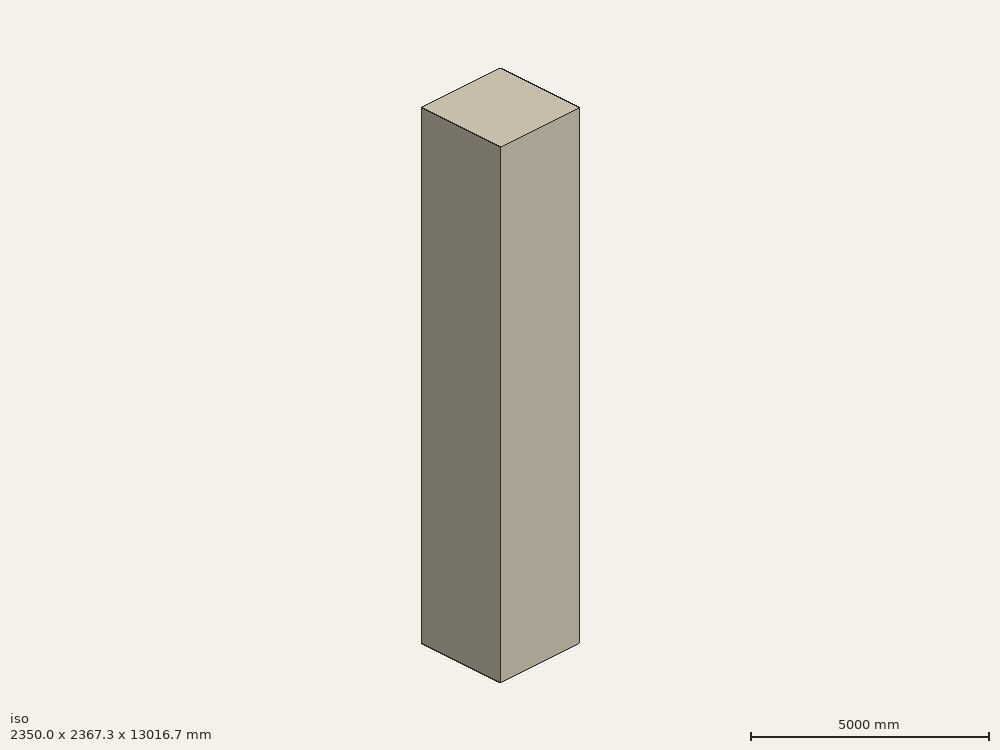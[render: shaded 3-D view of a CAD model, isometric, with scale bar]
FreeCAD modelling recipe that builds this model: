
FCSTD DOCUMENT  (FreeCAD 1.0R39109 (Git))
Label: revolveTester-7_scaled-a
License: All rights reserved
objects: App::DocumentObjectGroupPython×1252, Spreadsheet::Sheet×2, Part::FeaturePython×2, App::Part×2, Part::Cylinder×1, Sketcher::SketchObject×1, Part::Revolution×1, Part::Cut×1
note: 7 computed .brp shape members not serialized (recipe doc carries the construction recipe); baked Part::Feature solids carry a one-line shape summary decoded from their .brp

FEATURE [Spreadsheet::Sheet] defines
  cells = A1='constant; B1='HALFPI; C1(HALFPI)==pi / 2; A2='constant; B2='PI; C2(PI)==1 * pi; A3='constant; B3='TWOPI; C3(TWOPI)==2 * pi
FEATURE [Spreadsheet::Sheet] gdmlInfo
FEATURE [App::DocumentObjectGroupPython] Define  # scripted group (container) (typed FeaturePython)
  Group = -> [defines,gdmlInfo]
FEATURE [App::DocumentObjectGroupPython] HALFPI  # scripted group (container) (typed FeaturePython)
  name = HALFPI
  value = pi/2.
FEATURE [App::DocumentObjectGroupPython] PI  # scripted group (container) (typed FeaturePython)
  name = PI
  value = 1.*pi
FEATURE [App::DocumentObjectGroupPython] TWOPI  # scripted group (container) (typed FeaturePython)
  name = TWOPI
  value = 2.*pi
FEATURE [App::DocumentObjectGroupPython] Constants  # scripted group (container) (typed FeaturePython)
  Group = -> [HALFPI,PI,TWOPI]
FEATURE [App::DocumentObjectGroupPython] Quantities  # scripted group (container) (typed FeaturePython)
FEATURE [App::DocumentObjectGroupPython] Variables  # scripted group (container) (typed FeaturePython)
FEATURE [App::DocumentObjectGroupPython] Isotopes  # scripted group (container) (typed FeaturePython)
FEATURE [App::DocumentObjectGroupPython] Elements  # scripted group (container) (typed FeaturePython)
FEATURE [App::DocumentObjectGroupPython] Matrix  # scripted group (container) (typed FeaturePython)
FEATURE [App::DocumentObjectGroupPython] Surfaces  # scripted group (container) (typed FeaturePython)
FEATURE [App::DocumentObjectGroupPython] Opticals  # scripted group (container) (typed FeaturePython)
  Group = -> [Matrix,Surfaces]
FEATURE [App::DocumentObjectGroupPython] G4Isotopes  # scripted group (container) (typed FeaturePython)
FEATURE [App::DocumentObjectGroupPython] H_element  # scripted group (container) (typed FeaturePython)
  Z = 1
  atom_value = 1.008
  formula = H
  name = H_element
FEATURE [App::DocumentObjectGroupPython] He_element  # scripted group (container) (typed FeaturePython)
  Z = 2
  atom_value = 4.0026
  formula = He
  name = He_element
FEATURE [App::DocumentObjectGroupPython] Li_element  # scripted group (container) (typed FeaturePython)
  Z = 3
  atom_value = 6.94
  formula = Li
  name = Li_element
FEATURE [App::DocumentObjectGroupPython] Be_element  # scripted group (container) (typed FeaturePython)
  Z = 4
  atom_value = 9.01218
  formula = Be
  name = Be_element
FEATURE [App::DocumentObjectGroupPython] B_element  # scripted group (container) (typed FeaturePython)
  Z = 5
  atom_value = 10.81
  formula = B
  name = B_element
FEATURE [App::DocumentObjectGroupPython] C_element  # scripted group (container) (typed FeaturePython)
  Z = 6
  atom_value = 12.011
  formula = C
  name = C_element
FEATURE [App::DocumentObjectGroupPython] N_element  # scripted group (container) (typed FeaturePython)
  Z = 7
  atom_value = 14.007
  formula = N
  name = N_element
FEATURE [App::DocumentObjectGroupPython] O_element  # scripted group (container) (typed FeaturePython)
  Z = 8
  atom_value = 15.999
  formula = O
  name = O_element
FEATURE [App::DocumentObjectGroupPython] F_element  # scripted group (container) (typed FeaturePython)
  Z = 9
  atom_value = 18.9984
  formula = F
  name = F_element
FEATURE [App::DocumentObjectGroupPython] Ne_element  # scripted group (container) (typed FeaturePython)
  Z = 10
  atom_value = 20.1797
  formula = Ne
  name = Ne_element
FEATURE [App::DocumentObjectGroupPython] Na_element  # scripted group (container) (typed FeaturePython)
  Z = 11
  atom_value = 22.9898
  formula = Na
  name = Na_element
FEATURE [App::DocumentObjectGroupPython] Mg_element  # scripted group (container) (typed FeaturePython)
  Z = 12
  atom_value = 24.305
  formula = Mg
  name = Mg_element
FEATURE [App::DocumentObjectGroupPython] Al_element  # scripted group (container) (typed FeaturePython)
  Z = 13
  atom_value = 26.9815
  formula = Al
  name = Al_element
FEATURE [App::DocumentObjectGroupPython] Si_element  # scripted group (container) (typed FeaturePython)
  Z = 14
  atom_value = 28.085
  formula = Si
  name = Si_element
FEATURE [App::DocumentObjectGroupPython] P_element  # scripted group (container) (typed FeaturePython)
  Z = 15
  atom_value = 30.9738
  formula = P
  name = P_element
FEATURE [App::DocumentObjectGroupPython] S_element  # scripted group (container) (typed FeaturePython)
  Z = 16
  atom_value = 32.06
  formula = S
  name = S_element
FEATURE [App::DocumentObjectGroupPython] Cl_element  # scripted group (container) (typed FeaturePython)
  Z = 17
  atom_value = 35.45
  formula = Cl
  name = Cl_element
FEATURE [App::DocumentObjectGroupPython] Ar_element  # scripted group (container) (typed FeaturePython)
  Z = 18
  atom_value = 39.95
  formula = Ar
  name = Ar_element
FEATURE [App::DocumentObjectGroupPython] K_element  # scripted group (container) (typed FeaturePython)
  Z = 19
  atom_value = 39.0983
  formula = K
  name = K_element
FEATURE [App::DocumentObjectGroupPython] Ca_element  # scripted group (container) (typed FeaturePython)
  Z = 20
  atom_value = 40.078
  formula = Ca
  name = Ca_element
FEATURE [App::DocumentObjectGroupPython] Sc_element  # scripted group (container) (typed FeaturePython)
  Z = 21
  atom_value = 44.9559
  formula = Sc
  name = Sc_element
FEATURE [App::DocumentObjectGroupPython] Ti_element  # scripted group (container) (typed FeaturePython)
  Z = 22
  atom_value = 47.867
  formula = Ti
  name = Ti_element
FEATURE [App::DocumentObjectGroupPython] V_element  # scripted group (container) (typed FeaturePython)
  Z = 23
  atom_value = 50.9415
  formula = V
  name = V_element
FEATURE [App::DocumentObjectGroupPython] Cr_element  # scripted group (container) (typed FeaturePython)
  Z = 24
  atom_value = 51.9961
  formula = Cr
  name = Cr_element
FEATURE [App::DocumentObjectGroupPython] Mn_element  # scripted group (container) (typed FeaturePython)
  Z = 25
  atom_value = 54.938
  formula = Mn
  name = Mn_element
FEATURE [App::DocumentObjectGroupPython] Fe_element  # scripted group (container) (typed FeaturePython)
  Z = 26
  atom_value = 55.845
  formula = Fe
  name = Fe_element
FEATURE [App::DocumentObjectGroupPython] Co_element  # scripted group (container) (typed FeaturePython)
  Z = 27
  atom_value = 58.9332
  formula = Co
  name = Co_element
FEATURE [App::DocumentObjectGroupPython] Ni_element  # scripted group (container) (typed FeaturePython)
  Z = 28
  atom_value = 58.6934
  formula = Ni
  name = Ni_element
FEATURE [App::DocumentObjectGroupPython] Cu_element  # scripted group (container) (typed FeaturePython)
  Z = 29
  atom_value = 63.546
  formula = Cu
  name = Cu_element
FEATURE [App::DocumentObjectGroupPython] Zn_element  # scripted group (container) (typed FeaturePython)
  Z = 30
  atom_value = 65.38
  formula = Zn
  name = Zn_element
FEATURE [App::DocumentObjectGroupPython] Ga_element  # scripted group (container) (typed FeaturePython)
  Z = 31
  atom_value = 69.723
  formula = Ga
  name = Ga_element
FEATURE [App::DocumentObjectGroupPython] Ge_element  # scripted group (container) (typed FeaturePython)
  Z = 32
  atom_value = 72.63
  formula = Ge
  name = Ge_element
FEATURE [App::DocumentObjectGroupPython] As_element  # scripted group (container) (typed FeaturePython)
  Z = 33
  atom_value = 74.9216
  formula = As
  name = As_element
FEATURE [App::DocumentObjectGroupPython] Se_element  # scripted group (container) (typed FeaturePython)
  Z = 34
  atom_value = 78.971
  formula = Se
  name = Se_element
FEATURE [App::DocumentObjectGroupPython] Br_element  # scripted group (container) (typed FeaturePython)
  Z = 35
  atom_value = 79.904
  formula = Br
  name = Br_element
FEATURE [App::DocumentObjectGroupPython] Kr_element  # scripted group (container) (typed FeaturePython)
  Z = 36
  atom_value = 83.798
  formula = Kr
  name = Kr_element
FEATURE [App::DocumentObjectGroupPython] Rb_element  # scripted group (container) (typed FeaturePython)
  Z = 37
  atom_value = 85.4678
  formula = Rb
  name = Rb_element
FEATURE [App::DocumentObjectGroupPython] Sr_element  # scripted group (container) (typed FeaturePython)
  Z = 38
  atom_value = 87.62
  formula = Sr
  name = Sr_element
FEATURE [App::DocumentObjectGroupPython] Y_element  # scripted group (container) (typed FeaturePython)
  Z = 39
  atom_value = 88.9058
  formula = Y
  name = Y_element
FEATURE [App::DocumentObjectGroupPython] Zr_element  # scripted group (container) (typed FeaturePython)
  Z = 40
  atom_value = 91.224
  formula = Zr
  name = Zr_element
FEATURE [App::DocumentObjectGroupPython] Nb_element  # scripted group (container) (typed FeaturePython)
  Z = 41
  atom_value = 92.9064
  formula = Nb
  name = Nb_element
FEATURE [App::DocumentObjectGroupPython] Mo_element  # scripted group (container) (typed FeaturePython)
  Z = 42
  atom_value = 95.95
  formula = Mo
  name = Mo_element
FEATURE [App::DocumentObjectGroupPython] Tc_element  # scripted group (container) (typed FeaturePython)
  Z = 43
  atom_value = 97
  formula = Tc
  name = Tc_element
FEATURE [App::DocumentObjectGroupPython] Ru_element  # scripted group (container) (typed FeaturePython)
  Z = 44
  atom_value = 101.07
  formula = Ru
  name = Ru_element
FEATURE [App::DocumentObjectGroupPython] Rh_element  # scripted group (container) (typed FeaturePython)
  Z = 45
  atom_value = 102.905
  formula = Rh
  name = Rh_element
FEATURE [App::DocumentObjectGroupPython] Pd_element  # scripted group (container) (typed FeaturePython)
  Z = 46
  atom_value = 106.42
  formula = Pd
  name = Pd_element
FEATURE [App::DocumentObjectGroupPython] Ag_element  # scripted group (container) (typed FeaturePython)
  Z = 47
  atom_value = 107.868
  formula = Ag
  name = Ag_element
FEATURE [App::DocumentObjectGroupPython] Cd_element  # scripted group (container) (typed FeaturePython)
  Z = 48
  atom_value = 112.414
  formula = Cd
  name = Cd_element
FEATURE [App::DocumentObjectGroupPython] In_element  # scripted group (container) (typed FeaturePython)
  Z = 49
  atom_value = 114.818
  formula = In
  name = In_element
FEATURE [App::DocumentObjectGroupPython] Sn_element  # scripted group (container) (typed FeaturePython)
  Z = 50
  atom_value = 118.71
  formula = Sn
  name = Sn_element
FEATURE [App::DocumentObjectGroupPython] Sb_element  # scripted group (container) (typed FeaturePython)
  Z = 51
  atom_value = 121.76
  formula = Sb
  name = Sb_element
FEATURE [App::DocumentObjectGroupPython] Te_element  # scripted group (container) (typed FeaturePython)
  Z = 52
  atom_value = 127.6
  formula = Te
  name = Te_element
FEATURE [App::DocumentObjectGroupPython] I_element  # scripted group (container) (typed FeaturePython)
  Z = 53
  atom_value = 126.904
  formula = I
  name = I_element
FEATURE [App::DocumentObjectGroupPython] Xe_element  # scripted group (container) (typed FeaturePython)
  Z = 54
  atom_value = 131.293
  formula = Xe
  name = Xe_element
FEATURE [App::DocumentObjectGroupPython] Cs_element  # scripted group (container) (typed FeaturePython)
  Z = 55
  atom_value = 132.905
  formula = Cs
  name = Cs_element
FEATURE [App::DocumentObjectGroupPython] Ba_element  # scripted group (container) (typed FeaturePython)
  Z = 56
  atom_value = 137.327
  formula = Ba
  name = Ba_element
FEATURE [App::DocumentObjectGroupPython] La_element  # scripted group (container) (typed FeaturePython)
  Z = 57
  atom_value = 138.905
  formula = La
  name = La_element
FEATURE [App::DocumentObjectGroupPython] Ce_element  # scripted group (container) (typed FeaturePython)
  Z = 58
  atom_value = 140.116
  formula = Ce
  name = Ce_element
FEATURE [App::DocumentObjectGroupPython] Pr_element  # scripted group (container) (typed FeaturePython)
  Z = 59
  atom_value = 140.908
  formula = Pr
  name = Pr_element
FEATURE [App::DocumentObjectGroupPython] Nd_element  # scripted group (container) (typed FeaturePython)
  Z = 60
  atom_value = 144.242
  formula = Nd
  name = Nd_element
FEATURE [App::DocumentObjectGroupPython] Pm_element  # scripted group (container) (typed FeaturePython)
  Z = 61
  atom_value = 145
  formula = Pm
  name = Pm_element
FEATURE [App::DocumentObjectGroupPython] Sm_element  # scripted group (container) (typed FeaturePython)
  Z = 62
  atom_value = 150.36
  formula = Sm
  name = Sm_element
FEATURE [App::DocumentObjectGroupPython] Eu_element  # scripted group (container) (typed FeaturePython)
  Z = 63
  atom_value = 151.964
  formula = Eu
  name = Eu_element
FEATURE [App::DocumentObjectGroupPython] Gd_element  # scripted group (container) (typed FeaturePython)
  Z = 64
  atom_value = 157.25
  formula = Gd
  name = Gd_element
FEATURE [App::DocumentObjectGroupPython] Tb_element  # scripted group (container) (typed FeaturePython)
  Z = 65
  atom_value = 158.925
  formula = Tb
  name = Tb_element
FEATURE [App::DocumentObjectGroupPython] Dy_element  # scripted group (container) (typed FeaturePython)
  Z = 66
  atom_value = 162.5
  formula = Dy
  name = Dy_element
FEATURE [App::DocumentObjectGroupPython] Ho_element  # scripted group (container) (typed FeaturePython)
  Z = 67
  atom_value = 164.93
  formula = Ho
  name = Ho_element
FEATURE [App::DocumentObjectGroupPython] Er_element  # scripted group (container) (typed FeaturePython)
  Z = 68
  atom_value = 167.259
  formula = Er
  name = Er_element
FEATURE [App::DocumentObjectGroupPython] Tm_element  # scripted group (container) (typed FeaturePython)
  Z = 69
  atom_value = 168.934
  formula = Tm
  name = Tm_element
FEATURE [App::DocumentObjectGroupPython] Yb_element  # scripted group (container) (typed FeaturePython)
  Z = 70
  atom_value = 173.045
  formula = Yb
  name = Yb_element
FEATURE [App::DocumentObjectGroupPython] Lu_element  # scripted group (container) (typed FeaturePython)
  Z = 71
  atom_value = 174.967
  formula = Lu
  name = Lu_element
FEATURE [App::DocumentObjectGroupPython] Hf_element  # scripted group (container) (typed FeaturePython)
  Z = 72
  atom_value = 178.49
  formula = Hf
  name = Hf_element
FEATURE [App::DocumentObjectGroupPython] Ta_element  # scripted group (container) (typed FeaturePython)
  Z = 73
  atom_value = 180.948
  formula = Ta
  name = Ta_element
FEATURE [App::DocumentObjectGroupPython] W_element  # scripted group (container) (typed FeaturePython)
  Z = 74
  atom_value = 183.84
  formula = W
  name = W_element
FEATURE [App::DocumentObjectGroupPython] Re_element  # scripted group (container) (typed FeaturePython)
  Z = 75
  atom_value = 186.207
  formula = Re
  name = Re_element
FEATURE [App::DocumentObjectGroupPython] Os_element  # scripted group (container) (typed FeaturePython)
  Z = 76
  atom_value = 190.23
  formula = Os
  name = Os_element
FEATURE [App::DocumentObjectGroupPython] Ir_element  # scripted group (container) (typed FeaturePython)
  Z = 77
  atom_value = 192.217
  formula = Ir
  name = Ir_element
FEATURE [App::DocumentObjectGroupPython] Pt_element  # scripted group (container) (typed FeaturePython)
  Z = 78
  atom_value = 195.084
  formula = Pt
  name = Pt_element
FEATURE [App::DocumentObjectGroupPython] Au_element  # scripted group (container) (typed FeaturePython)
  Z = 79
  atom_value = 196.967
  formula = Au
  name = Au_element
FEATURE [App::DocumentObjectGroupPython] Hg_element  # scripted group (container) (typed FeaturePython)
  Z = 80
  atom_value = 200.592
  formula = Hg
  name = Hg_element
FEATURE [App::DocumentObjectGroupPython] Tl_element  # scripted group (container) (typed FeaturePython)
  Z = 81
  atom_value = 204.38
  formula = Tl
  name = Tl_element
FEATURE [App::DocumentObjectGroupPython] Pb_element  # scripted group (container) (typed FeaturePython)
  Z = 82
  atom_value = 207.2
  formula = Pb
  name = Pb_element
FEATURE [App::DocumentObjectGroupPython] Bi_element  # scripted group (container) (typed FeaturePython)
  Z = 83
  atom_value = 208.98
  formula = Bi
  name = Bi_element
FEATURE [App::DocumentObjectGroupPython] Po_element  # scripted group (container) (typed FeaturePython)
  Z = 84
  atom_value = 209
  formula = Po
  name = Po_element
FEATURE [App::DocumentObjectGroupPython] At_element  # scripted group (container) (typed FeaturePython)
  Z = 85
  atom_value = 210
  formula = At
  name = At_element
FEATURE [App::DocumentObjectGroupPython] Rn_element  # scripted group (container) (typed FeaturePython)
  Z = 86
  atom_value = 222
  formula = Rn
  name = Rn_element
FEATURE [App::DocumentObjectGroupPython] Fr_element  # scripted group (container) (typed FeaturePython)
  Z = 87
  atom_value = 223
  formula = Fr
  name = Fr_element
FEATURE [App::DocumentObjectGroupPython] Ra_element  # scripted group (container) (typed FeaturePython)
  Z = 88
  atom_value = 226
  formula = Ra
  name = Ra_element
FEATURE [App::DocumentObjectGroupPython] Ac_element  # scripted group (container) (typed FeaturePython)
  Z = 89
  atom_value = 227
  formula = Ac
  name = Ac_element
FEATURE [App::DocumentObjectGroupPython] Th_element  # scripted group (container) (typed FeaturePython)
  Z = 90
  atom_value = 232.038
  formula = Th
  name = Th_element
FEATURE [App::DocumentObjectGroupPython] Pa_element  # scripted group (container) (typed FeaturePython)
  Z = 91
  atom_value = 231.036
  formula = Pa
  name = Pa_element
FEATURE [App::DocumentObjectGroupPython] U_element  # scripted group (container) (typed FeaturePython)
  Z = 92
  atom_value = 238.029
  formula = U
  name = U_element
FEATURE [App::DocumentObjectGroupPython] Np_element  # scripted group (container) (typed FeaturePython)
  Z = 93
  atom_value = 237
  formula = Np
  name = Np_element
FEATURE [App::DocumentObjectGroupPython] Pu_element  # scripted group (container) (typed FeaturePython)
  Z = 94
  atom_value = 244
  formula = Pu
  name = Pu_element
FEATURE [App::DocumentObjectGroupPython] Am_element  # scripted group (container) (typed FeaturePython)
  Z = 95
  atom_value = 243
  formula = Am
  name = Am_element
FEATURE [App::DocumentObjectGroupPython] Cm_element  # scripted group (container) (typed FeaturePython)
  Z = 96
  atom_value = 247
  formula = Cm
  name = Cm_element
FEATURE [App::DocumentObjectGroupPython] Bk_element  # scripted group (container) (typed FeaturePython)
  Z = 97
  atom_value = 247
  formula = Bk
  name = Bk_element
FEATURE [App::DocumentObjectGroupPython] Cf_element  # scripted group (container) (typed FeaturePython)
  Z = 98
  atom_value = 251
  formula = Cf
  name = Cf_element
FEATURE [App::DocumentObjectGroupPython] G4Elements  # scripted group (container) (typed FeaturePython)
  Group = -> [H_element,He_element,Li_element,Be_element,B_element,C_element,N_element,O_element,F_element,Ne_element,Na_element,Mg_element,Al_element,Si_element,P_element,S_element,Cl_element,Ar_element,K_element,Ca_element,Sc_element,Ti_element,V_element,Cr_element,Mn_element,Fe_element,Co_element,Ni_element,Cu_element,Zn_element,Ga_element,Ge_element,As_element,Se_element,Br_element,Kr_element,Rb_element,+61 more]
FEATURE [App::DocumentObjectGroupPython] H_element001  label="H_element : 0.101"  # scripted group (container) (typed FeaturePython)
  n = 0.101327
FEATURE [App::DocumentObjectGroupPython] C_element001  label="C_element : 0.775"  # scripted group (container) (typed FeaturePython)
  n = 0.7755
FEATURE [App::DocumentObjectGroupPython] N_element001  label="N_element : 0.035"  # scripted group (container) (typed FeaturePython)
  n = 0.035057
FEATURE [App::DocumentObjectGroupPython] O_element001  label="O_element : 0.052"  # scripted group (container) (typed FeaturePython)
  n = 0.0523159
FEATURE [App::DocumentObjectGroupPython] F_element001  label="F_element : 0.017"  # scripted group (container) (typed FeaturePython)
  n = 0.017422
FEATURE [App::DocumentObjectGroupPython] Ca_element001  label="Ca_element : 0.018"  # scripted group (container) (typed FeaturePython)
  n = 0.018378
FEATURE [App::DocumentObjectGroupPython] G4_A_150_TISSUE  label="G4_A-150_TISSUE"  # scripted group (container) (typed FeaturePython)
  Dunit = g/cm3
  Dvalue = 1.127
  Group = -> [H_element001,C_element001,N_element001,O_element001,F_element001,Ca_element001]
  conduct = 2
  density = 1
  expand = 3
  formula = G4_A-150_TISSUE
  name = G4_A-150_TISSUE
  specific = 4
FEATURE [App::DocumentObjectGroupPython] C_element002  label="C_element : 3"  # scripted group (container) (typed FeaturePython)
  n = 3
  ref = C_element
FEATURE [App::DocumentObjectGroupPython] H_element002  label="H_element : 6"  # scripted group (container) (typed FeaturePython)
  n = 6
  ref = H_element
FEATURE [App::DocumentObjectGroupPython] O_element002  label="O_element : 1"  # scripted group (container) (typed FeaturePython)
  n = 1
  ref = O_element
FEATURE [App::DocumentObjectGroupPython] G4_ACETONE  # scripted group (container) (typed FeaturePython)
  Dunit = g/cm3
  Dvalue = 0.7899
  Group = -> [C_element002,H_element002,O_element002]
  conduct = 2
  density = 1
  expand = 3
  formula = G4_ACETONE
  name = G4_ACETONE
  specific = 4
FEATURE [App::DocumentObjectGroupPython] C_element003  label="C_element : 2"  # scripted group (container) (typed FeaturePython)
  n = 2
  ref = C_element
FEATURE [App::DocumentObjectGroupPython] H_element003  label="H_element : 2"  # scripted group (container) (typed FeaturePython)
  n = 2
  ref = H_element
FEATURE [App::DocumentObjectGroupPython] G4_ACETYLENE  # scripted group (container) (typed FeaturePython)
  Dunit = g/cm3
  Dvalue = 0.0010967
  Group = -> [C_element003,H_element003]
  conduct = 2
  density = 1
  expand = 3
  formula = G4_ACETYLENE
  name = G4_ACETYLENE
  specific = 4
FEATURE [App::DocumentObjectGroupPython] C_element004  label="C_element : 5"  # scripted group (container) (typed FeaturePython)
  n = 5
  ref = C_element
FEATURE [App::DocumentObjectGroupPython] H_element004  label="H_element : 5"  # scripted group (container) (typed FeaturePython)
  n = 5
  ref = H_element
FEATURE [App::DocumentObjectGroupPython] N_element002  label="N_element : 5"  # scripted group (container) (typed FeaturePython)
  n = 5
  ref = N_element
FEATURE [App::DocumentObjectGroupPython] G4_ADENINE  # scripted group (container) (typed FeaturePython)
  Dunit = g/cm3
  Dvalue = 1.6
  Group = -> [C_element004,H_element004,N_element002]
  conduct = 2
  density = 1
  expand = 3
  formula = G4_ADENINE
  name = G4_ADENINE
  specific = 4
FEATURE [App::DocumentObjectGroupPython] H_element005  label="H_element : 0.114"  # scripted group (container) (typed FeaturePython)
  n = 0.114
FEATURE [App::DocumentObjectGroupPython] C_element005  label="C_element : 0.598"  # scripted group (container) (typed FeaturePython)
  n = 0.598
FEATURE [App::DocumentObjectGroupPython] N_element003  label="N_element : 0.007"  # scripted group (container) (typed FeaturePython)
  n = 0.007
FEATURE [App::DocumentObjectGroupPython] O_element003  label="O_element : 0.278"  # scripted group (container) (typed FeaturePython)
  n = 0.278
FEATURE [App::DocumentObjectGroupPython] Na_element001  label="Na_element : 0.001"  # scripted group (container) (typed FeaturePython)
  n = 0.001
FEATURE [App::DocumentObjectGroupPython] S_element001  label="S_element : 0.001"  # scripted group (container) (typed FeaturePython)
  n = 0.001
FEATURE [App::DocumentObjectGroupPython] Cl_element001  label="Cl_element : 0.001"  # scripted group (container) (typed FeaturePython)
  n = 0.001
FEATURE [App::DocumentObjectGroupPython] G4_ADIPOSE_TISSUE_ICRP  # scripted group (container) (typed FeaturePython)
  Dunit = g/cm3
  Dvalue = 0.95
  Group = -> [H_element005,C_element005,N_element003,O_element003,Na_element001,S_element001,Cl_element001]
  conduct = 2
  density = 1
  expand = 3
  formula = G4_ADIPOSE_TISSUE_ICRP
  name = G4_ADIPOSE_TISSUE_ICRP
  specific = 4
FEATURE [App::DocumentObjectGroupPython] C_element006  label="C_element : 0.000"  # scripted group (container) (typed FeaturePython)
  n = 0.000124
FEATURE [App::DocumentObjectGroupPython] N_element004  label="N_element : 0.755"  # scripted group (container) (typed FeaturePython)
  n = 0.755268
FEATURE [App::DocumentObjectGroupPython] O_element004  label="O_element : 0.232"  # scripted group (container) (typed FeaturePython)
  n = 0.231781
FEATURE [App::DocumentObjectGroupPython] Ar_element001  label="Ar_element : 0.013"  # scripted group (container) (typed FeaturePython)
  n = 0.012827
FEATURE [App::DocumentObjectGroupPython] G4_AIR  # scripted group (container) (typed FeaturePython)
  Dunit = g/cm3
  Dvalue = 0.00120479
  Group = -> [C_element006,N_element004,O_element004,Ar_element001]
  conduct = 2
  density = 1
  expand = 3
  formula = G4_AIR
  name = G4_AIR
  specific = 4
FEATURE [App::DocumentObjectGroupPython] C_element007  label="C_element : 006"  # scripted group (container) (typed FeaturePython)
  n = 3
  ref = C_element
FEATURE [App::DocumentObjectGroupPython] H_element006  label="H_element : 7"  # scripted group (container) (typed FeaturePython)
  n = 7
  ref = H_element
FEATURE [App::DocumentObjectGroupPython] N_element005  label="N_element : 1"  # scripted group (container) (typed FeaturePython)
  n = 1
  ref = N_element
FEATURE [App::DocumentObjectGroupPython] O_element005  label="O_element : 2"  # scripted group (container) (typed FeaturePython)
  n = 2
  ref = O_element
FEATURE [App::DocumentObjectGroupPython] G4_ALANINE  # scripted group (container) (typed FeaturePython)
  Dunit = g/cm3
  Dvalue = 1.42
  Group = -> [C_element007,H_element006,N_element005,O_element005]
  conduct = 2
  density = 1
  expand = 3
  formula = G4_ALANINE
  name = G4_ALANINE
  specific = 4
FEATURE [App::DocumentObjectGroupPython] Al_element001  label="Al_element : 2"  # scripted group (container) (typed FeaturePython)
  n = 2
  ref = Al_element
FEATURE [App::DocumentObjectGroupPython] O_element006  label="O_element : 3"  # scripted group (container) (typed FeaturePython)
  n = 3
  ref = O_element
FEATURE [App::DocumentObjectGroupPython] G4_ALUMINUM_OXIDE  # scripted group (container) (typed FeaturePython)
  Dunit = g/cm3
  Dvalue = 3.97
  Group = -> [Al_element001,O_element006]
  conduct = 2
  density = 1
  expand = 3
  formula = G4_ALUMINUM_OXIDE
  name = G4_ALUMINUM_OXIDE
  specific = 4
FEATURE [App::DocumentObjectGroupPython] H_element007  label="H_element : 0.106"  # scripted group (container) (typed FeaturePython)
  n = 0.10593
FEATURE [App::DocumentObjectGroupPython] C_element008  label="C_element : 0.789"  # scripted group (container) (typed FeaturePython)
  n = 0.788974
FEATURE [App::DocumentObjectGroupPython] O_element007  label="O_element : 0.105"  # scripted group (container) (typed FeaturePython)
  n = 0.105096
FEATURE [App::DocumentObjectGroupPython] G4_AMBER  # scripted group (container) (typed FeaturePython)
  Dunit = g/cm3
  Dvalue = 1.1
  Group = -> [H_element007,C_element008,O_element007]
  conduct = 2
  density = 1
  expand = 3
  formula = G4_AMBER
  name = G4_AMBER
  specific = 4
FEATURE [App::DocumentObjectGroupPython] N_element006  label="N_element : 006"  # scripted group (container) (typed FeaturePython)
  n = 1
  ref = N_element
FEATURE [App::DocumentObjectGroupPython] H_element008  label="H_element : 3"  # scripted group (container) (typed FeaturePython)
  n = 3
  ref = H_element
FEATURE [App::DocumentObjectGroupPython] G4_AMMONIA  # scripted group (container) (typed FeaturePython)
  Dunit = g/cm3
  Dvalue = 0.000826019
  Group = -> [N_element006,H_element008]
  conduct = 2
  density = 1
  expand = 3
  formula = G4_AMMONIA
  name = G4_AMMONIA
  specific = 4
FEATURE [App::DocumentObjectGroupPython] C_element009  label="C_element : 6"  # scripted group (container) (typed FeaturePython)
  n = 6
  ref = C_element
FEATURE [App::DocumentObjectGroupPython] H_element009  label="H_element : 008"  # scripted group (container) (typed FeaturePython)
  n = 7
  ref = H_element
FEATURE [App::DocumentObjectGroupPython] N_element007  label="N_element : 007"  # scripted group (container) (typed FeaturePython)
  n = 1
  ref = N_element
FEATURE [App::DocumentObjectGroupPython] G4_ANILINE  # scripted group (container) (typed FeaturePython)
  Dunit = g/cm3
  Dvalue = 1.0235
  Group = -> [C_element009,H_element009,N_element007]
  conduct = 2
  density = 1
  expand = 3
  formula = G4_ANILINE
  name = G4_ANILINE
  specific = 4
FEATURE [App::DocumentObjectGroupPython] C_element010  label="C_element : 14"  # scripted group (container) (typed FeaturePython)
  n = 14
  ref = C_element
FEATURE [App::DocumentObjectGroupPython] H_element010  label="H_element : 10"  # scripted group (container) (typed FeaturePython)
  n = 10
  ref = H_element
FEATURE [App::DocumentObjectGroupPython] G4_ANTHRACENE  # scripted group (container) (typed FeaturePython)
  Dunit = g/cm3
  Dvalue = 1.283
  Group = -> [C_element010,H_element010]
  conduct = 2
  density = 1
  expand = 3
  formula = G4_ANTHRACENE
  name = G4_ANTHRACENE
  specific = 4
FEATURE [App::DocumentObjectGroupPython] H_element011  label="H_element : 0.065"  # scripted group (container) (typed FeaturePython)
  n = 0.0654709
FEATURE [App::DocumentObjectGroupPython] C_element011  label="C_element : 0.537"  # scripted group (container) (typed FeaturePython)
  n = 0.536944
FEATURE [App::DocumentObjectGroupPython] N_element008  label="N_element : 0.021"  # scripted group (container) (typed FeaturePython)
  n = 0.0215
FEATURE [App::DocumentObjectGroupPython] O_element008  label="O_element : 0.032"  # scripted group (container) (typed FeaturePython)
  n = 0.032085
FEATURE [App::DocumentObjectGroupPython] F_element002  label="F_element : 0.167"  # scripted group (container) (typed FeaturePython)
  n = 0.167411
FEATURE [App::DocumentObjectGroupPython] Ca_element002  label="Ca_element : 0.177"  # scripted group (container) (typed FeaturePython)
  n = 0.176589
FEATURE [App::DocumentObjectGroupPython] G4_B_100_BONE  label="G4_B-100_BONE"  # scripted group (container) (typed FeaturePython)
  Dunit = g/cm3
  Dvalue = 1.45
  Group = -> [H_element011,C_element011,N_element008,O_element008,F_element002,Ca_element002]
  conduct = 2
  density = 1
  expand = 3
  formula = G4_B-100_BONE
  name = G4_B-100_BONE
  specific = 4
FEATURE [App::DocumentObjectGroupPython] H_element012  label="H_element : 0.057"  # scripted group (container) (typed FeaturePython)
  n = 0.057441
FEATURE [App::DocumentObjectGroupPython] C_element012  label="C_element : 0.790"  # scripted group (container) (typed FeaturePython)
  n = 0.774591
FEATURE [App::DocumentObjectGroupPython] O_element009  label="O_element : 0.168"  # scripted group (container) (typed FeaturePython)
  n = 0.167968
FEATURE [App::DocumentObjectGroupPython] G4_BAKELITE  # scripted group (container) (typed FeaturePython)
  Dunit = g/cm3
  Dvalue = 1.25
  Group = -> [H_element012,C_element012,O_element009]
  conduct = 2
  density = 1
  expand = 3
  formula = G4_BAKELITE
  name = G4_BAKELITE
  specific = 4
FEATURE [App::DocumentObjectGroupPython] Ba_element001  label="Ba_element : 1"  # scripted group (container) (typed FeaturePython)
  n = 1
  ref = Ba_element
FEATURE [App::DocumentObjectGroupPython] F_element003  label="F_element : 2"  # scripted group (container) (typed FeaturePython)
  n = 2
  ref = F_element
FEATURE [App::DocumentObjectGroupPython] G4_BARIUM_FLUORIDE  # scripted group (container) (typed FeaturePython)
  Dunit = g/cm3
  Dvalue = 4.89
  Group = -> [Ba_element001,F_element003]
  conduct = 2
  density = 1
  expand = 3
  formula = G4_BARIUM_FLUORIDE
  name = G4_BARIUM_FLUORIDE
  specific = 4
FEATURE [App::DocumentObjectGroupPython] Ba_element002  label="Ba_element : 002"  # scripted group (container) (typed FeaturePython)
  n = 1
  ref = Ba_element
FEATURE [App::DocumentObjectGroupPython] S_element002  label="S_element : 1"  # scripted group (container) (typed FeaturePython)
  n = 1
  ref = S_element
FEATURE [App::DocumentObjectGroupPython] O_element010  label="O_element : 4"  # scripted group (container) (typed FeaturePython)
  n = 4
  ref = O_element
FEATURE [App::DocumentObjectGroupPython] G4_BARIUM_SULFATE  # scripted group (container) (typed FeaturePython)
  Dunit = g/cm3
  Dvalue = 4.5
  Group = -> [Ba_element002,S_element002,O_element010]
  conduct = 2
  density = 1
  expand = 3
  formula = G4_BARIUM_SULFATE
  name = G4_BARIUM_SULFATE
  specific = 4
FEATURE [App::DocumentObjectGroupPython] C_element013  label="C_element : 007"  # scripted group (container) (typed FeaturePython)
  n = 6
  ref = C_element
FEATURE [App::DocumentObjectGroupPython] H_element013  label="H_element : 009"  # scripted group (container) (typed FeaturePython)
  n = 6
  ref = H_element
FEATURE [App::DocumentObjectGroupPython] G4_BENZENE  # scripted group (container) (typed FeaturePython)
  Dunit = g/cm3
  Dvalue = 0.87865
  Group = -> [C_element013,H_element013]
  conduct = 2
  density = 1
  expand = 3
  formula = G4_BENZENE
  name = G4_BENZENE
  specific = 4
FEATURE [App::DocumentObjectGroupPython] Be_element001  label="Be_element : 1"  # scripted group (container) (typed FeaturePython)
  n = 1
  ref = Be_element
FEATURE [App::DocumentObjectGroupPython] O_element011  label="O_element : 005"  # scripted group (container) (typed FeaturePython)
  n = 1
  ref = O_element
FEATURE [App::DocumentObjectGroupPython] G4_BERYLLIUM_OXIDE  # scripted group (container) (typed FeaturePython)
  Dunit = g/cm3
  Dvalue = 3.01
  Group = -> [Be_element001,O_element011]
  conduct = 2
  density = 1
  expand = 3
  formula = G4_BERYLLIUM_OXIDE
  name = G4_BERYLLIUM_OXIDE
  specific = 4
FEATURE [App::DocumentObjectGroupPython] Bi_element001  label="Bi_element : 4"  # scripted group (container) (typed FeaturePython)
  n = 4
  ref = Bi_element
FEATURE [App::DocumentObjectGroupPython] Ge_element001  label="Ge_element : 3"  # scripted group (container) (typed FeaturePython)
  n = 3
  ref = Ge_element
FEATURE [App::DocumentObjectGroupPython] O_element012  label="O_element : 12"  # scripted group (container) (typed FeaturePython)
  n = 12
  ref = O_element
FEATURE [App::DocumentObjectGroupPython] G4_BGO  # scripted group (container) (typed FeaturePython)
  Dunit = g/cm3
  Dvalue = 7.13
  Group = -> [Bi_element001,Ge_element001,O_element012]
  conduct = 2
  density = 1
  expand = 3
  formula = G4_BGO
  name = G4_BGO
  specific = 4
FEATURE [App::DocumentObjectGroupPython] H_element014  label="H_element : 0.102"  # scripted group (container) (typed FeaturePython)
  n = 0.102
FEATURE [App::DocumentObjectGroupPython] C_element014  label="C_element : 0.110"  # scripted group (container) (typed FeaturePython)
  n = 0.11
FEATURE [App::DocumentObjectGroupPython] N_element009  label="N_element : 0.033"  # scripted group (container) (typed FeaturePython)
  n = 0.033
FEATURE [App::DocumentObjectGroupPython] O_element013  label="O_element : 0.745"  # scripted group (container) (typed FeaturePython)
  n = 0.745
FEATURE [App::DocumentObjectGroupPython] Na_element002  label="Na_element : 0.002"  # scripted group (container) (typed FeaturePython)
  n = 0.001
FEATURE [App::DocumentObjectGroupPython] P_element001  label="P_element : 0.001"  # scripted group (container) (typed FeaturePython)
  n = 0.001
FEATURE [App::DocumentObjectGroupPython] S_element003  label="S_element : 0.002"  # scripted group (container) (typed FeaturePython)
  n = 0.002
FEATURE [App::DocumentObjectGroupPython] Cl_element002  label="Cl_element : 0.003"  # scripted group (container) (typed FeaturePython)
  n = 0.003
FEATURE [App::DocumentObjectGroupPython] K_element001  label="K_element : 0.002"  # scripted group (container) (typed FeaturePython)
  n = 0.002
FEATURE [App::DocumentObjectGroupPython] Fe_element001  label="Fe_element : 0.001"  # scripted group (container) (typed FeaturePython)
  n = 0.001
FEATURE [App::DocumentObjectGroupPython] G4_BLOOD_ICRP  # scripted group (container) (typed FeaturePython)
  Dunit = g/cm3
  Dvalue = 1.06
  Group = -> [H_element014,C_element014,N_element009,O_element013,Na_element002,P_element001,S_element003,Cl_element002,K_element001,Fe_element001]
  conduct = 2
  density = 1
  expand = 3
  formula = G4_BLOOD_ICRP
  name = G4_BLOOD_ICRP
  specific = 4
FEATURE [App::DocumentObjectGroupPython] H_element015  label="H_element : 0.064"  # scripted group (container) (typed FeaturePython)
  n = 0.064
FEATURE [App::DocumentObjectGroupPython] C_element015  label="C_element : 0.278"  # scripted group (container) (typed FeaturePython)
  n = 0.278
FEATURE [App::DocumentObjectGroupPython] N_element010  label="N_element : 0.027"  # scripted group (container) (typed FeaturePython)
  n = 0.027
FEATURE [App::DocumentObjectGroupPython] O_element014  label="O_element : 0.410"  # scripted group (container) (typed FeaturePython)
  n = 0.41
FEATURE [App::DocumentObjectGroupPython] Mg_element001  label="Mg_element : 0.002"  # scripted group (container) (typed FeaturePython)
  n = 0.002
FEATURE [App::DocumentObjectGroupPython] P_element002  label="P_element : 0.070"  # scripted group (container) (typed FeaturePython)
  n = 0.07
FEATURE [App::DocumentObjectGroupPython] S_element004  label="S_element : 0.003"  # scripted group (container) (typed FeaturePython)
  n = 0.002
FEATURE [App::DocumentObjectGroupPython] Ca_element003  label="Ca_element : 0.147"  # scripted group (container) (typed FeaturePython)
  n = 0.147
FEATURE [App::DocumentObjectGroupPython] G4_BONE_COMPACT_ICRU  # scripted group (container) (typed FeaturePython)
  Dunit = g/cm3
  Dvalue = 1.85
  Group = -> [H_element015,C_element015,N_element010,O_element014,Mg_element001,P_element002,S_element004,Ca_element003]
  conduct = 2
  density = 1
  expand = 3
  formula = G4_BONE_COMPACT_ICRU
  name = G4_BONE_COMPACT_ICRU
  specific = 4
FEATURE [App::DocumentObjectGroupPython] H_element016  label="H_element : 0.034"  # scripted group (container) (typed FeaturePython)
  n = 0.034
FEATURE [App::DocumentObjectGroupPython] C_element016  label="C_element : 0.155"  # scripted group (container) (typed FeaturePython)
  n = 0.155
FEATURE [App::DocumentObjectGroupPython] N_element011  label="N_element : 0.042"  # scripted group (container) (typed FeaturePython)
  n = 0.042
FEATURE [App::DocumentObjectGroupPython] O_element015  label="O_element : 0.435"  # scripted group (container) (typed FeaturePython)
  n = 0.435
FEATURE [App::DocumentObjectGroupPython] Na_element003  label="Na_element : 0.003"  # scripted group (container) (typed FeaturePython)
  n = 0.001
FEATURE [App::DocumentObjectGroupPython] Mg_element002  label="Mg_element : 0.003"  # scripted group (container) (typed FeaturePython)
  n = 0.002
FEATURE [App::DocumentObjectGroupPython] P_element003  label="P_element : 0.103"  # scripted group (container) (typed FeaturePython)
  n = 0.103
FEATURE [App::DocumentObjectGroupPython] S_element005  label="S_element : 0.004"  # scripted group (container) (typed FeaturePython)
  n = 0.003
FEATURE [App::DocumentObjectGroupPython] Ca_element004  label="Ca_element : 0.225"  # scripted group (container) (typed FeaturePython)
  n = 0.225
FEATURE [App::DocumentObjectGroupPython] G4_BONE_CORTICAL_ICRP  # scripted group (container) (typed FeaturePython)
  Dunit = g/cm3
  Dvalue = 1.92
  Group = -> [H_element016,C_element016,N_element011,O_element015,Na_element003,Mg_element002,P_element003,S_element005,Ca_element004]
  conduct = 2
  density = 1
  expand = 3
  formula = G4_BONE_CORTICAL_ICRP
  name = G4_BONE_CORTICAL_ICRP
  specific = 4
FEATURE [App::DocumentObjectGroupPython] B_element001  label="B_element : 4"  # scripted group (container) (typed FeaturePython)
  n = 4
  ref = B_element
FEATURE [App::DocumentObjectGroupPython] C_element017  label="C_element : 1"  # scripted group (container) (typed FeaturePython)
  n = 1
  ref = C_element
FEATURE [App::DocumentObjectGroupPython] G4_BORON_CARBIDE  # scripted group (container) (typed FeaturePython)
  Dunit = g/cm3
  Dvalue = 2.52
  Group = -> [B_element001,C_element017]
  conduct = 2
  density = 1
  expand = 3
  formula = G4_BORON_CARBIDE
  name = G4_BORON_CARBIDE
  specific = 4
FEATURE [App::DocumentObjectGroupPython] B_element002  label="B_element : 2"  # scripted group (container) (typed FeaturePython)
  n = 2
  ref = B_element
FEATURE [App::DocumentObjectGroupPython] O_element016  label="O_element : 006"  # scripted group (container) (typed FeaturePython)
  n = 3
  ref = O_element
FEATURE [App::DocumentObjectGroupPython] G4_BORON_OXIDE  # scripted group (container) (typed FeaturePython)
  Dunit = g/cm3
  Dvalue = 1.812
  Group = -> [B_element002,O_element016]
  conduct = 2
  density = 1
  expand = 3
  formula = G4_BORON_OXIDE
  name = G4_BORON_OXIDE
  specific = 4
FEATURE [App::DocumentObjectGroupPython] H_element017  label="H_element : 0.107"  # scripted group (container) (typed FeaturePython)
  n = 0.107
FEATURE [App::DocumentObjectGroupPython] C_element018  label="C_element : 0.145"  # scripted group (container) (typed FeaturePython)
  n = 0.145
FEATURE [App::DocumentObjectGroupPython] N_element012  label="N_element : 0.022"  # scripted group (container) (typed FeaturePython)
  n = 0.022
FEATURE [App::DocumentObjectGroupPython] O_element017  label="O_element : 0.712"  # scripted group (container) (typed FeaturePython)
  n = 0.712
FEATURE [App::DocumentObjectGroupPython] Na_element004  label="Na_element : 0.004"  # scripted group (container) (typed FeaturePython)
  n = 0.002
FEATURE [App::DocumentObjectGroupPython] P_element004  label="P_element : 0.004"  # scripted group (container) (typed FeaturePython)
  n = 0.004
FEATURE [App::DocumentObjectGroupPython] S_element006  label="S_element : 0.005"  # scripted group (container) (typed FeaturePython)
  n = 0.002
FEATURE [App::DocumentObjectGroupPython] Cl_element003  label="Cl_element : 0.004"  # scripted group (container) (typed FeaturePython)
  n = 0.003
FEATURE [App::DocumentObjectGroupPython] K_element002  label="K_element : 0.003"  # scripted group (container) (typed FeaturePython)
  n = 0.003
FEATURE [App::DocumentObjectGroupPython] G4_BRAIN_ICRP  # scripted group (container) (typed FeaturePython)
  Dunit = g/cm3
  Dvalue = 1.04
  Group = -> [H_element017,C_element018,N_element012,O_element017,Na_element004,P_element004,S_element006,Cl_element003,K_element002]
  conduct = 2
  density = 1
  expand = 3
  formula = G4_BRAIN_ICRP
  name = G4_BRAIN_ICRP
  specific = 4
FEATURE [App::DocumentObjectGroupPython] C_element019  label="C_element : 4"  # scripted group (container) (typed FeaturePython)
  n = 4
  ref = C_element
FEATURE [App::DocumentObjectGroupPython] H_element018  label="H_element : 010"  # scripted group (container) (typed FeaturePython)
  n = 10
  ref = H_element
FEATURE [App::DocumentObjectGroupPython] G4_BUTANE  # scripted group (container) (typed FeaturePython)
  Dunit = g/cm3
  Dvalue = 0.00249343
  Group = -> [C_element019,H_element018]
  conduct = 2
  density = 1
  expand = 3
  formula = G4_BUTANE
  name = G4_BUTANE
  specific = 4
FEATURE [App::DocumentObjectGroupPython] C_element020  label="C_element : 008"  # scripted group (container) (typed FeaturePython)
  n = 4
  ref = C_element
FEATURE [App::DocumentObjectGroupPython] H_element019  label="H_element : 011"  # scripted group (container) (typed FeaturePython)
  n = 10
  ref = H_element
FEATURE [App::DocumentObjectGroupPython] O_element018  label="O_element : 007"  # scripted group (container) (typed FeaturePython)
  n = 1
  ref = O_element
FEATURE [App::DocumentObjectGroupPython] G4_N_BUTYL_ALCOHOL  label="G4_N-BUTYL_ALCOHOL"  # scripted group (container) (typed FeaturePython)
  Dunit = g/cm3
  Dvalue = 0.8098
  Group = -> [C_element020,H_element019,O_element018]
  conduct = 2
  density = 1
  expand = 3
  formula = G4_N-BUTYL_ALCOHOL
  name = G4_N-BUTYL_ALCOHOL
  specific = 4
FEATURE [App::DocumentObjectGroupPython] H_element020  label="H_element : 0.025"  # scripted group (container) (typed FeaturePython)
  n = 0.02468
FEATURE [App::DocumentObjectGroupPython] C_element021  label="C_element : 0.502"  # scripted group (container) (typed FeaturePython)
  n = 0.501611
FEATURE [App::DocumentObjectGroupPython] O_element019  label="O_element : 0.005"  # scripted group (container) (typed FeaturePython)
  n = 0.004527
FEATURE [App::DocumentObjectGroupPython] F_element004  label="F_element : 0.465"  # scripted group (container) (typed FeaturePython)
  n = 0.465209
FEATURE [App::DocumentObjectGroupPython] Si_element001  label="Si_element : 0.004"  # scripted group (container) (typed FeaturePython)
  n = 0.003973
FEATURE [App::DocumentObjectGroupPython] G4_C_552  label="G4_C-552"  # scripted group (container) (typed FeaturePython)
  Dunit = g/cm3
  Dvalue = 1.76
  Group = -> [H_element020,C_element021,O_element019,F_element004,Si_element001]
  conduct = 2
  density = 1
  expand = 3
  formula = G4_C-552
  name = G4_C-552
  specific = 4
FEATURE [App::DocumentObjectGroupPython] Cd_element001  label="Cd_element : 1"  # scripted group (container) (typed FeaturePython)
  n = 1
  ref = Cd_element
FEATURE [App::DocumentObjectGroupPython] Te_element001  label="Te_element : 1"  # scripted group (container) (typed FeaturePython)
  n = 1
  ref = Te_element
FEATURE [App::DocumentObjectGroupPython] G4_CADMIUM_TELLURIDE  # scripted group (container) (typed FeaturePython)
  Dunit = g/cm3
  Dvalue = 6.2
  Group = -> [Cd_element001,Te_element001]
  conduct = 2
  density = 1
  expand = 3
  formula = G4_CADMIUM_TELLURIDE
  name = G4_CADMIUM_TELLURIDE
  specific = 4
FEATURE [App::DocumentObjectGroupPython] Cd_element002  label="Cd_element : 002"  # scripted group (container) (typed FeaturePython)
  n = 1
  ref = Cd_element
FEATURE [App::DocumentObjectGroupPython] W_element001  label="W_element : 1"  # scripted group (container) (typed FeaturePython)
  n = 1
  ref = W_element
FEATURE [App::DocumentObjectGroupPython] O_element020  label="O_element : 008"  # scripted group (container) (typed FeaturePython)
  n = 4
  ref = O_element
FEATURE [App::DocumentObjectGroupPython] G4_CADMIUM_TUNGSTATE  # scripted group (container) (typed FeaturePython)
  Dunit = g/cm3
  Dvalue = 7.9
  Group = -> [Cd_element002,W_element001,O_element020]
  conduct = 2
  density = 1
  expand = 3
  formula = G4_CADMIUM_TUNGSTATE
  name = G4_CADMIUM_TUNGSTATE
  specific = 4
FEATURE [App::DocumentObjectGroupPython] Ca_element005  label="Ca_element : 1"  # scripted group (container) (typed FeaturePython)
  n = 1
  ref = Ca_element
FEATURE [App::DocumentObjectGroupPython] C_element022  label="C_element : 009"  # scripted group (container) (typed FeaturePython)
  n = 1
  ref = C_element
FEATURE [App::DocumentObjectGroupPython] O_element021  label="O_element : 009"  # scripted group (container) (typed FeaturePython)
  n = 3
  ref = O_element
FEATURE [App::DocumentObjectGroupPython] G4_CALCIUM_CARBONATE  # scripted group (container) (typed FeaturePython)
  Dunit = g/cm3
  Dvalue = 2.8
  Group = -> [Ca_element005,C_element022,O_element021]
  conduct = 2
  density = 1
  expand = 3
  formula = G4_CALCIUM_CARBONATE
  name = G4_CALCIUM_CARBONATE
  specific = 4
FEATURE [App::DocumentObjectGroupPython] Ca_element006  label="Ca_element : 002"  # scripted group (container) (typed FeaturePython)
  n = 1
  ref = Ca_element
FEATURE [App::DocumentObjectGroupPython] F_element005  label="F_element : 003"  # scripted group (container) (typed FeaturePython)
  n = 2
  ref = F_element
FEATURE [App::DocumentObjectGroupPython] G4_CALCIUM_FLUORIDE  # scripted group (container) (typed FeaturePython)
  Dunit = g/cm3
  Dvalue = 3.18
  Group = -> [Ca_element006,F_element005]
  conduct = 2
  density = 1
  expand = 3
  formula = G4_CALCIUM_FLUORIDE
  name = G4_CALCIUM_FLUORIDE
  specific = 4
FEATURE [App::DocumentObjectGroupPython] Ca_element007  label="Ca_element : 003"  # scripted group (container) (typed FeaturePython)
  n = 1
  ref = Ca_element
FEATURE [App::DocumentObjectGroupPython] O_element022  label="O_element : 010"  # scripted group (container) (typed FeaturePython)
  n = 1
  ref = O_element
FEATURE [App::DocumentObjectGroupPython] G4_CALCIUM_OXIDE  # scripted group (container) (typed FeaturePython)
  Dunit = g/cm3
  Dvalue = 3.3
  Group = -> [Ca_element007,O_element022]
  conduct = 2
  density = 1
  expand = 3
  formula = G4_CALCIUM_OXIDE
  name = G4_CALCIUM_OXIDE
  specific = 4
FEATURE [App::DocumentObjectGroupPython] Ca_element008  label="Ca_element : 004"  # scripted group (container) (typed FeaturePython)
  n = 1
  ref = Ca_element
FEATURE [App::DocumentObjectGroupPython] S_element007  label="S_element : 002"  # scripted group (container) (typed FeaturePython)
  n = 1
  ref = S_element
FEATURE [App::DocumentObjectGroupPython] O_element023  label="O_element : 011"  # scripted group (container) (typed FeaturePython)
  n = 4
  ref = O_element
FEATURE [App::DocumentObjectGroupPython] G4_CALCIUM_SULFATE  # scripted group (container) (typed FeaturePython)
  Dunit = g/cm3
  Dvalue = 2.96
  Group = -> [Ca_element008,S_element007,O_element023]
  conduct = 2
  density = 1
  expand = 3
  formula = G4_CALCIUM_SULFATE
  name = G4_CALCIUM_SULFATE
  specific = 4
FEATURE [App::DocumentObjectGroupPython] Ca_element009  label="Ca_element : 005"  # scripted group (container) (typed FeaturePython)
  n = 1
  ref = Ca_element
FEATURE [App::DocumentObjectGroupPython] W_element002  label="W_element : 002"  # scripted group (container) (typed FeaturePython)
  n = 1
  ref = W_element
FEATURE [App::DocumentObjectGroupPython] O_element024  label="O_element : 012"  # scripted group (container) (typed FeaturePython)
  n = 4
  ref = O_element
FEATURE [App::DocumentObjectGroupPython] G4_CALCIUM_TUNGSTATE  # scripted group (container) (typed FeaturePython)
  Dunit = g/cm3
  Dvalue = 6.062
  Group = -> [Ca_element009,W_element002,O_element024]
  conduct = 2
  density = 1
  expand = 3
  formula = G4_CALCIUM_TUNGSTATE
  name = G4_CALCIUM_TUNGSTATE
  specific = 4
FEATURE [App::DocumentObjectGroupPython] C_element023  label="C_element : 010"  # scripted group (container) (typed FeaturePython)
  n = 1
  ref = C_element
FEATURE [App::DocumentObjectGroupPython] O_element025  label="O_element : 013"  # scripted group (container) (typed FeaturePython)
  n = 2
  ref = O_element
FEATURE [App::DocumentObjectGroupPython] G4_CARBON_DIOXIDE  # scripted group (container) (typed FeaturePython)
  Dunit = g/cm3
  Dvalue = 0.00184212
  Group = -> [C_element023,O_element025]
  conduct = 2
  density = 1
  expand = 3
  formula = G4_CARBON_DIOXIDE
  name = G4_CARBON_DIOXIDE
  specific = 4
FEATURE [App::DocumentObjectGroupPython] C_element024  label="C_element : 011"  # scripted group (container) (typed FeaturePython)
  n = 1
  ref = C_element
FEATURE [App::DocumentObjectGroupPython] Cl_element004  label="Cl_element : 4"  # scripted group (container) (typed FeaturePython)
  n = 4
  ref = Cl_element
FEATURE [App::DocumentObjectGroupPython] G4_CARBON_TETRACHLORIDE  # scripted group (container) (typed FeaturePython)
  Dunit = g/cm3
  Dvalue = 1.594
  Group = -> [C_element024,Cl_element004]
  conduct = 2
  density = 1
  expand = 3
  formula = G4_CARBON_TETRACHLORIDE
  name = G4_CARBON_TETRACHLORIDE
  specific = 4
FEATURE [App::DocumentObjectGroupPython] C_element025  label="C_element : 012"  # scripted group (container) (typed FeaturePython)
  n = 6
  ref = C_element
FEATURE [App::DocumentObjectGroupPython] H_element021  label="H_element : 012"  # scripted group (container) (typed FeaturePython)
  n = 10
  ref = H_element
FEATURE [App::DocumentObjectGroupPython] O_element026  label="O_element : 5"  # scripted group (container) (typed FeaturePython)
  n = 5
  ref = O_element
FEATURE [App::DocumentObjectGroupPython] G4_CELLULOSE_CELLOPHANE  # scripted group (container) (typed FeaturePython)
  Dunit = g/cm3
  Dvalue = 1.42
  Group = -> [C_element025,H_element021,O_element026]
  conduct = 2
  density = 1
  expand = 3
  formula = G4_CELLULOSE_CELLOPHANE
  name = G4_CELLULOSE_CELLOPHANE
  specific = 4
FEATURE [App::DocumentObjectGroupPython] H_element022  label="H_element : 0.067"  # scripted group (container) (typed FeaturePython)
  n = 0.067125
FEATURE [App::DocumentObjectGroupPython] C_element026  label="C_element : 0.545"  # scripted group (container) (typed FeaturePython)
  n = 0.545403
FEATURE [App::DocumentObjectGroupPython] O_element027  label="O_element : 0.387"  # scripted group (container) (typed FeaturePython)
  n = 0.387472
FEATURE [App::DocumentObjectGroupPython] G4_CELLULOSE_BUTYRATE  # scripted group (container) (typed FeaturePython)
  Dunit = g/cm3
  Dvalue = 1.2
  Group = -> [H_element022,C_element026,O_element027]
  conduct = 2
  density = 1
  expand = 3
  formula = G4_CELLULOSE_BUTYRATE
  name = G4_CELLULOSE_BUTYRATE
  specific = 4
FEATURE [App::DocumentObjectGroupPython] H_element023  label="H_element : 0.029"  # scripted group (container) (typed FeaturePython)
  n = 0.029216
FEATURE [App::DocumentObjectGroupPython] C_element027  label="C_element : 0.271"  # scripted group (container) (typed FeaturePython)
  n = 0.271296
FEATURE [App::DocumentObjectGroupPython] N_element013  label="N_element : 0.121"  # scripted group (container) (typed FeaturePython)
  n = 0.121276
FEATURE [App::DocumentObjectGroupPython] O_element028  label="O_element : 0.578"  # scripted group (container) (typed FeaturePython)
  n = 0.578212
FEATURE [App::DocumentObjectGroupPython] G4_CELLULOSE_NITRATE  # scripted group (container) (typed FeaturePython)
  Dunit = g/cm3
  Dvalue = 1.49
  Group = -> [H_element023,C_element027,N_element013,O_element028]
  conduct = 2
  density = 1
  expand = 3
  formula = G4_CELLULOSE_NITRATE
  name = G4_CELLULOSE_NITRATE
  specific = 4
FEATURE [App::DocumentObjectGroupPython] H_element024  label="H_element : 0.108"  # scripted group (container) (typed FeaturePython)
  n = 0.107596
FEATURE [App::DocumentObjectGroupPython] N_element014  label="N_element : 0.001"  # scripted group (container) (typed FeaturePython)
  n = 0.0008
FEATURE [App::DocumentObjectGroupPython] O_element029  label="O_element : 0.875"  # scripted group (container) (typed FeaturePython)
  n = 0.874976
FEATURE [App::DocumentObjectGroupPython] S_element008  label="S_element : 0.015"  # scripted group (container) (typed FeaturePython)
  n = 0.014627
FEATURE [App::DocumentObjectGroupPython] Ce_element001  label="Ce_element : 0.002"  # scripted group (container) (typed FeaturePython)
  n = 0.002001
FEATURE [App::DocumentObjectGroupPython] G4_CERIC_SULFATE  # scripted group (container) (typed FeaturePython)
  Dunit = g/cm3
  Dvalue = 1.03
  Group = -> [H_element024,N_element014,O_element029,S_element008,Ce_element001]
  conduct = 2
  density = 1
  expand = 3
  formula = G4_CERIC_SULFATE
  name = G4_CERIC_SULFATE
  specific = 4
FEATURE [App::DocumentObjectGroupPython] Cs_element001  label="Cs_element : 1"  # scripted group (container) (typed FeaturePython)
  n = 1
  ref = Cs_element
FEATURE [App::DocumentObjectGroupPython] F_element006  label="F_element : 1"  # scripted group (container) (typed FeaturePython)
  n = 1
  ref = F_element
FEATURE [App::DocumentObjectGroupPython] G4_CESIUM_FLUORIDE  # scripted group (container) (typed FeaturePython)
  Dunit = g/cm3
  Dvalue = 4.115
  Group = -> [Cs_element001,F_element006]
  conduct = 2
  density = 1
  expand = 3
  formula = G4_CESIUM_FLUORIDE
  name = G4_CESIUM_FLUORIDE
  specific = 4
FEATURE [App::DocumentObjectGroupPython] Cs_element002  label="Cs_element : 002"  # scripted group (container) (typed FeaturePython)
  n = 1
  ref = Cs_element
FEATURE [App::DocumentObjectGroupPython] I_element001  label="I_element : 1"  # scripted group (container) (typed FeaturePython)
  n = 1
  ref = I_element
FEATURE [App::DocumentObjectGroupPython] G4_CESIUM_IODIDE  # scripted group (container) (typed FeaturePython)
  Dunit = g/cm3
  Dvalue = 4.51
  Group = -> [Cs_element002,I_element001]
  conduct = 2
  density = 1
  expand = 3
  formula = G4_CESIUM_IODIDE
  name = G4_CESIUM_IODIDE
  specific = 4
FEATURE [App::DocumentObjectGroupPython] C_element028  label="C_element : 013"  # scripted group (container) (typed FeaturePython)
  n = 6
  ref = C_element
FEATURE [App::DocumentObjectGroupPython] H_element025  label="H_element : 013"  # scripted group (container) (typed FeaturePython)
  n = 5
  ref = H_element
FEATURE [App::DocumentObjectGroupPython] Cl_element005  label="Cl_element : 1"  # scripted group (container) (typed FeaturePython)
  n = 1
  ref = Cl_element
FEATURE [App::DocumentObjectGroupPython] G4_CHLOROBENZENE  # scripted group (container) (typed FeaturePython)
  Dunit = g/cm3
  Dvalue = 1.1058
  Group = -> [C_element028,H_element025,Cl_element005]
  conduct = 2
  density = 1
  expand = 3
  formula = G4_CHLOROBENZENE
  name = G4_CHLOROBENZENE
  specific = 4
FEATURE [App::DocumentObjectGroupPython] C_element029  label="C_element : 014"  # scripted group (container) (typed FeaturePython)
  n = 1
  ref = C_element
FEATURE [App::DocumentObjectGroupPython] H_element026  label="H_element : 1"  # scripted group (container) (typed FeaturePython)
  n = 1
  ref = H_element
FEATURE [App::DocumentObjectGroupPython] Cl_element006  label="Cl_element : 3"  # scripted group (container) (typed FeaturePython)
  n = 3
  ref = Cl_element
FEATURE [App::DocumentObjectGroupPython] G4_CHLOROFORM  # scripted group (container) (typed FeaturePython)
  Dunit = g/cm3
  Dvalue = 1.4832
  Group = -> [C_element029,H_element026,Cl_element006]
  conduct = 2
  density = 1
  expand = 3
  formula = G4_CHLOROFORM
  name = G4_CHLOROFORM
  specific = 4
FEATURE [App::DocumentObjectGroupPython] H_element027  label="H_element : 0.010"  # scripted group (container) (typed FeaturePython)
  n = 0.01
FEATURE [App::DocumentObjectGroupPython] C_element030  label="C_element : 0.001"  # scripted group (container) (typed FeaturePython)
  n = 0.001
FEATURE [App::DocumentObjectGroupPython] O_element030  label="O_element : 0.529"  # scripted group (container) (typed FeaturePython)
  n = 0.529107
FEATURE [App::DocumentObjectGroupPython] Na_element005  label="Na_element : 0.016"  # scripted group (container) (typed FeaturePython)
  n = 0.016
FEATURE [App::DocumentObjectGroupPython] Mg_element003  label="Mg_element : 0.004"  # scripted group (container) (typed FeaturePython)
  n = 0.002
FEATURE [App::DocumentObjectGroupPython] Al_element002  label="Al_element : 0.034"  # scripted group (container) (typed FeaturePython)
  n = 0.033872
FEATURE [App::DocumentObjectGroupPython] Si_element002  label="Si_element : 0.337"  # scripted group (container) (typed FeaturePython)
  n = 0.337021
FEATURE [App::DocumentObjectGroupPython] K_element003  label="K_element : 0.013"  # scripted group (container) (typed FeaturePython)
  n = 0.013
FEATURE [App::DocumentObjectGroupPython] Ca_element010  label="Ca_element : 0.044"  # scripted group (container) (typed FeaturePython)
  n = 0.044
FEATURE [App::DocumentObjectGroupPython] Fe_element002  label="Fe_element : 0.014"  # scripted group (container) (typed FeaturePython)
  n = 0.014
FEATURE [App::DocumentObjectGroupPython] G4_CONCRETE  # scripted group (container) (typed FeaturePython)
  Dunit = g/cm3
  Dvalue = 2.3
  Group = -> [H_element027,C_element030,O_element030,Na_element005,Mg_element003,Al_element002,Si_element002,K_element003,Ca_element010,Fe_element002]
  conduct = 2
  density = 1
  expand = 3
  formula = G4_CONCRETE
  name = G4_CONCRETE
  specific = 4
FEATURE [App::DocumentObjectGroupPython] C_element031  label="C_element : 015"  # scripted group (container) (typed FeaturePython)
  n = 6
  ref = C_element
FEATURE [App::DocumentObjectGroupPython] H_element028  label="H_element : 12"  # scripted group (container) (typed FeaturePython)
  n = 12
  ref = H_element
FEATURE [App::DocumentObjectGroupPython] G4_CYCLOHEXANE  # scripted group (container) (typed FeaturePython)
  Dunit = g/cm3
  Dvalue = 0.779
  Group = -> [C_element031,H_element028]
  conduct = 2
  density = 1
  expand = 3
  formula = G4_CYCLOHEXANE
  name = G4_CYCLOHEXANE
  specific = 4
FEATURE [App::DocumentObjectGroupPython] C_element032  label="C_element : 016"  # scripted group (container) (typed FeaturePython)
  n = 6
  ref = C_element
FEATURE [App::DocumentObjectGroupPython] H_element029  label="H_element : 4"  # scripted group (container) (typed FeaturePython)
  n = 4
  ref = H_element
FEATURE [App::DocumentObjectGroupPython] Cl_element007  label="Cl_element : 2"  # scripted group (container) (typed FeaturePython)
  n = 2
  ref = Cl_element
FEATURE [App::DocumentObjectGroupPython] G4_1_2_DICHLOROBENZENE  label="G4_1.2-DICHLOROBENZENE"  # scripted group (container) (typed FeaturePython)
  Dunit = g/cm3
  Dvalue = 1.3048
  Group = -> [C_element032,H_element029,Cl_element007]
  conduct = 2
  density = 1
  expand = 3
  formula = G4_1.2-DICHLOROBENZENE
  name = G4_1.2-DICHLOROBENZENE
  specific = 4
FEATURE [App::DocumentObjectGroupPython] C_element033  label="C_element : 017"  # scripted group (container) (typed FeaturePython)
  n = 4
  ref = C_element
FEATURE [App::DocumentObjectGroupPython] H_element030  label="H_element : 8"  # scripted group (container) (typed FeaturePython)
  n = 8
  ref = H_element
FEATURE [App::DocumentObjectGroupPython] O_element031  label="O_element : 014"  # scripted group (container) (typed FeaturePython)
  n = 1
  ref = O_element
FEATURE [App::DocumentObjectGroupPython] Cl_element008  label="Cl_element : 005"  # scripted group (container) (typed FeaturePython)
  n = 2
  ref = Cl_element
FEATURE [App::DocumentObjectGroupPython] G4_DICHLORODIETHYL_ETHER  # scripted group (container) (typed FeaturePython)
  Dunit = g/cm3
  Dvalue = 1.2199
  Group = -> [C_element033,H_element030,O_element031,Cl_element008]
  conduct = 2
  density = 1
  expand = 3
  formula = G4_DICHLORODIETHYL_ETHER
  name = G4_DICHLORODIETHYL_ETHER
  specific = 4
FEATURE [App::DocumentObjectGroupPython] C_element034  label="C_element : 018"  # scripted group (container) (typed FeaturePython)
  n = 2
  ref = C_element
FEATURE [App::DocumentObjectGroupPython] H_element031  label="H_element : 014"  # scripted group (container) (typed FeaturePython)
  n = 4
  ref = H_element
FEATURE [App::DocumentObjectGroupPython] Cl_element009  label="Cl_element : 006"  # scripted group (container) (typed FeaturePython)
  n = 2
  ref = Cl_element
FEATURE [App::DocumentObjectGroupPython] G4_1_2_DICHLOROETHANE  label="G4_1.2-DICHLOROETHANE"  # scripted group (container) (typed FeaturePython)
  Dunit = g/cm3
  Dvalue = 1.2351
  Group = -> [C_element034,H_element031,Cl_element009]
  conduct = 2
  density = 1
  expand = 3
  formula = G4_1.2-DICHLOROETHANE
  name = G4_1.2-DICHLOROETHANE
  specific = 4
FEATURE [App::DocumentObjectGroupPython] C_element035  label="C_element : 019"  # scripted group (container) (typed FeaturePython)
  n = 4
  ref = C_element
FEATURE [App::DocumentObjectGroupPython] H_element032  label="H_element : 015"  # scripted group (container) (typed FeaturePython)
  n = 10
  ref = H_element
FEATURE [App::DocumentObjectGroupPython] O_element032  label="O_element : 015"  # scripted group (container) (typed FeaturePython)
  n = 1
  ref = O_element
FEATURE [App::DocumentObjectGroupPython] G4_DIETHYL_ETHER  # scripted group (container) (typed FeaturePython)
  Dunit = g/cm3
  Dvalue = 0.71378
  Group = -> [C_element035,H_element032,O_element032]
  conduct = 2
  density = 1
  expand = 3
  formula = G4_DIETHYL_ETHER
  name = G4_DIETHYL_ETHER
  specific = 4
FEATURE [App::DocumentObjectGroupPython] C_element036  label="C_element : 020"  # scripted group (container) (typed FeaturePython)
  n = 3
  ref = C_element
FEATURE [App::DocumentObjectGroupPython] H_element033  label="H_element : 016"  # scripted group (container) (typed FeaturePython)
  n = 7
  ref = H_element
FEATURE [App::DocumentObjectGroupPython] N_element015  label="N_element : 008"  # scripted group (container) (typed FeaturePython)
  n = 1
  ref = N_element
FEATURE [App::DocumentObjectGroupPython] O_element033  label="O_element : 016"  # scripted group (container) (typed FeaturePython)
  n = 1
  ref = O_element
FEATURE [App::DocumentObjectGroupPython] G4_N_N_DIMETHYL_FORMAMIDE  label="G4_N.N-DIMETHYL_FORMAMIDE"  # scripted group (container) (typed FeaturePython)
  Dunit = g/cm3
  Dvalue = 0.9487
  Group = -> [C_element036,H_element033,N_element015,O_element033]
  conduct = 2
  density = 1
  expand = 3
  formula = G4_N.N-DIMETHYL_FORMAMIDE
  name = G4_N.N-DIMETHYL_FORMAMIDE
  specific = 4
FEATURE [App::DocumentObjectGroupPython] C_element037  label="C_element : 021"  # scripted group (container) (typed FeaturePython)
  n = 2
  ref = C_element
FEATURE [App::DocumentObjectGroupPython] H_element034  label="H_element : 017"  # scripted group (container) (typed FeaturePython)
  n = 6
  ref = H_element
FEATURE [App::DocumentObjectGroupPython] O_element034  label="O_element : 017"  # scripted group (container) (typed FeaturePython)
  n = 1
  ref = O_element
FEATURE [App::DocumentObjectGroupPython] S_element009  label="S_element : 003"  # scripted group (container) (typed FeaturePython)
  n = 1
  ref = S_element
FEATURE [App::DocumentObjectGroupPython] G4_DIMETHYL_SULFOXIDE  # scripted group (container) (typed FeaturePython)
  Dunit = g/cm3
  Dvalue = 1.1014
  Group = -> [C_element037,H_element034,O_element034,S_element009]
  conduct = 2
  density = 1
  expand = 3
  formula = G4_DIMETHYL_SULFOXIDE
  name = G4_DIMETHYL_SULFOXIDE
  specific = 4
FEATURE [App::DocumentObjectGroupPython] C_element038  label="C_element : 022"  # scripted group (container) (typed FeaturePython)
  n = 2
  ref = C_element
FEATURE [App::DocumentObjectGroupPython] H_element035  label="H_element : 018"  # scripted group (container) (typed FeaturePython)
  n = 6
  ref = H_element
FEATURE [App::DocumentObjectGroupPython] G4_ETHANE  # scripted group (container) (typed FeaturePython)
  Dunit = g/cm3
  Dvalue = 0.00125324
  Group = -> [C_element038,H_element035]
  conduct = 2
  density = 1
  expand = 3
  formula = G4_ETHANE
  name = G4_ETHANE
  specific = 4
FEATURE [App::DocumentObjectGroupPython] C_element039  label="C_element : 023"  # scripted group (container) (typed FeaturePython)
  n = 2
  ref = C_element
FEATURE [App::DocumentObjectGroupPython] H_element036  label="H_element : 019"  # scripted group (container) (typed FeaturePython)
  n = 6
  ref = H_element
FEATURE [App::DocumentObjectGroupPython] O_element035  label="O_element : 018"  # scripted group (container) (typed FeaturePython)
  n = 1
  ref = O_element
FEATURE [App::DocumentObjectGroupPython] G4_ETHYL_ALCOHOL  # scripted group (container) (typed FeaturePython)
  Dunit = g/cm3
  Dvalue = 0.7893
  Group = -> [C_element039,H_element036,O_element035]
  conduct = 2
  density = 1
  expand = 3
  formula = G4_ETHYL_ALCOHOL
  name = G4_ETHYL_ALCOHOL
  specific = 4
FEATURE [App::DocumentObjectGroupPython] H_element037  label="H_element : 0.090"  # scripted group (container) (typed FeaturePython)
  n = 0.090027
FEATURE [App::DocumentObjectGroupPython] C_element040  label="C_element : 0.585"  # scripted group (container) (typed FeaturePython)
  n = 0.585182
FEATURE [App::DocumentObjectGroupPython] O_element036  label="O_element : 0.325"  # scripted group (container) (typed FeaturePython)
  n = 0.324791
FEATURE [App::DocumentObjectGroupPython] G4_ETHYL_CELLULOSE  # scripted group (container) (typed FeaturePython)
  Dunit = g/cm3
  Dvalue = 1.13
  Group = -> [H_element037,C_element040,O_element036]
  conduct = 2
  density = 1
  expand = 3
  formula = G4_ETHYL_CELLULOSE
  name = G4_ETHYL_CELLULOSE
  specific = 4
FEATURE [App::DocumentObjectGroupPython] C_element041  label="C_element : 024"  # scripted group (container) (typed FeaturePython)
  n = 2
  ref = C_element
FEATURE [App::DocumentObjectGroupPython] H_element038  label="H_element : 020"  # scripted group (container) (typed FeaturePython)
  n = 4
  ref = H_element
FEATURE [App::DocumentObjectGroupPython] G4_ETHYLENE  # scripted group (container) (typed FeaturePython)
  Dunit = g/cm3
  Dvalue = 0.00117497
  Group = -> [C_element041,H_element038]
  conduct = 2
  density = 1
  expand = 3
  formula = G4_ETHYLENE
  name = G4_ETHYLENE
  specific = 4
FEATURE [App::DocumentObjectGroupPython] H_element039  label="H_element : 0.096"  # scripted group (container) (typed FeaturePython)
  n = 0.096
FEATURE [App::DocumentObjectGroupPython] C_element042  label="C_element : 0.195"  # scripted group (container) (typed FeaturePython)
  n = 0.195
FEATURE [App::DocumentObjectGroupPython] N_element016  label="N_element : 0.057"  # scripted group (container) (typed FeaturePython)
  n = 0.057
FEATURE [App::DocumentObjectGroupPython] O_element037  label="O_element : 0.646"  # scripted group (container) (typed FeaturePython)
  n = 0.646
FEATURE [App::DocumentObjectGroupPython] Na_element006  label="Na_element : 0.017"  # scripted group (container) (typed FeaturePython)
  n = 0.001
FEATURE [App::DocumentObjectGroupPython] P_element005  label="P_element : 0.104"  # scripted group (container) (typed FeaturePython)
  n = 0.001
FEATURE [App::DocumentObjectGroupPython] S_element010  label="S_element : 0.016"  # scripted group (container) (typed FeaturePython)
  n = 0.003
FEATURE [App::DocumentObjectGroupPython] Cl_element010  label="Cl_element : 0.005"  # scripted group (container) (typed FeaturePython)
  n = 0.001
FEATURE [App::DocumentObjectGroupPython] G4_EYE_LENS_ICRP  # scripted group (container) (typed FeaturePython)
  Dunit = g/cm3
  Dvalue = 1.07
  Group = -> [H_element039,C_element042,N_element016,O_element037,Na_element006,P_element005,S_element010,Cl_element010]
  conduct = 2
  density = 1
  expand = 3
  formula = G4_EYE_LENS_ICRP
  name = G4_EYE_LENS_ICRP
  specific = 4
FEATURE [App::DocumentObjectGroupPython] Fe_element003  label="Fe_element : 2"  # scripted group (container) (typed FeaturePython)
  n = 2
  ref = Fe_element
FEATURE [App::DocumentObjectGroupPython] O_element038  label="O_element : 019"  # scripted group (container) (typed FeaturePython)
  n = 3
  ref = O_element
FEATURE [App::DocumentObjectGroupPython] G4_FERRIC_OXIDE  # scripted group (container) (typed FeaturePython)
  Dunit = g/cm3
  Dvalue = 5.2
  Group = -> [Fe_element003,O_element038]
  conduct = 2
  density = 1
  expand = 3
  formula = G4_FERRIC_OXIDE
  name = G4_FERRIC_OXIDE
  specific = 4
FEATURE [App::DocumentObjectGroupPython] Fe_element004  label="Fe_element : 1"  # scripted group (container) (typed FeaturePython)
  n = 1
  ref = Fe_element
FEATURE [App::DocumentObjectGroupPython] B_element003  label="B_element : 1"  # scripted group (container) (typed FeaturePython)
  n = 1
  ref = B_element
FEATURE [App::DocumentObjectGroupPython] G4_FERROBORIDE  # scripted group (container) (typed FeaturePython)
  Dunit = g/cm3
  Dvalue = 7.15
  Group = -> [Fe_element004,B_element003]
  conduct = 2
  density = 1
  expand = 3
  formula = G4_FERROBORIDE
  name = G4_FERROBORIDE
  specific = 4
FEATURE [App::DocumentObjectGroupPython] Fe_element005  label="Fe_element : 003"  # scripted group (container) (typed FeaturePython)
  n = 1
  ref = Fe_element
FEATURE [App::DocumentObjectGroupPython] O_element039  label="O_element : 020"  # scripted group (container) (typed FeaturePython)
  n = 1
  ref = O_element
FEATURE [App::DocumentObjectGroupPython] G4_FERROUS_OXIDE  # scripted group (container) (typed FeaturePython)
  Dunit = g/cm3
  Dvalue = 5.7
  Group = -> [Fe_element005,O_element039]
  conduct = 2
  density = 1
  expand = 3
  formula = G4_FERROUS_OXIDE
  name = G4_FERROUS_OXIDE
  specific = 4
FEATURE [App::DocumentObjectGroupPython] H_element040  label="H_element : 0.115"  # scripted group (container) (typed FeaturePython)
  n = 0.108259
FEATURE [App::DocumentObjectGroupPython] N_element017  label="N_element : 0.000"  # scripted group (container) (typed FeaturePython)
  n = 2.7e-05
FEATURE [App::DocumentObjectGroupPython] O_element040  label="O_element : 0.879"  # scripted group (container) (typed FeaturePython)
  n = 0.878636
FEATURE [App::DocumentObjectGroupPython] Na_element007  label="Na_element : 0.000"  # scripted group (container) (typed FeaturePython)
  n = 2.2e-05
FEATURE [App::DocumentObjectGroupPython] S_element011  label="S_element : 0.013"  # scripted group (container) (typed FeaturePython)
  n = 0.012968
FEATURE [App::DocumentObjectGroupPython] Cl_element011  label="Cl_element : 0.000"  # scripted group (container) (typed FeaturePython)
  n = 3.4e-05
FEATURE [App::DocumentObjectGroupPython] Fe_element006  label="Fe_element : 0.000"  # scripted group (container) (typed FeaturePython)
  n = 5.4e-05
FEATURE [App::DocumentObjectGroupPython] G4_FERROUS_SULFATE  # scripted group (container) (typed FeaturePython)
  Dunit = g/cm3
  Dvalue = 1.024
  Group = -> [H_element040,N_element017,O_element040,Na_element007,S_element011,Cl_element011,Fe_element006]
  conduct = 2
  density = 1
  expand = 3
  formula = G4_FERROUS_SULFATE
  name = G4_FERROUS_SULFATE
  specific = 4
FEATURE [App::DocumentObjectGroupPython] C_element043  label="C_element : 0.099"  # scripted group (container) (typed FeaturePython)
  n = 0.099335
FEATURE [App::DocumentObjectGroupPython] F_element007  label="F_element : 0.314"  # scripted group (container) (typed FeaturePython)
  n = 0.314247
FEATURE [App::DocumentObjectGroupPython] Cl_element012  label="Cl_element : 0.586"  # scripted group (container) (typed FeaturePython)
  n = 0.586418
FEATURE [App::DocumentObjectGroupPython] G4_FREON_12  label="G4_FREON-12"  # scripted group (container) (typed FeaturePython)
  Dunit = g/cm3
  Dvalue = 1.12
  Group = -> [C_element043,F_element007,Cl_element012]
  conduct = 2
  density = 1
  expand = 3
  formula = G4_FREON-12
  name = G4_FREON-12
  specific = 4
FEATURE [App::DocumentObjectGroupPython] C_element044  label="C_element : 0.057"  # scripted group (container) (typed FeaturePython)
  n = 0.057245
FEATURE [App::DocumentObjectGroupPython] F_element008  label="F_element : 0.181"  # scripted group (container) (typed FeaturePython)
  n = 0.181096
FEATURE [App::DocumentObjectGroupPython] Br_element001  label="Br_element : 0.762"  # scripted group (container) (typed FeaturePython)
  n = 0.761659
FEATURE [App::DocumentObjectGroupPython] G4_FREON_12B2  label="G4_FREON-12B2"  # scripted group (container) (typed FeaturePython)
  Dunit = g/cm3
  Dvalue = 1.8
  Group = -> [C_element044,F_element008,Br_element001]
  conduct = 2
  density = 1
  expand = 3
  formula = G4_FREON-12B2
  name = G4_FREON-12B2
  specific = 4
FEATURE [App::DocumentObjectGroupPython] C_element045  label="C_element : 0.115"  # scripted group (container) (typed FeaturePython)
  n = 0.114983
FEATURE [App::DocumentObjectGroupPython] F_element009  label="F_element : 0.546"  # scripted group (container) (typed FeaturePython)
  n = 0.545621
FEATURE [App::DocumentObjectGroupPython] Cl_element013  label="Cl_element : 0.339"  # scripted group (container) (typed FeaturePython)
  n = 0.339396
FEATURE [App::DocumentObjectGroupPython] G4_FREON_13  label="G4_FREON-13"  # scripted group (container) (typed FeaturePython)
  Dunit = g/cm3
  Dvalue = 0.95
  Group = -> [C_element045,F_element009,Cl_element013]
  conduct = 2
  density = 1
  expand = 3
  formula = G4_FREON-13
  name = G4_FREON-13
  specific = 4
FEATURE [App::DocumentObjectGroupPython] C_element046  label="C_element : 025"  # scripted group (container) (typed FeaturePython)
  n = 1
  ref = C_element
FEATURE [App::DocumentObjectGroupPython] F_element010  label="F_element : 3"  # scripted group (container) (typed FeaturePython)
  n = 3
  ref = F_element
FEATURE [App::DocumentObjectGroupPython] Br_element002  label="Br_element : 1"  # scripted group (container) (typed FeaturePython)
  n = 1
  ref = Br_element
FEATURE [App::DocumentObjectGroupPython] G4_FREON_13B1  label="G4_FREON-13B1"  # scripted group (container) (typed FeaturePython)
  Dunit = g/cm3
  Dvalue = 1.5
  Group = -> [C_element046,F_element010,Br_element002]
  conduct = 2
  density = 1
  expand = 3
  formula = G4_FREON-13B1
  name = G4_FREON-13B1
  specific = 4
FEATURE [App::DocumentObjectGroupPython] C_element047  label="C_element : 0.061"  # scripted group (container) (typed FeaturePython)
  n = 0.061309
FEATURE [App::DocumentObjectGroupPython] F_element011  label="F_element : 0.291"  # scripted group (container) (typed FeaturePython)
  n = 0.290924
FEATURE [App::DocumentObjectGroupPython] I_element002  label="I_element : 0.648"  # scripted group (container) (typed FeaturePython)
  n = 0.647767
FEATURE [App::DocumentObjectGroupPython] G4_FREON_13I1  label="G4_FREON-13I1"  # scripted group (container) (typed FeaturePython)
  Dunit = g/cm3
  Dvalue = 1.8
  Group = -> [C_element047,F_element011,I_element002]
  conduct = 2
  density = 1
  expand = 3
  formula = G4_FREON-13I1
  name = G4_FREON-13I1
  specific = 4
FEATURE [App::DocumentObjectGroupPython] Gd_element001  label="Gd_element : 2"  # scripted group (container) (typed FeaturePython)
  n = 2
  ref = Gd_element
FEATURE [App::DocumentObjectGroupPython] O_element041  label="O_element : 021"  # scripted group (container) (typed FeaturePython)
  n = 2
  ref = O_element
FEATURE [App::DocumentObjectGroupPython] S_element012  label="S_element : 004"  # scripted group (container) (typed FeaturePython)
  n = 1
  ref = S_element
FEATURE [App::DocumentObjectGroupPython] G4_GADOLINIUM_OXYSULFIDE  # scripted group (container) (typed FeaturePython)
  Dunit = g/cm3
  Dvalue = 7.44
  Group = -> [Gd_element001,O_element041,S_element012]
  conduct = 2
  density = 1
  expand = 3
  formula = G4_GADOLINIUM_OXYSULFIDE
  name = G4_GADOLINIUM_OXYSULFIDE
  specific = 4
FEATURE [App::DocumentObjectGroupPython] Ga_element001  label="Ga_element : 1"  # scripted group (container) (typed FeaturePython)
  n = 1
  ref = Ga_element
FEATURE [App::DocumentObjectGroupPython] As_element001  label="As_element : 1"  # scripted group (container) (typed FeaturePython)
  n = 1
  ref = As_element
FEATURE [App::DocumentObjectGroupPython] G4_GALLIUM_ARSENIDE  # scripted group (container) (typed FeaturePython)
  Dunit = g/cm3
  Dvalue = 5.31
  Group = -> [Ga_element001,As_element001]
  conduct = 2
  density = 1
  expand = 3
  formula = G4_GALLIUM_ARSENIDE
  name = G4_GALLIUM_ARSENIDE
  specific = 4
FEATURE [App::DocumentObjectGroupPython] H_element041  label="H_element : 0.081"  # scripted group (container) (typed FeaturePython)
  n = 0.08118
FEATURE [App::DocumentObjectGroupPython] C_element048  label="C_element : 0.416"  # scripted group (container) (typed FeaturePython)
  n = 0.41606
FEATURE [App::DocumentObjectGroupPython] N_element018  label="N_element : 0.111"  # scripted group (container) (typed FeaturePython)
  n = 0.11124
FEATURE [App::DocumentObjectGroupPython] O_element042  label="O_element : 0.381"  # scripted group (container) (typed FeaturePython)
  n = 0.38064
FEATURE [App::DocumentObjectGroupPython] S_element013  label="S_element : 0.011"  # scripted group (container) (typed FeaturePython)
  n = 0.01088
FEATURE [App::DocumentObjectGroupPython] G4_GEL_PHOTO_EMULSION  # scripted group (container) (typed FeaturePython)
  Dunit = g/cm3
  Dvalue = 1.2914
  Group = -> [H_element041,C_element048,N_element018,O_element042,S_element013]
  conduct = 2
  density = 1
  expand = 3
  formula = G4_GEL_PHOTO_EMULSION
  name = G4_GEL_PHOTO_EMULSION
  specific = 4
FEATURE [App::DocumentObjectGroupPython] B_element004  label="B_element : 0.040"  # scripted group (container) (typed FeaturePython)
  n = 0.0400639
FEATURE [App::DocumentObjectGroupPython] O_element043  label="O_element : 0.540"  # scripted group (container) (typed FeaturePython)
  n = 0.539561
FEATURE [App::DocumentObjectGroupPython] Na_element008  label="Na_element : 0.028"  # scripted group (container) (typed FeaturePython)
  n = 0.0281909
FEATURE [App::DocumentObjectGroupPython] Al_element003  label="Al_element : 0.012"  # scripted group (container) (typed FeaturePython)
  n = 0.011644
FEATURE [App::DocumentObjectGroupPython] Si_element003  label="Si_element : 0.377"  # scripted group (container) (typed FeaturePython)
  n = 0.377219
FEATURE [App::DocumentObjectGroupPython] K_element004  label="K_element : 0.014"  # scripted group (container) (typed FeaturePython)
  n = 0.00332099
FEATURE [App::DocumentObjectGroupPython] G4_Pyrex_Glass  # scripted group (container) (typed FeaturePython)
  Dunit = g/cm3
  Dvalue = 2.23
  Group = -> [B_element004,O_element043,Na_element008,Al_element003,Si_element003,K_element004]
  conduct = 2
  density = 1
  expand = 3
  formula = G4_Pyrex_Glass
  name = G4_Pyrex_Glass
  specific = 4
FEATURE [App::DocumentObjectGroupPython] O_element044  label="O_element : 0.156"  # scripted group (container) (typed FeaturePython)
  n = 0.156453
FEATURE [App::DocumentObjectGroupPython] Si_element004  label="Si_element : 0.081"  # scripted group (container) (typed FeaturePython)
  n = 0.080866
FEATURE [App::DocumentObjectGroupPython] Ti_element001  label="Ti_element : 0.008"  # scripted group (container) (typed FeaturePython)
  n = 0.008092
FEATURE [App::DocumentObjectGroupPython] As_element002  label="As_element : 0.003"  # scripted group (container) (typed FeaturePython)
  n = 0.002651
FEATURE [App::DocumentObjectGroupPython] Pb_element001  label="Pb_element : 0.752"  # scripted group (container) (typed FeaturePython)
  n = 0.751938
FEATURE [App::DocumentObjectGroupPython] G4_GLASS_LEAD  # scripted group (container) (typed FeaturePython)
  Dunit = g/cm3
  Dvalue = 6.22
  Group = -> [O_element044,Si_element004,Ti_element001,As_element002,Pb_element001]
  conduct = 2
  density = 1
  expand = 3
  formula = G4_GLASS_LEAD
  name = G4_GLASS_LEAD
  specific = 4
FEATURE [App::DocumentObjectGroupPython] O_element045  label="O_element : 0.460"  # scripted group (container) (typed FeaturePython)
  n = 0.4598
FEATURE [App::DocumentObjectGroupPython] Na_element009  label="Na_element : 0.096"  # scripted group (container) (typed FeaturePython)
  n = 0.0964411
FEATURE [App::DocumentObjectGroupPython] Si_element005  label="Si_element : 0.378"  # scripted group (container) (typed FeaturePython)
  n = 0.336553
FEATURE [App::DocumentObjectGroupPython] Ca_element011  label="Ca_element : 0.107"  # scripted group (container) (typed FeaturePython)
  n = 0.107205
FEATURE [App::DocumentObjectGroupPython] G4_GLASS_PLATE  # scripted group (container) (typed FeaturePython)
  Dunit = g/cm3
  Dvalue = 2.4
  Group = -> [O_element045,Na_element009,Si_element005,Ca_element011]
  conduct = 2
  density = 1
  expand = 3
  formula = G4_GLASS_PLATE
  name = G4_GLASS_PLATE
  specific = 4
FEATURE [App::DocumentObjectGroupPython] C_element049  label="C_element : 026"  # scripted group (container) (typed FeaturePython)
  n = 5
  ref = C_element
FEATURE [App::DocumentObjectGroupPython] H_element042  label="H_element : 021"  # scripted group (container) (typed FeaturePython)
  n = 10
  ref = H_element
FEATURE [App::DocumentObjectGroupPython] N_element019  label="N_element : 2"  # scripted group (container) (typed FeaturePython)
  n = 2
  ref = N_element
FEATURE [App::DocumentObjectGroupPython] O_element046  label="O_element : 022"  # scripted group (container) (typed FeaturePython)
  n = 3
  ref = O_element
FEATURE [App::DocumentObjectGroupPython] G4_GLUTAMINE  # scripted group (container) (typed FeaturePython)
  Dunit = g/cm3
  Dvalue = 1.46
  Group = -> [C_element049,H_element042,N_element019,O_element046]
  conduct = 2
  density = 1
  expand = 3
  formula = G4_GLUTAMINE
  name = G4_GLUTAMINE
  specific = 4
FEATURE [App::DocumentObjectGroupPython] C_element050  label="C_element : 027"  # scripted group (container) (typed FeaturePython)
  n = 3
  ref = C_element
FEATURE [App::DocumentObjectGroupPython] H_element043  label="H_element : 022"  # scripted group (container) (typed FeaturePython)
  n = 8
  ref = H_element
FEATURE [App::DocumentObjectGroupPython] O_element047  label="O_element : 023"  # scripted group (container) (typed FeaturePython)
  n = 3
  ref = O_element
FEATURE [App::DocumentObjectGroupPython] G4_GLYCEROL  # scripted group (container) (typed FeaturePython)
  Dunit = g/cm3
  Dvalue = 1.2613
  Group = -> [C_element050,H_element043,O_element047]
  conduct = 2
  density = 1
  expand = 3
  formula = G4_GLYCEROL
  name = G4_GLYCEROL
  specific = 4
FEATURE [App::DocumentObjectGroupPython] C_element051  label="C_element : 028"  # scripted group (container) (typed FeaturePython)
  n = 5
  ref = C_element
FEATURE [App::DocumentObjectGroupPython] H_element044  label="H_element : 023"  # scripted group (container) (typed FeaturePython)
  n = 5
  ref = H_element
FEATURE [App::DocumentObjectGroupPython] N_element020  label="N_element : 009"  # scripted group (container) (typed FeaturePython)
  n = 5
  ref = N_element
FEATURE [App::DocumentObjectGroupPython] O_element048  label="O_element : 024"  # scripted group (container) (typed FeaturePython)
  n = 1
  ref = O_element
FEATURE [App::DocumentObjectGroupPython] G4_GUANINE  # scripted group (container) (typed FeaturePython)
  Dunit = g/cm3
  Dvalue = 2.2
  Group = -> [C_element051,H_element044,N_element020,O_element048]
  conduct = 2
  density = 1
  expand = 3
  formula = G4_GUANINE
  name = G4_GUANINE
  specific = 4
FEATURE [App::DocumentObjectGroupPython] Ca_element012  label="Ca_element : 006"  # scripted group (container) (typed FeaturePython)
  n = 1
  ref = Ca_element
FEATURE [App::DocumentObjectGroupPython] S_element014  label="S_element : 005"  # scripted group (container) (typed FeaturePython)
  n = 1
  ref = S_element
FEATURE [App::DocumentObjectGroupPython] O_element049  label="O_element : 6"  # scripted group (container) (typed FeaturePython)
  n = 6
  ref = O_element
FEATURE [App::DocumentObjectGroupPython] H_element045  label="H_element : 024"  # scripted group (container) (typed FeaturePython)
  n = 4
  ref = H_element
FEATURE [App::DocumentObjectGroupPython] G4_GYPSUM  # scripted group (container) (typed FeaturePython)
  Dunit = g/cm3
  Dvalue = 2.32
  Group = -> [Ca_element012,S_element014,O_element049,H_element045]
  conduct = 2
  density = 1
  expand = 3
  formula = G4_GYPSUM
  name = G4_GYPSUM
  specific = 4
FEATURE [App::DocumentObjectGroupPython] C_element052  label="C_element : 7"  # scripted group (container) (typed FeaturePython)
  n = 7
  ref = C_element
FEATURE [App::DocumentObjectGroupPython] H_element046  label="H_element : 16"  # scripted group (container) (typed FeaturePython)
  n = 16
  ref = H_element
FEATURE [App::DocumentObjectGroupPython] G4_N_HEPTANE  label="G4_N-HEPTANE"  # scripted group (container) (typed FeaturePython)
  Dunit = g/cm3
  Dvalue = 0.68376
  Group = -> [C_element052,H_element046]
  conduct = 2
  density = 1
  expand = 3
  formula = G4_N-HEPTANE
  name = G4_N-HEPTANE
  specific = 4
FEATURE [App::DocumentObjectGroupPython] C_element053  label="C_element : 029"  # scripted group (container) (typed FeaturePython)
  n = 6
  ref = C_element
FEATURE [App::DocumentObjectGroupPython] H_element047  label="H_element : 14"  # scripted group (container) (typed FeaturePython)
  n = 14
  ref = H_element
FEATURE [App::DocumentObjectGroupPython] G4_N_HEXANE  label="G4_N-HEXANE"  # scripted group (container) (typed FeaturePython)
  Dunit = g/cm3
  Dvalue = 0.6603
  Group = -> [C_element053,H_element047]
  conduct = 2
  density = 1
  expand = 3
  formula = G4_N-HEXANE
  name = G4_N-HEXANE
  specific = 4
FEATURE [App::DocumentObjectGroupPython] C_element054  label="C_element : 22"  # scripted group (container) (typed FeaturePython)
  n = 22
  ref = C_element
FEATURE [App::DocumentObjectGroupPython] H_element048  label="H_element : 025"  # scripted group (container) (typed FeaturePython)
  n = 10
  ref = H_element
FEATURE [App::DocumentObjectGroupPython] N_element021  label="N_element : 010"  # scripted group (container) (typed FeaturePython)
  n = 2
  ref = N_element
FEATURE [App::DocumentObjectGroupPython] O_element050  label="O_element : 025"  # scripted group (container) (typed FeaturePython)
  n = 5
  ref = O_element
FEATURE [App::DocumentObjectGroupPython] G4_KAPTON  # scripted group (container) (typed FeaturePython)
  Dunit = g/cm3
  Dvalue = 1.42
  Group = -> [C_element054,H_element048,N_element021,O_element050]
  conduct = 2
  density = 1
  expand = 3
  formula = G4_KAPTON
  name = G4_KAPTON
  specific = 4
FEATURE [App::DocumentObjectGroupPython] La_element001  label="La_element : 1"  # scripted group (container) (typed FeaturePython)
  n = 1
  ref = La_element
FEATURE [App::DocumentObjectGroupPython] Br_element003  label="Br_element : 002"  # scripted group (container) (typed FeaturePython)
  n = 1
  ref = Br_element
FEATURE [App::DocumentObjectGroupPython] O_element051  label="O_element : 026"  # scripted group (container) (typed FeaturePython)
  n = 1
  ref = O_element
FEATURE [App::DocumentObjectGroupPython] G4_LANTHANUM_OXYBROMIDE  # scripted group (container) (typed FeaturePython)
  Dunit = g/cm3
  Dvalue = 6.28
  Group = -> [La_element001,Br_element003,O_element051]
  conduct = 2
  density = 1
  expand = 3
  formula = G4_LANTHANUM_OXYBROMIDE
  name = G4_LANTHANUM_OXYBROMIDE
  specific = 4
FEATURE [App::DocumentObjectGroupPython] La_element002  label="La_element : 2"  # scripted group (container) (typed FeaturePython)
  n = 2
  ref = La_element
FEATURE [App::DocumentObjectGroupPython] O_element052  label="O_element : 027"  # scripted group (container) (typed FeaturePython)
  n = 2
  ref = O_element
FEATURE [App::DocumentObjectGroupPython] S_element015  label="S_element : 006"  # scripted group (container) (typed FeaturePython)
  n = 1
  ref = S_element
FEATURE [App::DocumentObjectGroupPython] G4_LANTHANUM_OXYSULFIDE  # scripted group (container) (typed FeaturePython)
  Dunit = g/cm3
  Dvalue = 5.86
  Group = -> [La_element002,O_element052,S_element015]
  conduct = 2
  density = 1
  expand = 3
  formula = G4_LANTHANUM_OXYSULFIDE
  name = G4_LANTHANUM_OXYSULFIDE
  specific = 4
FEATURE [App::DocumentObjectGroupPython] O_element053  label="O_element : 0.072"  # scripted group (container) (typed FeaturePython)
  n = 0.071682
FEATURE [App::DocumentObjectGroupPython] Pb_element002  label="Pb_element : 0.928"  # scripted group (container) (typed FeaturePython)
  n = 0.928318
FEATURE [App::DocumentObjectGroupPython] G4_LEAD_OXIDE  # scripted group (container) (typed FeaturePython)
  Dunit = g/cm3
  Dvalue = 9.53
  Group = -> [O_element053,Pb_element002]
  conduct = 2
  density = 1
  expand = 3
  formula = G4_LEAD_OXIDE
  name = G4_LEAD_OXIDE
  specific = 4
FEATURE [App::DocumentObjectGroupPython] Li_element001  label="Li_element : 1"  # scripted group (container) (typed FeaturePython)
  n = 1
  ref = Li_element
FEATURE [App::DocumentObjectGroupPython] N_element022  label="N_element : 011"  # scripted group (container) (typed FeaturePython)
  n = 1
  ref = N_element
FEATURE [App::DocumentObjectGroupPython] H_element049  label="H_element : 026"  # scripted group (container) (typed FeaturePython)
  n = 2
  ref = H_element
FEATURE [App::DocumentObjectGroupPython] G4_LITHIUM_AMIDE  # scripted group (container) (typed FeaturePython)
  Dunit = g/cm3
  Dvalue = 1.178
  Group = -> [Li_element001,N_element022,H_element049]
  conduct = 2
  density = 1
  expand = 3
  formula = G4_LITHIUM_AMIDE
  name = G4_LITHIUM_AMIDE
  specific = 4
FEATURE [App::DocumentObjectGroupPython] Li_element002  label="Li_element : 2"  # scripted group (container) (typed FeaturePython)
  n = 2
  ref = Li_element
FEATURE [App::DocumentObjectGroupPython] C_element055  label="C_element : 030"  # scripted group (container) (typed FeaturePython)
  n = 1
  ref = C_element
FEATURE [App::DocumentObjectGroupPython] O_element054  label="O_element : 028"  # scripted group (container) (typed FeaturePython)
  n = 3
  ref = O_element
FEATURE [App::DocumentObjectGroupPython] G4_LITHIUM_CARBONATE  # scripted group (container) (typed FeaturePython)
  Dunit = g/cm3
  Dvalue = 2.11
  Group = -> [Li_element002,C_element055,O_element054]
  conduct = 2
  density = 1
  expand = 3
  formula = G4_LITHIUM_CARBONATE
  name = G4_LITHIUM_CARBONATE
  specific = 4
FEATURE [App::DocumentObjectGroupPython] Li_element003  label="Li_element : 003"  # scripted group (container) (typed FeaturePython)
  n = 1
  ref = Li_element
FEATURE [App::DocumentObjectGroupPython] F_element012  label="F_element : 004"  # scripted group (container) (typed FeaturePython)
  n = 1
  ref = F_element
FEATURE [App::DocumentObjectGroupPython] G4_LITHIUM_FLUORIDE  # scripted group (container) (typed FeaturePython)
  Dunit = g/cm3
  Dvalue = 2.635
  Group = -> [Li_element003,F_element012]
  conduct = 2
  density = 1
  expand = 3
  formula = G4_LITHIUM_FLUORIDE
  name = G4_LITHIUM_FLUORIDE
  specific = 4
FEATURE [App::DocumentObjectGroupPython] Li_element004  label="Li_element : 004"  # scripted group (container) (typed FeaturePython)
  n = 1
  ref = Li_element
FEATURE [App::DocumentObjectGroupPython] H_element050  label="H_element : 027"  # scripted group (container) (typed FeaturePython)
  n = 1
  ref = H_element
FEATURE [App::DocumentObjectGroupPython] G4_LITHIUM_HYDRIDE  # scripted group (container) (typed FeaturePython)
  Dunit = g/cm3
  Dvalue = 0.82
  Group = -> [Li_element004,H_element050]
  conduct = 2
  density = 1
  expand = 3
  formula = G4_LITHIUM_HYDRIDE
  name = G4_LITHIUM_HYDRIDE
  specific = 4
FEATURE [App::DocumentObjectGroupPython] Li_element005  label="Li_element : 005"  # scripted group (container) (typed FeaturePython)
  n = 1
  ref = Li_element
FEATURE [App::DocumentObjectGroupPython] I_element003  label="I_element : 002"  # scripted group (container) (typed FeaturePython)
  n = 1
  ref = I_element
FEATURE [App::DocumentObjectGroupPython] G4_LITHIUM_IODIDE  # scripted group (container) (typed FeaturePython)
  Dunit = g/cm3
  Dvalue = 3.494
  Group = -> [Li_element005,I_element003]
  conduct = 2
  density = 1
  expand = 3
  formula = G4_LITHIUM_IODIDE
  name = G4_LITHIUM_IODIDE
  specific = 4
FEATURE [App::DocumentObjectGroupPython] Li_element006  label="Li_element : 006"  # scripted group (container) (typed FeaturePython)
  n = 2
  ref = Li_element
FEATURE [App::DocumentObjectGroupPython] O_element055  label="O_element : 029"  # scripted group (container) (typed FeaturePython)
  n = 1
  ref = O_element
FEATURE [App::DocumentObjectGroupPython] G4_LITHIUM_OXIDE  # scripted group (container) (typed FeaturePython)
  Dunit = g/cm3
  Dvalue = 2.013
  Group = -> [Li_element006,O_element055]
  conduct = 2
  density = 1
  expand = 3
  formula = G4_LITHIUM_OXIDE
  name = G4_LITHIUM_OXIDE
  specific = 4
FEATURE [App::DocumentObjectGroupPython] Li_element007  label="Li_element : 007"  # scripted group (container) (typed FeaturePython)
  n = 2
  ref = Li_element
FEATURE [App::DocumentObjectGroupPython] B_element005  label="B_element : 005"  # scripted group (container) (typed FeaturePython)
  n = 4
  ref = B_element
FEATURE [App::DocumentObjectGroupPython] O_element056  label="O_element : 7"  # scripted group (container) (typed FeaturePython)
  n = 7
  ref = O_element
FEATURE [App::DocumentObjectGroupPython] G4_LITHIUM_TETRABORATE  # scripted group (container) (typed FeaturePython)
  Dunit = g/cm3
  Dvalue = 2.44
  Group = -> [Li_element007,B_element005,O_element056]
  conduct = 2
  density = 1
  expand = 3
  formula = G4_LITHIUM_TETRABORATE
  name = G4_LITHIUM_TETRABORATE
  specific = 4
FEATURE [App::DocumentObjectGroupPython] H_element051  label="H_element : 0.105"  # scripted group (container) (typed FeaturePython)
  n = 0.105
FEATURE [App::DocumentObjectGroupPython] C_element056  label="C_element : 0.083"  # scripted group (container) (typed FeaturePython)
  n = 0.083
FEATURE [App::DocumentObjectGroupPython] N_element023  label="N_element : 0.023"  # scripted group (container) (typed FeaturePython)
  n = 0.023
FEATURE [App::DocumentObjectGroupPython] O_element057  label="O_element : 0.779"  # scripted group (container) (typed FeaturePython)
  n = 0.779
FEATURE [App::DocumentObjectGroupPython] Na_element010  label="Na_element : 0.097"  # scripted group (container) (typed FeaturePython)
  n = 0.002
FEATURE [App::DocumentObjectGroupPython] P_element006  label="P_element : 0.105"  # scripted group (container) (typed FeaturePython)
  n = 0.001
FEATURE [App::DocumentObjectGroupPython] S_element016  label="S_element : 0.017"  # scripted group (container) (typed FeaturePython)
  n = 0.002
FEATURE [App::DocumentObjectGroupPython] Cl_element014  label="Cl_element : 0.587"  # scripted group (container) (typed FeaturePython)
  n = 0.003
FEATURE [App::DocumentObjectGroupPython] K_element005  label="K_element : 0.015"  # scripted group (container) (typed FeaturePython)
  n = 0.002
FEATURE [App::DocumentObjectGroupPython] G4_LUNG_ICRP  # scripted group (container) (typed FeaturePython)
  Dunit = g/cm3
  Dvalue = 1.04
  Group = -> [H_element051,C_element056,N_element023,O_element057,Na_element010,P_element006,S_element016,Cl_element014,K_element005]
  conduct = 2
  density = 1
  expand = 3
  formula = G4_LUNG_ICRP
  name = G4_LUNG_ICRP
  specific = 4
FEATURE [App::DocumentObjectGroupPython] H_element052  label="H_element : 0.116"  # scripted group (container) (typed FeaturePython)
  n = 0.114318
FEATURE [App::DocumentObjectGroupPython] C_element057  label="C_element : 0.656"  # scripted group (container) (typed FeaturePython)
  n = 0.655824
FEATURE [App::DocumentObjectGroupPython] O_element058  label="O_element : 0.092"  # scripted group (container) (typed FeaturePython)
  n = 0.0921831
FEATURE [App::DocumentObjectGroupPython] Mg_element004  label="Mg_element : 0.135"  # scripted group (container) (typed FeaturePython)
  n = 0.134792
FEATURE [App::DocumentObjectGroupPython] Ca_element013  label="Ca_element : 0.003"  # scripted group (container) (typed FeaturePython)
  n = 0.002883
FEATURE [App::DocumentObjectGroupPython] G4_M3_WAX  # scripted group (container) (typed FeaturePython)
  Dunit = g/cm3
  Dvalue = 1.05
  Group = -> [H_element052,C_element057,O_element058,Mg_element004,Ca_element013]
  conduct = 2
  density = 1
  expand = 3
  formula = G4_M3_WAX
  name = G4_M3_WAX
  specific = 4
FEATURE [App::DocumentObjectGroupPython] Mg_element005  label="Mg_element : 1"  # scripted group (container) (typed FeaturePython)
  n = 1
  ref = Mg_element
FEATURE [App::DocumentObjectGroupPython] C_element058  label="C_element : 031"  # scripted group (container) (typed FeaturePython)
  n = 1
  ref = C_element
FEATURE [App::DocumentObjectGroupPython] O_element059  label="O_element : 030"  # scripted group (container) (typed FeaturePython)
  n = 3
  ref = O_element
FEATURE [App::DocumentObjectGroupPython] G4_MAGNESIUM_CARBONATE  # scripted group (container) (typed FeaturePython)
  Dunit = g/cm3
  Dvalue = 2.958
  Group = -> [Mg_element005,C_element058,O_element059]
  conduct = 2
  density = 1
  expand = 3
  formula = G4_MAGNESIUM_CARBONATE
  name = G4_MAGNESIUM_CARBONATE
  specific = 4
FEATURE [App::DocumentObjectGroupPython] Mg_element006  label="Mg_element : 002"  # scripted group (container) (typed FeaturePython)
  n = 1
  ref = Mg_element
FEATURE [App::DocumentObjectGroupPython] F_element013  label="F_element : 005"  # scripted group (container) (typed FeaturePython)
  n = 2
  ref = F_element
FEATURE [App::DocumentObjectGroupPython] G4_MAGNESIUM_FLUORIDE  # scripted group (container) (typed FeaturePython)
  Dunit = g/cm3
  Dvalue = 3
  Group = -> [Mg_element006,F_element013]
  conduct = 2
  density = 1
  expand = 3
  formula = G4_MAGNESIUM_FLUORIDE
  name = G4_MAGNESIUM_FLUORIDE
  specific = 4
FEATURE [App::DocumentObjectGroupPython] Mg_element007  label="Mg_element : 003"  # scripted group (container) (typed FeaturePython)
  n = 1
  ref = Mg_element
FEATURE [App::DocumentObjectGroupPython] O_element060  label="O_element : 031"  # scripted group (container) (typed FeaturePython)
  n = 1
  ref = O_element
FEATURE [App::DocumentObjectGroupPython] G4_MAGNESIUM_OXIDE  # scripted group (container) (typed FeaturePython)
  Dunit = g/cm3
  Dvalue = 3.58
  Group = -> [Mg_element007,O_element060]
  conduct = 2
  density = 1
  expand = 3
  formula = G4_MAGNESIUM_OXIDE
  name = G4_MAGNESIUM_OXIDE
  specific = 4
FEATURE [App::DocumentObjectGroupPython] Mg_element008  label="Mg_element : 004"  # scripted group (container) (typed FeaturePython)
  n = 1
  ref = Mg_element
FEATURE [App::DocumentObjectGroupPython] B_element006  label="B_element : 006"  # scripted group (container) (typed FeaturePython)
  n = 4
  ref = B_element
FEATURE [App::DocumentObjectGroupPython] O_element061  label="O_element : 032"  # scripted group (container) (typed FeaturePython)
  n = 7
  ref = O_element
FEATURE [App::DocumentObjectGroupPython] G4_MAGNESIUM_TETRABORATE  # scripted group (container) (typed FeaturePython)
  Dunit = g/cm3
  Dvalue = 2.53
  Group = -> [Mg_element008,B_element006,O_element061]
  conduct = 2
  density = 1
  expand = 3
  formula = G4_MAGNESIUM_TETRABORATE
  name = G4_MAGNESIUM_TETRABORATE
  specific = 4
FEATURE [App::DocumentObjectGroupPython] Hg_element001  label="Hg_element : 1"  # scripted group (container) (typed FeaturePython)
  n = 1
  ref = Hg_element
FEATURE [App::DocumentObjectGroupPython] I_element004  label="I_element : 2"  # scripted group (container) (typed FeaturePython)
  n = 2
  ref = I_element
FEATURE [App::DocumentObjectGroupPython] G4_MERCURIC_IODIDE  # scripted group (container) (typed FeaturePython)
  Dunit = g/cm3
  Dvalue = 6.36
  Group = -> [Hg_element001,I_element004]
  conduct = 2
  density = 1
  expand = 3
  formula = G4_MERCURIC_IODIDE
  name = G4_MERCURIC_IODIDE
  specific = 4
FEATURE [App::DocumentObjectGroupPython] C_element059  label="C_element : 032"  # scripted group (container) (typed FeaturePython)
  n = 1
  ref = C_element
FEATURE [App::DocumentObjectGroupPython] H_element053  label="H_element : 028"  # scripted group (container) (typed FeaturePython)
  n = 4
  ref = H_element
FEATURE [App::DocumentObjectGroupPython] G4_METHANE  # scripted group (container) (typed FeaturePython)
  Dunit = g/cm3
  Dvalue = 0.000667151
  Group = -> [C_element059,H_element053]
  conduct = 2
  density = 1
  expand = 3
  formula = G4_METHANE
  name = G4_METHANE
  specific = 4
FEATURE [App::DocumentObjectGroupPython] C_element060  label="C_element : 033"  # scripted group (container) (typed FeaturePython)
  n = 1
  ref = C_element
FEATURE [App::DocumentObjectGroupPython] H_element054  label="H_element : 029"  # scripted group (container) (typed FeaturePython)
  n = 4
  ref = H_element
FEATURE [App::DocumentObjectGroupPython] O_element062  label="O_element : 033"  # scripted group (container) (typed FeaturePython)
  n = 1
  ref = O_element
FEATURE [App::DocumentObjectGroupPython] G4_METHANOL  # scripted group (container) (typed FeaturePython)
  Dunit = g/cm3
  Dvalue = 0.7914
  Group = -> [C_element060,H_element054,O_element062]
  conduct = 2
  density = 1
  expand = 3
  formula = G4_METHANOL
  name = G4_METHANOL
  specific = 4
FEATURE [App::DocumentObjectGroupPython] H_element055  label="H_element : 0.134"  # scripted group (container) (typed FeaturePython)
  n = 0.13404
FEATURE [App::DocumentObjectGroupPython] C_element061  label="C_element : 0.778"  # scripted group (container) (typed FeaturePython)
  n = 0.77796
FEATURE [App::DocumentObjectGroupPython] O_element063  label="O_element : 0.035"  # scripted group (container) (typed FeaturePython)
  n = 0.03502
FEATURE [App::DocumentObjectGroupPython] Mg_element009  label="Mg_element : 0.039"  # scripted group (container) (typed FeaturePython)
  n = 0.038594
FEATURE [App::DocumentObjectGroupPython] Ti_element002  label="Ti_element : 0.014"  # scripted group (container) (typed FeaturePython)
  n = 0.014386
FEATURE [App::DocumentObjectGroupPython] G4_MIX_D_WAX  # scripted group (container) (typed FeaturePython)
  Dunit = g/cm3
  Dvalue = 0.99
  Group = -> [H_element055,C_element061,O_element063,Mg_element009,Ti_element002]
  conduct = 2
  density = 1
  expand = 3
  formula = G4_MIX_D_WAX
  name = G4_MIX_D_WAX
  specific = 4
FEATURE [App::DocumentObjectGroupPython] H_element056  label="H_element : 0.135"  # scripted group (container) (typed FeaturePython)
  n = 0.081192
FEATURE [App::DocumentObjectGroupPython] C_element062  label="C_element : 0.583"  # scripted group (container) (typed FeaturePython)
  n = 0.583442
FEATURE [App::DocumentObjectGroupPython] N_element024  label="N_element : 0.018"  # scripted group (container) (typed FeaturePython)
  n = 0.017798
FEATURE [App::DocumentObjectGroupPython] O_element064  label="O_element : 0.186"  # scripted group (container) (typed FeaturePython)
  n = 0.186381
FEATURE [App::DocumentObjectGroupPython] Mg_element010  label="Mg_element : 0.130"  # scripted group (container) (typed FeaturePython)
  n = 0.130287
FEATURE [App::DocumentObjectGroupPython] Cl_element015  label="Cl_element : 0.588"  # scripted group (container) (typed FeaturePython)
  n = 0.0009
FEATURE [App::DocumentObjectGroupPython] G4_MS20_TISSUE  # scripted group (container) (typed FeaturePython)
  Dunit = g/cm3
  Dvalue = 1
  Group = -> [H_element056,C_element062,N_element024,O_element064,Mg_element010,Cl_element015]
  conduct = 2
  density = 1
  expand = 3
  formula = G4_MS20_TISSUE
  name = G4_MS20_TISSUE
  specific = 4
FEATURE [App::DocumentObjectGroupPython] H_element057  label="H_element : 0.136"  # scripted group (container) (typed FeaturePython)
  n = 0.102
FEATURE [App::DocumentObjectGroupPython] C_element063  label="C_element : 0.143"  # scripted group (container) (typed FeaturePython)
  n = 0.143
FEATURE [App::DocumentObjectGroupPython] N_element025  label="N_element : 0.034"  # scripted group (container) (typed FeaturePython)
  n = 0.034
FEATURE [App::DocumentObjectGroupPython] O_element065  label="O_element : 0.710"  # scripted group (container) (typed FeaturePython)
  n = 0.71
FEATURE [App::DocumentObjectGroupPython] Na_element011  label="Na_element : 0.098"  # scripted group (container) (typed FeaturePython)
  n = 0.001
FEATURE [App::DocumentObjectGroupPython] P_element007  label="P_element : 0.002"  # scripted group (container) (typed FeaturePython)
  n = 0.002
FEATURE [App::DocumentObjectGroupPython] S_element017  label="S_element : 0.018"  # scripted group (container) (typed FeaturePython)
  n = 0.003
FEATURE [App::DocumentObjectGroupPython] Cl_element016  label="Cl_element : 0.589"  # scripted group (container) (typed FeaturePython)
  n = 0.001
FEATURE [App::DocumentObjectGroupPython] K_element006  label="K_element : 0.004"  # scripted group (container) (typed FeaturePython)
  n = 0.004
FEATURE [App::DocumentObjectGroupPython] G4_MUSCLE_SKELETAL_ICRP  # scripted group (container) (typed FeaturePython)
  Dunit = g/cm3
  Dvalue = 1.05
  Group = -> [H_element057,C_element063,N_element025,O_element065,Na_element011,P_element007,S_element017,Cl_element016,K_element006]
  conduct = 2
  density = 1
  expand = 3
  formula = G4_MUSCLE_SKELETAL_ICRP
  name = G4_MUSCLE_SKELETAL_ICRP
  specific = 4
FEATURE [App::DocumentObjectGroupPython] H_element058  label="H_element : 0.137"  # scripted group (container) (typed FeaturePython)
  n = 0.102102
FEATURE [App::DocumentObjectGroupPython] C_element064  label="C_element : 0.123"  # scripted group (container) (typed FeaturePython)
  n = 0.123123
FEATURE [App::DocumentObjectGroupPython] N_element026  label="N_element : 0.756"  # scripted group (container) (typed FeaturePython)
  n = 0.035035
FEATURE [App::DocumentObjectGroupPython] O_element066  label="O_element : 0.730"  # scripted group (container) (typed FeaturePython)
  n = 0.72973
FEATURE [App::DocumentObjectGroupPython] Na_element012  label="Na_element : 0.099"  # scripted group (container) (typed FeaturePython)
  n = 0.001001
FEATURE [App::DocumentObjectGroupPython] P_element008  label="P_element : 0.106"  # scripted group (container) (typed FeaturePython)
  n = 0.002002
FEATURE [App::DocumentObjectGroupPython] S_element018  label="S_element : 0.019"  # scripted group (container) (typed FeaturePython)
  n = 0.004004
FEATURE [App::DocumentObjectGroupPython] K_element007  label="K_element : 0.016"  # scripted group (container) (typed FeaturePython)
  n = 0.003003
FEATURE [App::DocumentObjectGroupPython] G4_MUSCLE_STRIATED_ICRU  # scripted group (container) (typed FeaturePython)
  Dunit = g/cm3
  Dvalue = 1.04
  Group = -> [H_element058,C_element064,N_element026,O_element066,Na_element012,P_element008,S_element018,K_element007]
  conduct = 2
  density = 1
  expand = 3
  formula = G4_MUSCLE_STRIATED_ICRU
  name = G4_MUSCLE_STRIATED_ICRU
  specific = 4
FEATURE [App::DocumentObjectGroupPython] H_element059  label="H_element : 0.098"  # scripted group (container) (typed FeaturePython)
  n = 0.0982341
FEATURE [App::DocumentObjectGroupPython] C_element065  label="C_element : 0.156"  # scripted group (container) (typed FeaturePython)
  n = 0.156214
FEATURE [App::DocumentObjectGroupPython] N_element027  label="N_element : 0.757"  # scripted group (container) (typed FeaturePython)
  n = 0.035451
FEATURE [App::DocumentObjectGroupPython] O_element067  label="O_element : 0.880"  # scripted group (container) (typed FeaturePython)
  n = 0.710101
FEATURE [App::DocumentObjectGroupPython] G4_MUSCLE_WITH_SUCROSE  # scripted group (container) (typed FeaturePython)
  Dunit = g/cm3
  Dvalue = 1.11
  Group = -> [H_element059,C_element065,N_element027,O_element067]
  conduct = 2
  density = 1
  expand = 3
  formula = G4_MUSCLE_WITH_SUCROSE
  name = G4_MUSCLE_WITH_SUCROSE
  specific = 4
FEATURE [App::DocumentObjectGroupPython] H_element060  label="H_element : 0.138"  # scripted group (container) (typed FeaturePython)
  n = 0.101969
FEATURE [App::DocumentObjectGroupPython] C_element066  label="C_element : 0.120"  # scripted group (container) (typed FeaturePython)
  n = 0.120058
FEATURE [App::DocumentObjectGroupPython] N_element028  label="N_element : 0.758"  # scripted group (container) (typed FeaturePython)
  n = 0.035451
FEATURE [App::DocumentObjectGroupPython] O_element068  label="O_element : 0.743"  # scripted group (container) (typed FeaturePython)
  n = 0.742522
FEATURE [App::DocumentObjectGroupPython] G4_MUSCLE_WITHOUT_SUCROSE  # scripted group (container) (typed FeaturePython)
  Dunit = g/cm3
  Dvalue = 1.07
  Group = -> [H_element060,C_element066,N_element028,O_element068]
  conduct = 2
  density = 1
  expand = 3
  formula = G4_MUSCLE_WITHOUT_SUCROSE
  name = G4_MUSCLE_WITHOUT_SUCROSE
  specific = 4
FEATURE [App::DocumentObjectGroupPython] C_element067  label="C_element : 10"  # scripted group (container) (typed FeaturePython)
  n = 10
  ref = C_element
FEATURE [App::DocumentObjectGroupPython] H_element061  label="H_element : 030"  # scripted group (container) (typed FeaturePython)
  n = 8
  ref = H_element
FEATURE [App::DocumentObjectGroupPython] G4_NAPHTHALENE  # scripted group (container) (typed FeaturePython)
  Dunit = g/cm3
  Dvalue = 1.145
  Group = -> [C_element067,H_element061]
  conduct = 2
  density = 1
  expand = 3
  formula = G4_NAPHTHALENE
  name = G4_NAPHTHALENE
  specific = 4
FEATURE [App::DocumentObjectGroupPython] C_element068  label="C_element : 034"  # scripted group (container) (typed FeaturePython)
  n = 6
  ref = C_element
FEATURE [App::DocumentObjectGroupPython] H_element062  label="H_element : 031"  # scripted group (container) (typed FeaturePython)
  n = 5
  ref = H_element
FEATURE [App::DocumentObjectGroupPython] N_element029  label="N_element : 012"  # scripted group (container) (typed FeaturePython)
  n = 1
  ref = N_element
FEATURE [App::DocumentObjectGroupPython] O_element069  label="O_element : 034"  # scripted group (container) (typed FeaturePython)
  n = 2
  ref = O_element
FEATURE [App::DocumentObjectGroupPython] G4_NITROBENZENE  # scripted group (container) (typed FeaturePython)
  Dunit = g/cm3
  Dvalue = 1.19867
  Group = -> [C_element068,H_element062,N_element029,O_element069]
  conduct = 2
  density = 1
  expand = 3
  formula = G4_NITROBENZENE
  name = G4_NITROBENZENE
  specific = 4
FEATURE [App::DocumentObjectGroupPython] N_element030  label="N_element : 013"  # scripted group (container) (typed FeaturePython)
  n = 2
  ref = N_element
FEATURE [App::DocumentObjectGroupPython] O_element070  label="O_element : 035"  # scripted group (container) (typed FeaturePython)
  n = 1
  ref = O_element
FEATURE [App::DocumentObjectGroupPython] G4_NITROUS_OXIDE  # scripted group (container) (typed FeaturePython)
  Dunit = g/cm3
  Dvalue = 0.00183094
  Group = -> [N_element030,O_element070]
  conduct = 2
  density = 1
  expand = 3
  formula = G4_NITROUS_OXIDE
  name = G4_NITROUS_OXIDE
  specific = 4
FEATURE [App::DocumentObjectGroupPython] H_element063  label="H_element : 0.104"  # scripted group (container) (typed FeaturePython)
  n = 0.103509
FEATURE [App::DocumentObjectGroupPython] C_element069  label="C_element : 0.648"  # scripted group (container) (typed FeaturePython)
  n = 0.648416
FEATURE [App::DocumentObjectGroupPython] N_element031  label="N_element : 0.100"  # scripted group (container) (typed FeaturePython)
  n = 0.0995361
FEATURE [App::DocumentObjectGroupPython] O_element071  label="O_element : 0.149"  # scripted group (container) (typed FeaturePython)
  n = 0.148539
FEATURE [App::DocumentObjectGroupPython] G4_NYLON_8062  label="G4_NYLON-8062"  # scripted group (container) (typed FeaturePython)
  Dunit = g/cm3
  Dvalue = 1.08
  Group = -> [H_element063,C_element069,N_element031,O_element071]
  conduct = 2
  density = 1
  expand = 3
  formula = G4_NYLON-8062
  name = G4_NYLON-8062
  specific = 4
FEATURE [App::DocumentObjectGroupPython] C_element070  label="C_element : 035"  # scripted group (container) (typed FeaturePython)
  n = 6
  ref = C_element
FEATURE [App::DocumentObjectGroupPython] H_element064  label="H_element : 11"  # scripted group (container) (typed FeaturePython)
  n = 11
  ref = H_element
FEATURE [App::DocumentObjectGroupPython] N_element032  label="N_element : 014"  # scripted group (container) (typed FeaturePython)
  n = 1
  ref = N_element
FEATURE [App::DocumentObjectGroupPython] O_element072  label="O_element : 036"  # scripted group (container) (typed FeaturePython)
  n = 1
  ref = O_element
FEATURE [App::DocumentObjectGroupPython] G4_NYLON_6_6  label="G4_NYLON-6-6"  # scripted group (container) (typed FeaturePython)
  Dunit = g/cm3
  Dvalue = 1.14
  Group = -> [C_element070,H_element064,N_element032,O_element072]
  conduct = 2
  density = 1
  expand = 3
  formula = G4_NYLON-6-6
  name = G4_NYLON-6-6
  specific = 4
FEATURE [App::DocumentObjectGroupPython] H_element065  label="H_element : 0.139"  # scripted group (container) (typed FeaturePython)
  n = 0.107062
FEATURE [App::DocumentObjectGroupPython] C_element071  label="C_element : 0.680"  # scripted group (container) (typed FeaturePython)
  n = 0.680449
FEATURE [App::DocumentObjectGroupPython] N_element033  label="N_element : 0.099"  # scripted group (container) (typed FeaturePython)
  n = 0.099189
FEATURE [App::DocumentObjectGroupPython] O_element073  label="O_element : 0.113"  # scripted group (container) (typed FeaturePython)
  n = 0.1133
FEATURE [App::DocumentObjectGroupPython] G4_NYLON_6_10  label="G4_NYLON-6-10"  # scripted group (container) (typed FeaturePython)
  Dunit = g/cm3
  Dvalue = 1.14
  Group = -> [H_element065,C_element071,N_element033,O_element073]
  conduct = 2
  density = 1
  expand = 3
  formula = G4_NYLON-6-10
  name = G4_NYLON-6-10
  specific = 4
FEATURE [App::DocumentObjectGroupPython] H_element066  label="H_element : 0.140"  # scripted group (container) (typed FeaturePython)
  n = 0.115476
FEATURE [App::DocumentObjectGroupPython] C_element072  label="C_element : 0.721"  # scripted group (container) (typed FeaturePython)
  n = 0.720818
FEATURE [App::DocumentObjectGroupPython] N_element034  label="N_element : 0.076"  # scripted group (container) (typed FeaturePython)
  n = 0.0764169
FEATURE [App::DocumentObjectGroupPython] O_element074  label="O_element : 0.087"  # scripted group (container) (typed FeaturePython)
  n = 0.0872889
FEATURE [App::DocumentObjectGroupPython] G4_NYLON_11_RILSAN  label="G4_NYLON-11_RILSAN"  # scripted group (container) (typed FeaturePython)
  Dunit = g/cm3
  Dvalue = 1.425
  Group = -> [H_element066,C_element072,N_element034,O_element074]
  conduct = 2
  density = 1
  expand = 3
  formula = G4_NYLON-11_RILSAN
  name = G4_NYLON-11_RILSAN
  specific = 4
FEATURE [App::DocumentObjectGroupPython] C_element073  label="C_element : 8"  # scripted group (container) (typed FeaturePython)
  n = 8
  ref = C_element
FEATURE [App::DocumentObjectGroupPython] H_element067  label="H_element : 18"  # scripted group (container) (typed FeaturePython)
  n = 18
  ref = H_element
FEATURE [App::DocumentObjectGroupPython] G4_OCTANE  # scripted group (container) (typed FeaturePython)
  Dunit = g/cm3
  Dvalue = 0.7026
  Group = -> [C_element073,H_element067]
  conduct = 2
  density = 1
  expand = 3
  formula = G4_OCTANE
  name = G4_OCTANE
  specific = 4
FEATURE [App::DocumentObjectGroupPython] C_element074  label="C_element : 25"  # scripted group (container) (typed FeaturePython)
  n = 25
  ref = C_element
FEATURE [App::DocumentObjectGroupPython] H_element068  label="H_element : 52"  # scripted group (container) (typed FeaturePython)
  n = 52
  ref = H_element
FEATURE [App::DocumentObjectGroupPython] G4_PARAFFIN  # scripted group (container) (typed FeaturePython)
  Dunit = g/cm3
  Dvalue = 0.93
  Group = -> [C_element074,H_element068]
  conduct = 2
  density = 1
  expand = 3
  formula = G4_PARAFFIN
  name = G4_PARAFFIN
  specific = 4
FEATURE [App::DocumentObjectGroupPython] C_element075  label="C_element : 036"  # scripted group (container) (typed FeaturePython)
  n = 5
  ref = C_element
FEATURE [App::DocumentObjectGroupPython] H_element069  label="H_element : 032"  # scripted group (container) (typed FeaturePython)
  n = 12
  ref = H_element
FEATURE [App::DocumentObjectGroupPython] G4_N_PENTANE  label="G4_N-PENTANE"  # scripted group (container) (typed FeaturePython)
  Dunit = g/cm3
  Dvalue = 0.6262
  Group = -> [C_element075,H_element069]
  conduct = 2
  density = 1
  expand = 3
  formula = G4_N-PENTANE
  name = G4_N-PENTANE
  specific = 4
FEATURE [App::DocumentObjectGroupPython] H_element070  label="H_element : 0.014"  # scripted group (container) (typed FeaturePython)
  n = 0.0141
FEATURE [App::DocumentObjectGroupPython] C_element076  label="C_element : 0.072"  # scripted group (container) (typed FeaturePython)
  n = 0.072261
FEATURE [App::DocumentObjectGroupPython] N_element035  label="N_element : 0.019"  # scripted group (container) (typed FeaturePython)
  n = 0.01932
FEATURE [App::DocumentObjectGroupPython] O_element075  label="O_element : 0.066"  # scripted group (container) (typed FeaturePython)
  n = 0.066101
FEATURE [App::DocumentObjectGroupPython] S_element019  label="S_element : 0.020"  # scripted group (container) (typed FeaturePython)
  n = 0.00189
FEATURE [App::DocumentObjectGroupPython] Br_element004  label="Br_element : 0.349"  # scripted group (container) (typed FeaturePython)
  n = 0.349103
FEATURE [App::DocumentObjectGroupPython] Ag_element001  label="Ag_element : 0.474"  # scripted group (container) (typed FeaturePython)
  n = 0.474105
FEATURE [App::DocumentObjectGroupPython] I_element005  label="I_element : 0.003"  # scripted group (container) (typed FeaturePython)
  n = 0.00312
FEATURE [App::DocumentObjectGroupPython] G4_PHOTO_EMULSION  # scripted group (container) (typed FeaturePython)
  Dunit = g/cm3
  Dvalue = 3.815
  Group = -> [H_element070,C_element076,N_element035,O_element075,S_element019,Br_element004,Ag_element001,I_element005]
  conduct = 2
  density = 1
  expand = 3
  formula = G4_PHOTO_EMULSION
  name = G4_PHOTO_EMULSION
  specific = 4
FEATURE [App::DocumentObjectGroupPython] C_element077  label="C_element : 9"  # scripted group (container) (typed FeaturePython)
  n = 9
  ref = C_element
FEATURE [App::DocumentObjectGroupPython] H_element071  label="H_element : 033"  # scripted group (container) (typed FeaturePython)
  n = 10
  ref = H_element
FEATURE [App::DocumentObjectGroupPython] G4_PLASTIC_SC_VINYLTOLUENE  # scripted group (container) (typed FeaturePython)
  Dunit = g/cm3
  Dvalue = 1.032
  Group = -> [C_element077,H_element071]
  conduct = 2
  density = 1
  expand = 3
  formula = G4_PLASTIC_SC_VINYLTOLUENE
  name = G4_PLASTIC_SC_VINYLTOLUENE
  specific = 4
FEATURE [App::DocumentObjectGroupPython] Pu_element001  label="Pu_element : 1"  # scripted group (container) (typed FeaturePython)
  n = 1
  ref = Pu_element
FEATURE [App::DocumentObjectGroupPython] O_element076  label="O_element : 037"  # scripted group (container) (typed FeaturePython)
  n = 2
  ref = O_element
FEATURE [App::DocumentObjectGroupPython] G4_PLUTONIUM_DIOXIDE  # scripted group (container) (typed FeaturePython)
  Dunit = g/cm3
  Dvalue = 11.46
  Group = -> [Pu_element001,O_element076]
  conduct = 2
  density = 1
  expand = 3
  formula = G4_PLUTONIUM_DIOXIDE
  name = G4_PLUTONIUM_DIOXIDE
  specific = 4
FEATURE [App::DocumentObjectGroupPython] C_element078  label="C_element : 037"  # scripted group (container) (typed FeaturePython)
  n = 3
  ref = C_element
FEATURE [App::DocumentObjectGroupPython] H_element072  label="H_element : 034"  # scripted group (container) (typed FeaturePython)
  n = 3
  ref = H_element
FEATURE [App::DocumentObjectGroupPython] N_element036  label="N_element : 015"  # scripted group (container) (typed FeaturePython)
  n = 1
  ref = N_element
FEATURE [App::DocumentObjectGroupPython] G4_POLYACRYLONITRILE  # scripted group (container) (typed FeaturePython)
  Dunit = g/cm3
  Dvalue = 1.17
  Group = -> [C_element078,H_element072,N_element036]
  conduct = 2
  density = 1
  expand = 3
  formula = G4_POLYACRYLONITRILE
  name = G4_POLYACRYLONITRILE
  specific = 4
FEATURE [App::DocumentObjectGroupPython] C_element079  label="C_element : 16"  # scripted group (container) (typed FeaturePython)
  n = 16
  ref = C_element
FEATURE [App::DocumentObjectGroupPython] H_element073  label="H_element : 035"  # scripted group (container) (typed FeaturePython)
  n = 14
  ref = H_element
FEATURE [App::DocumentObjectGroupPython] O_element077  label="O_element : 038"  # scripted group (container) (typed FeaturePython)
  n = 3
  ref = O_element
FEATURE [App::DocumentObjectGroupPython] G4_POLYCARBONATE  # scripted group (container) (typed FeaturePython)
  Dunit = g/cm3
  Dvalue = 1.2
  Group = -> [C_element079,H_element073,O_element077]
  conduct = 2
  density = 1
  expand = 3
  formula = G4_POLYCARBONATE
  name = G4_POLYCARBONATE
  specific = 4
FEATURE [App::DocumentObjectGroupPython] C_element080  label="C_element : 038"  # scripted group (container) (typed FeaturePython)
  n = 8
  ref = C_element
FEATURE [App::DocumentObjectGroupPython] H_element074  label="H_element : 036"  # scripted group (container) (typed FeaturePython)
  n = 7
  ref = H_element
FEATURE [App::DocumentObjectGroupPython] Cl_element017  label="Cl_element : 007"  # scripted group (container) (typed FeaturePython)
  n = 1
  ref = Cl_element
FEATURE [App::DocumentObjectGroupPython] G4_POLYCHLOROSTYRENE  # scripted group (container) (typed FeaturePython)
  Dunit = g/cm3
  Dvalue = 1.3
  Group = -> [C_element080,H_element074,Cl_element017]
  conduct = 2
  density = 1
  expand = 3
  formula = G4_POLYCHLOROSTYRENE
  name = G4_POLYCHLOROSTYRENE
  specific = 4
FEATURE [App::DocumentObjectGroupPython] C_element081  label="C_element : 039"  # scripted group (container) (typed FeaturePython)
  n = 1
  ref = C_element
FEATURE [App::DocumentObjectGroupPython] H_element075  label="H_element : 037"  # scripted group (container) (typed FeaturePython)
  n = 2
  ref = H_element
FEATURE [App::DocumentObjectGroupPython] G4_POLYETHYLENE  # scripted group (container) (typed FeaturePython)
  Dunit = g/cm3
  Dvalue = 0.94
  Group = -> [C_element081,H_element075]
  conduct = 2
  density = 1
  expand = 3
  formula = G4_POLYETHYLENE
  name = G4_POLYETHYLENE
  specific = 4
FEATURE [App::DocumentObjectGroupPython] C_element082  label="C_element : 040"  # scripted group (container) (typed FeaturePython)
  n = 10
  ref = C_element
FEATURE [App::DocumentObjectGroupPython] H_element076  label="H_element : 038"  # scripted group (container) (typed FeaturePython)
  n = 8
  ref = H_element
FEATURE [App::DocumentObjectGroupPython] O_element078  label="O_element : 039"  # scripted group (container) (typed FeaturePython)
  n = 4
  ref = O_element
FEATURE [App::DocumentObjectGroupPython] G4_MYLAR  # scripted group (container) (typed FeaturePython)
  Dunit = g/cm3
  Dvalue = 1.4
  Group = -> [C_element082,H_element076,O_element078]
  conduct = 2
  density = 1
  expand = 3
  formula = G4_MYLAR
  name = G4_MYLAR
  specific = 4
FEATURE [App::DocumentObjectGroupPython] C_element083  label="C_element : 041"  # scripted group (container) (typed FeaturePython)
  n = 5
  ref = C_element
FEATURE [App::DocumentObjectGroupPython] H_element077  label="H_element : 039"  # scripted group (container) (typed FeaturePython)
  n = 8
  ref = H_element
FEATURE [App::DocumentObjectGroupPython] O_element079  label="O_element : 040"  # scripted group (container) (typed FeaturePython)
  n = 2
  ref = O_element
FEATURE [App::DocumentObjectGroupPython] G4_PLEXIGLASS  # scripted group (container) (typed FeaturePython)
  Dunit = g/cm3
  Dvalue = 1.19
  Group = -> [C_element083,H_element077,O_element079]
  conduct = 2
  density = 1
  expand = 3
  formula = G4_PLEXIGLASS
  name = G4_PLEXIGLASS
  specific = 4
FEATURE [App::DocumentObjectGroupPython] C_element084  label="C_element : 042"  # scripted group (container) (typed FeaturePython)
  n = 1
  ref = C_element
FEATURE [App::DocumentObjectGroupPython] H_element078  label="H_element : 040"  # scripted group (container) (typed FeaturePython)
  n = 2
  ref = H_element
FEATURE [App::DocumentObjectGroupPython] O_element080  label="O_element : 041"  # scripted group (container) (typed FeaturePython)
  n = 1
  ref = O_element
FEATURE [App::DocumentObjectGroupPython] G4_POLYOXYMETHYLENE  # scripted group (container) (typed FeaturePython)
  Dunit = g/cm3
  Dvalue = 1.425
  Group = -> [C_element084,H_element078,O_element080]
  conduct = 2
  density = 1
  expand = 3
  formula = G4_POLYOXYMETHYLENE
  name = G4_POLYOXYMETHYLENE
  specific = 4
FEATURE [App::DocumentObjectGroupPython] C_element085  label="C_element : 043"  # scripted group (container) (typed FeaturePython)
  n = 2
  ref = C_element
FEATURE [App::DocumentObjectGroupPython] H_element079  label="H_element : 041"  # scripted group (container) (typed FeaturePython)
  n = 4
  ref = H_element
FEATURE [App::DocumentObjectGroupPython] G4_POLYPROPYLENE  # scripted group (container) (typed FeaturePython)
  Dunit = g/cm3
  Dvalue = 0.9
  Group = -> [C_element085,H_element079]
  conduct = 2
  density = 1
  expand = 3
  formula = G4_POLYPROPYLENE
  name = G4_POLYPROPYLENE
  specific = 4
FEATURE [App::DocumentObjectGroupPython] C_element086  label="C_element : 044"  # scripted group (container) (typed FeaturePython)
  n = 8
  ref = C_element
FEATURE [App::DocumentObjectGroupPython] H_element080  label="H_element : 042"  # scripted group (container) (typed FeaturePython)
  n = 8
  ref = H_element
FEATURE [App::DocumentObjectGroupPython] G4_POLYSTYRENE  # scripted group (container) (typed FeaturePython)
  Dunit = g/cm3
  Dvalue = 1.06
  Group = -> [C_element086,H_element080]
  conduct = 2
  density = 1
  expand = 3
  formula = G4_POLYSTYRENE
  name = G4_POLYSTYRENE
  specific = 4
FEATURE [App::DocumentObjectGroupPython] C_element087  label="C_element : 045"  # scripted group (container) (typed FeaturePython)
  n = 2
  ref = C_element
FEATURE [App::DocumentObjectGroupPython] F_element014  label="F_element : 4"  # scripted group (container) (typed FeaturePython)
  n = 4
  ref = F_element
FEATURE [App::DocumentObjectGroupPython] G4_TEFLON  # scripted group (container) (typed FeaturePython)
  Dunit = g/cm3
  Dvalue = 2.2
  Group = -> [C_element087,F_element014]
  conduct = 2
  density = 1
  expand = 3
  formula = G4_TEFLON
  name = G4_TEFLON
  specific = 4
FEATURE [App::DocumentObjectGroupPython] C_element088  label="C_element : 046"  # scripted group (container) (typed FeaturePython)
  n = 2
  ref = C_element
FEATURE [App::DocumentObjectGroupPython] F_element015  label="F_element : 006"  # scripted group (container) (typed FeaturePython)
  n = 3
  ref = F_element
FEATURE [App::DocumentObjectGroupPython] Cl_element018  label="Cl_element : 008"  # scripted group (container) (typed FeaturePython)
  n = 1
  ref = Cl_element
FEATURE [App::DocumentObjectGroupPython] G4_POLYTRIFLUOROCHLOROETHYLENE  # scripted group (container) (typed FeaturePython)
  Dunit = g/cm3
  Dvalue = 2.1
  Group = -> [C_element088,F_element015,Cl_element018]
  conduct = 2
  density = 1
  expand = 3
  formula = G4_POLYTRIFLUOROCHLOROETHYLENE
  name = G4_POLYTRIFLUOROCHLOROETHYLENE
  specific = 4
FEATURE [App::DocumentObjectGroupPython] C_element089  label="C_element : 047"  # scripted group (container) (typed FeaturePython)
  n = 4
  ref = C_element
FEATURE [App::DocumentObjectGroupPython] H_element081  label="H_element : 043"  # scripted group (container) (typed FeaturePython)
  n = 6
  ref = H_element
FEATURE [App::DocumentObjectGroupPython] O_element081  label="O_element : 042"  # scripted group (container) (typed FeaturePython)
  n = 2
  ref = O_element
FEATURE [App::DocumentObjectGroupPython] G4_POLYVINYL_ACETATE  # scripted group (container) (typed FeaturePython)
  Dunit = g/cm3
  Dvalue = 1.19
  Group = -> [C_element089,H_element081,O_element081]
  conduct = 2
  density = 1
  expand = 3
  formula = G4_POLYVINYL_ACETATE
  name = G4_POLYVINYL_ACETATE
  specific = 4
FEATURE [App::DocumentObjectGroupPython] C_element090  label="C_element : 048"  # scripted group (container) (typed FeaturePython)
  n = 2
  ref = C_element
FEATURE [App::DocumentObjectGroupPython] H_element082  label="H_element : 044"  # scripted group (container) (typed FeaturePython)
  n = 4
  ref = H_element
FEATURE [App::DocumentObjectGroupPython] O_element082  label="O_element : 043"  # scripted group (container) (typed FeaturePython)
  n = 1
  ref = O_element
FEATURE [App::DocumentObjectGroupPython] G4_POLYVINYL_ALCOHOL  # scripted group (container) (typed FeaturePython)
  Dunit = g/cm3
  Dvalue = 1.3
  Group = -> [C_element090,H_element082,O_element082]
  conduct = 2
  density = 1
  expand = 3
  formula = G4_POLYVINYL_ALCOHOL
  name = G4_POLYVINYL_ALCOHOL
  specific = 4
FEATURE [App::DocumentObjectGroupPython] C_element091  label="C_element : 049"  # scripted group (container) (typed FeaturePython)
  n = 8
  ref = C_element
FEATURE [App::DocumentObjectGroupPython] H_element083  label="H_element : 045"  # scripted group (container) (typed FeaturePython)
  n = 14
  ref = H_element
FEATURE [App::DocumentObjectGroupPython] O_element083  label="O_element : 044"  # scripted group (container) (typed FeaturePython)
  n = 2
  ref = O_element
FEATURE [App::DocumentObjectGroupPython] G4_POLYVINYL_BUTYRAL  # scripted group (container) (typed FeaturePython)
  Dunit = g/cm3
  Dvalue = 1.12
  Group = -> [C_element091,H_element083,O_element083]
  conduct = 2
  density = 1
  expand = 3
  formula = G4_POLYVINYL_BUTYRAL
  name = G4_POLYVINYL_BUTYRAL
  specific = 4
FEATURE [App::DocumentObjectGroupPython] C_element092  label="C_element : 050"  # scripted group (container) (typed FeaturePython)
  n = 2
  ref = C_element
FEATURE [App::DocumentObjectGroupPython] H_element084  label="H_element : 046"  # scripted group (container) (typed FeaturePython)
  n = 3
  ref = H_element
FEATURE [App::DocumentObjectGroupPython] Cl_element019  label="Cl_element : 009"  # scripted group (container) (typed FeaturePython)
  n = 1
  ref = Cl_element
FEATURE [App::DocumentObjectGroupPython] G4_POLYVINYL_CHLORIDE  # scripted group (container) (typed FeaturePython)
  Dunit = g/cm3
  Dvalue = 1.3
  Group = -> [C_element092,H_element084,Cl_element019]
  conduct = 2
  density = 1
  expand = 3
  formula = G4_POLYVINYL_CHLORIDE
  name = G4_POLYVINYL_CHLORIDE
  specific = 4
FEATURE [App::DocumentObjectGroupPython] C_element093  label="C_element : 051"  # scripted group (container) (typed FeaturePython)
  n = 2
  ref = C_element
FEATURE [App::DocumentObjectGroupPython] H_element085  label="H_element : 047"  # scripted group (container) (typed FeaturePython)
  n = 2
  ref = H_element
FEATURE [App::DocumentObjectGroupPython] Cl_element020  label="Cl_element : 010"  # scripted group (container) (typed FeaturePython)
  n = 2
  ref = Cl_element
FEATURE [App::DocumentObjectGroupPython] G4_POLYVINYLIDENE_CHLORIDE  # scripted group (container) (typed FeaturePython)
  Dunit = g/cm3
  Dvalue = 1.7
  Group = -> [C_element093,H_element085,Cl_element020]
  conduct = 2
  density = 1
  expand = 3
  formula = G4_POLYVINYLIDENE_CHLORIDE
  name = G4_POLYVINYLIDENE_CHLORIDE
  specific = 4
FEATURE [App::DocumentObjectGroupPython] C_element094  label="C_element : 052"  # scripted group (container) (typed FeaturePython)
  n = 2
  ref = C_element
FEATURE [App::DocumentObjectGroupPython] H_element086  label="H_element : 048"  # scripted group (container) (typed FeaturePython)
  n = 2
  ref = H_element
FEATURE [App::DocumentObjectGroupPython] F_element016  label="F_element : 007"  # scripted group (container) (typed FeaturePython)
  n = 2
  ref = F_element
FEATURE [App::DocumentObjectGroupPython] G4_POLYVINYLIDENE_FLUORIDE  # scripted group (container) (typed FeaturePython)
  Dunit = g/cm3
  Dvalue = 1.76
  Group = -> [C_element094,H_element086,F_element016]
  conduct = 2
  density = 1
  expand = 3
  formula = G4_POLYVINYLIDENE_FLUORIDE
  name = G4_POLYVINYLIDENE_FLUORIDE
  specific = 4
FEATURE [App::DocumentObjectGroupPython] C_element095  label="C_element : 053"  # scripted group (container) (typed FeaturePython)
  n = 6
  ref = C_element
FEATURE [App::DocumentObjectGroupPython] H_element087  label="H_element : 9"  # scripted group (container) (typed FeaturePython)
  n = 9
  ref = H_element
FEATURE [App::DocumentObjectGroupPython] N_element037  label="N_element : 016"  # scripted group (container) (typed FeaturePython)
  n = 1
  ref = N_element
FEATURE [App::DocumentObjectGroupPython] O_element084  label="O_element : 045"  # scripted group (container) (typed FeaturePython)
  n = 1
  ref = O_element
FEATURE [App::DocumentObjectGroupPython] G4_POLYVINYL_PYRROLIDONE  # scripted group (container) (typed FeaturePython)
  Dunit = g/cm3
  Dvalue = 1.25
  Group = -> [C_element095,H_element087,N_element037,O_element084]
  conduct = 2
  density = 1
  expand = 3
  formula = G4_POLYVINYL_PYRROLIDONE
  name = G4_POLYVINYL_PYRROLIDONE
  specific = 4
FEATURE [App::DocumentObjectGroupPython] K_element008  label="K_element : 1"  # scripted group (container) (typed FeaturePython)
  n = 1
  ref = K_element
FEATURE [App::DocumentObjectGroupPython] I_element006  label="I_element : 003"  # scripted group (container) (typed FeaturePython)
  n = 1
  ref = I_element
FEATURE [App::DocumentObjectGroupPython] G4_POTASSIUM_IODIDE  # scripted group (container) (typed FeaturePython)
  Dunit = g/cm3
  Dvalue = 3.13
  Group = -> [K_element008,I_element006]
  conduct = 2
  density = 1
  expand = 3
  formula = G4_POTASSIUM_IODIDE
  name = G4_POTASSIUM_IODIDE
  specific = 4
FEATURE [App::DocumentObjectGroupPython] K_element009  label="K_element : 2"  # scripted group (container) (typed FeaturePython)
  n = 2
  ref = K_element
FEATURE [App::DocumentObjectGroupPython] O_element085  label="O_element : 046"  # scripted group (container) (typed FeaturePython)
  n = 1
  ref = O_element
FEATURE [App::DocumentObjectGroupPython] G4_POTASSIUM_OXIDE  # scripted group (container) (typed FeaturePython)
  Dunit = g/cm3
  Dvalue = 2.32
  Group = -> [K_element009,O_element085]
  conduct = 2
  density = 1
  expand = 3
  formula = G4_POTASSIUM_OXIDE
  name = G4_POTASSIUM_OXIDE
  specific = 4
FEATURE [App::DocumentObjectGroupPython] C_element096  label="C_element : 054"  # scripted group (container) (typed FeaturePython)
  n = 3
  ref = C_element
FEATURE [App::DocumentObjectGroupPython] H_element088  label="H_element : 049"  # scripted group (container) (typed FeaturePython)
  n = 8
  ref = H_element
FEATURE [App::DocumentObjectGroupPython] G4_PROPANE  # scripted group (container) (typed FeaturePython)
  Dunit = g/cm3
  Dvalue = 0.00187939
  Group = -> [C_element096,H_element088]
  conduct = 2
  density = 1
  expand = 3
  formula = G4_PROPANE
  name = G4_PROPANE
  specific = 4
FEATURE [App::DocumentObjectGroupPython] C_element097  label="C_element : 055"  # scripted group (container) (typed FeaturePython)
  n = 3
  ref = C_element
FEATURE [App::DocumentObjectGroupPython] H_element089  label="H_element : 050"  # scripted group (container) (typed FeaturePython)
  n = 8
  ref = H_element
FEATURE [App::DocumentObjectGroupPython] G4_lPROPANE  # scripted group (container) (typed FeaturePython)
  Dunit = g/cm3
  Dvalue = 0.43
  Group = -> [C_element097,H_element089]
  conduct = 2
  density = 1
  expand = 3
  formula = G4_lPROPANE
  name = G4_lPROPANE
  specific = 4
FEATURE [App::DocumentObjectGroupPython] C_element098  label="C_element : 056"  # scripted group (container) (typed FeaturePython)
  n = 3
  ref = C_element
FEATURE [App::DocumentObjectGroupPython] H_element090  label="H_element : 051"  # scripted group (container) (typed FeaturePython)
  n = 8
  ref = H_element
FEATURE [App::DocumentObjectGroupPython] O_element086  label="O_element : 047"  # scripted group (container) (typed FeaturePython)
  n = 1
  ref = O_element
FEATURE [App::DocumentObjectGroupPython] G4_N_PROPYL_ALCOHOL  label="G4_N-PROPYL_ALCOHOL"  # scripted group (container) (typed FeaturePython)
  Dunit = g/cm3
  Dvalue = 0.8035
  Group = -> [C_element098,H_element090,O_element086]
  conduct = 2
  density = 1
  expand = 3
  formula = G4_N-PROPYL_ALCOHOL
  name = G4_N-PROPYL_ALCOHOL
  specific = 4
FEATURE [App::DocumentObjectGroupPython] C_element099  label="C_element : 057"  # scripted group (container) (typed FeaturePython)
  n = 5
  ref = C_element
FEATURE [App::DocumentObjectGroupPython] H_element091  label="H_element : 052"  # scripted group (container) (typed FeaturePython)
  n = 5
  ref = H_element
FEATURE [App::DocumentObjectGroupPython] N_element038  label="N_element : 017"  # scripted group (container) (typed FeaturePython)
  n = 1
  ref = N_element
FEATURE [App::DocumentObjectGroupPython] G4_PYRIDINE  # scripted group (container) (typed FeaturePython)
  Dunit = g/cm3
  Dvalue = 0.9819
  Group = -> [C_element099,H_element091,N_element038]
  conduct = 2
  density = 1
  expand = 3
  formula = G4_PYRIDINE
  name = G4_PYRIDINE
  specific = 4
FEATURE [App::DocumentObjectGroupPython] H_element092  label="H_element : 0.144"  # scripted group (container) (typed FeaturePython)
  n = 0.143711
FEATURE [App::DocumentObjectGroupPython] C_element100  label="C_element : 0.856"  # scripted group (container) (typed FeaturePython)
  n = 0.856289
FEATURE [App::DocumentObjectGroupPython] G4_RUBBER_BUTYL  # scripted group (container) (typed FeaturePython)
  Dunit = g/cm3
  Dvalue = 0.92
  Group = -> [H_element092,C_element100]
  conduct = 2
  density = 1
  expand = 3
  formula = G4_RUBBER_BUTYL
  name = G4_RUBBER_BUTYL
  specific = 4
FEATURE [App::DocumentObjectGroupPython] H_element093  label="H_element : 0.118"  # scripted group (container) (typed FeaturePython)
  n = 0.118371
FEATURE [App::DocumentObjectGroupPython] C_element101  label="C_element : 0.882"  # scripted group (container) (typed FeaturePython)
  n = 0.881629
FEATURE [App::DocumentObjectGroupPython] G4_RUBBER_NATURAL  # scripted group (container) (typed FeaturePython)
  Dunit = g/cm3
  Dvalue = 0.92
  Group = -> [H_element093,C_element101]
  conduct = 2
  density = 1
  expand = 3
  formula = G4_RUBBER_NATURAL
  name = G4_RUBBER_NATURAL
  specific = 4
FEATURE [App::DocumentObjectGroupPython] H_element094  label="H_element : 0.145"  # scripted group (container) (typed FeaturePython)
  n = 0.05692
FEATURE [App::DocumentObjectGroupPython] C_element102  label="C_element : 0.543"  # scripted group (container) (typed FeaturePython)
  n = 0.542646
FEATURE [App::DocumentObjectGroupPython] Cl_element021  label="Cl_element : 0.400"  # scripted group (container) (typed FeaturePython)
  n = 0.400434
FEATURE [App::DocumentObjectGroupPython] G4_RUBBER_NEOPRENE  # scripted group (container) (typed FeaturePython)
  Dunit = g/cm3
  Dvalue = 1.23
  Group = -> [H_element094,C_element102,Cl_element021]
  conduct = 2
  density = 1
  expand = 3
  formula = G4_RUBBER_NEOPRENE
  name = G4_RUBBER_NEOPRENE
  specific = 4
FEATURE [App::DocumentObjectGroupPython] Si_element006  label="Si_element : 1"  # scripted group (container) (typed FeaturePython)
  n = 1
  ref = Si_element
FEATURE [App::DocumentObjectGroupPython] O_element087  label="O_element : 048"  # scripted group (container) (typed FeaturePython)
  n = 2
  ref = O_element
FEATURE [App::DocumentObjectGroupPython] G4_SILICON_DIOXIDE  # scripted group (container) (typed FeaturePython)
  Dunit = g/cm3
  Dvalue = 2.32
  Group = -> [Si_element006,O_element087]
  conduct = 2
  density = 1
  expand = 3
  formula = G4_SILICON_DIOXIDE
  name = G4_SILICON_DIOXIDE
  specific = 4
FEATURE [App::DocumentObjectGroupPython] Ag_element002  label="Ag_element : 1"  # scripted group (container) (typed FeaturePython)
  n = 1
  ref = Ag_element
FEATURE [App::DocumentObjectGroupPython] Br_element005  label="Br_element : 003"  # scripted group (container) (typed FeaturePython)
  n = 1
  ref = Br_element
FEATURE [App::DocumentObjectGroupPython] G4_SILVER_BROMIDE  # scripted group (container) (typed FeaturePython)
  Dunit = g/cm3
  Dvalue = 6.473
  Group = -> [Ag_element002,Br_element005]
  conduct = 2
  density = 1
  expand = 3
  formula = G4_SILVER_BROMIDE
  name = G4_SILVER_BROMIDE
  specific = 4
FEATURE [App::DocumentObjectGroupPython] Ag_element003  label="Ag_element : 002"  # scripted group (container) (typed FeaturePython)
  n = 1
  ref = Ag_element
FEATURE [App::DocumentObjectGroupPython] Cl_element022  label="Cl_element : 011"  # scripted group (container) (typed FeaturePython)
  n = 1
  ref = Cl_element
FEATURE [App::DocumentObjectGroupPython] G4_SILVER_CHLORIDE  # scripted group (container) (typed FeaturePython)
  Dunit = g/cm3
  Dvalue = 5.56
  Group = -> [Ag_element003,Cl_element022]
  conduct = 2
  density = 1
  expand = 3
  formula = G4_SILVER_CHLORIDE
  name = G4_SILVER_CHLORIDE
  specific = 4
FEATURE [App::DocumentObjectGroupPython] Br_element006  label="Br_element : 0.423"  # scripted group (container) (typed FeaturePython)
  n = 0.422895
FEATURE [App::DocumentObjectGroupPython] Ag_element004  label="Ag_element : 0.574"  # scripted group (container) (typed FeaturePython)
  n = 0.573748
FEATURE [App::DocumentObjectGroupPython] I_element007  label="I_element : 0.649"  # scripted group (container) (typed FeaturePython)
  n = 0.003357
FEATURE [App::DocumentObjectGroupPython] G4_SILVER_HALIDES  # scripted group (container) (typed FeaturePython)
  Dunit = g/cm3
  Dvalue = 6.47
  Group = -> [Br_element006,Ag_element004,I_element007]
  conduct = 2
  density = 1
  expand = 3
  formula = G4_SILVER_HALIDES
  name = G4_SILVER_HALIDES
  specific = 4
FEATURE [App::DocumentObjectGroupPython] Ag_element005  label="Ag_element : 003"  # scripted group (container) (typed FeaturePython)
  n = 1
  ref = Ag_element
FEATURE [App::DocumentObjectGroupPython] I_element008  label="I_element : 004"  # scripted group (container) (typed FeaturePython)
  n = 1
  ref = I_element
FEATURE [App::DocumentObjectGroupPython] G4_SILVER_IODIDE  # scripted group (container) (typed FeaturePython)
  Dunit = g/cm3
  Dvalue = 6.01
  Group = -> [Ag_element005,I_element008]
  conduct = 2
  density = 1
  expand = 3
  formula = G4_SILVER_IODIDE
  name = G4_SILVER_IODIDE
  specific = 4
FEATURE [App::DocumentObjectGroupPython] H_element095  label="H_element : 0.100"  # scripted group (container) (typed FeaturePython)
  n = 0.1
FEATURE [App::DocumentObjectGroupPython] C_element103  label="C_element : 0.204"  # scripted group (container) (typed FeaturePython)
  n = 0.204
FEATURE [App::DocumentObjectGroupPython] N_element039  label="N_element : 0.759"  # scripted group (container) (typed FeaturePython)
  n = 0.042
FEATURE [App::DocumentObjectGroupPython] O_element088  label="O_element : 0.645"  # scripted group (container) (typed FeaturePython)
  n = 0.645
FEATURE [App::DocumentObjectGroupPython] Na_element013  label="Na_element : 0.100"  # scripted group (container) (typed FeaturePython)
  n = 0.002
FEATURE [App::DocumentObjectGroupPython] P_element009  label="P_element : 0.107"  # scripted group (container) (typed FeaturePython)
  n = 0.001
FEATURE [App::DocumentObjectGroupPython] S_element020  label="S_element : 0.021"  # scripted group (container) (typed FeaturePython)
  n = 0.002
FEATURE [App::DocumentObjectGroupPython] Cl_element023  label="Cl_element : 0.590"  # scripted group (container) (typed FeaturePython)
  n = 0.003
FEATURE [App::DocumentObjectGroupPython] K_element010  label="K_element : 0.001"  # scripted group (container) (typed FeaturePython)
  n = 0.001
FEATURE [App::DocumentObjectGroupPython] G4_SKIN_ICRP  # scripted group (container) (typed FeaturePython)
  Dunit = g/cm3
  Dvalue = 1.09
  Group = -> [H_element095,C_element103,N_element039,O_element088,Na_element013,P_element009,S_element020,Cl_element023,K_element010]
  conduct = 2
  density = 1
  expand = 3
  formula = G4_SKIN_ICRP
  name = G4_SKIN_ICRP
  specific = 4
FEATURE [App::DocumentObjectGroupPython] Na_element014  label="Na_element : 2"  # scripted group (container) (typed FeaturePython)
  n = 2
  ref = Na_element
FEATURE [App::DocumentObjectGroupPython] C_element104  label="C_element : 058"  # scripted group (container) (typed FeaturePython)
  n = 1
  ref = C_element
FEATURE [App::DocumentObjectGroupPython] O_element089  label="O_element : 049"  # scripted group (container) (typed FeaturePython)
  n = 3
  ref = O_element
FEATURE [App::DocumentObjectGroupPython] G4_SODIUM_CARBONATE  # scripted group (container) (typed FeaturePython)
  Dunit = g/cm3
  Dvalue = 2.532
  Group = -> [Na_element014,C_element104,O_element089]
  conduct = 2
  density = 1
  expand = 3
  formula = G4_SODIUM_CARBONATE
  name = G4_SODIUM_CARBONATE
  specific = 4
FEATURE [App::DocumentObjectGroupPython] Na_element015  label="Na_element : 1"  # scripted group (container) (typed FeaturePython)
  n = 1
  ref = Na_element
FEATURE [App::DocumentObjectGroupPython] I_element009  label="I_element : 005"  # scripted group (container) (typed FeaturePython)
  n = 1
  ref = I_element
FEATURE [App::DocumentObjectGroupPython] G4_SODIUM_IODIDE  # scripted group (container) (typed FeaturePython)
  Dunit = g/cm3
  Dvalue = 3.667
  Group = -> [Na_element015,I_element009]
  conduct = 2
  density = 1
  expand = 3
  formula = G4_SODIUM_IODIDE
  name = G4_SODIUM_IODIDE
  specific = 4
FEATURE [App::DocumentObjectGroupPython] Na_element016  label="Na_element : 003"  # scripted group (container) (typed FeaturePython)
  n = 2
  ref = Na_element
FEATURE [App::DocumentObjectGroupPython] O_element090  label="O_element : 050"  # scripted group (container) (typed FeaturePython)
  n = 1
  ref = O_element
FEATURE [App::DocumentObjectGroupPython] G4_SODIUM_MONOXIDE  # scripted group (container) (typed FeaturePython)
  Dunit = g/cm3
  Dvalue = 2.27
  Group = -> [Na_element016,O_element090]
  conduct = 2
  density = 1
  expand = 3
  formula = G4_SODIUM_MONOXIDE
  name = G4_SODIUM_MONOXIDE
  specific = 4
FEATURE [App::DocumentObjectGroupPython] Na_element017  label="Na_element : 004"  # scripted group (container) (typed FeaturePython)
  n = 1
  ref = Na_element
FEATURE [App::DocumentObjectGroupPython] N_element040  label="N_element : 018"  # scripted group (container) (typed FeaturePython)
  n = 1
  ref = N_element
FEATURE [App::DocumentObjectGroupPython] O_element091  label="O_element : 051"  # scripted group (container) (typed FeaturePython)
  n = 3
  ref = O_element
FEATURE [App::DocumentObjectGroupPython] G4_SODIUM_NITRATE  # scripted group (container) (typed FeaturePython)
  Dunit = g/cm3
  Dvalue = 2.261
  Group = -> [Na_element017,N_element040,O_element091]
  conduct = 2
  density = 1
  expand = 3
  formula = G4_SODIUM_NITRATE
  name = G4_SODIUM_NITRATE
  specific = 4
FEATURE [App::DocumentObjectGroupPython] C_element105  label="C_element : 059"  # scripted group (container) (typed FeaturePython)
  n = 14
  ref = C_element
FEATURE [App::DocumentObjectGroupPython] H_element096  label="H_element : 053"  # scripted group (container) (typed FeaturePython)
  n = 12
  ref = H_element
FEATURE [App::DocumentObjectGroupPython] G4_STILBENE  # scripted group (container) (typed FeaturePython)
  Dunit = g/cm3
  Dvalue = 0.9707
  Group = -> [C_element105,H_element096]
  conduct = 2
  density = 1
  expand = 3
  formula = G4_STILBENE
  name = G4_STILBENE
  specific = 4
FEATURE [App::DocumentObjectGroupPython] C_element106  label="C_element : 12"  # scripted group (container) (typed FeaturePython)
  n = 12
  ref = C_element
FEATURE [App::DocumentObjectGroupPython] H_element097  label="H_element : 22"  # scripted group (container) (typed FeaturePython)
  n = 22
  ref = H_element
FEATURE [App::DocumentObjectGroupPython] O_element092  label="O_element : 11"  # scripted group (container) (typed FeaturePython)
  n = 11
  ref = O_element
FEATURE [App::DocumentObjectGroupPython] G4_SUCROSE  # scripted group (container) (typed FeaturePython)
  Dunit = g/cm3
  Dvalue = 1.5805
  Group = -> [C_element106,H_element097,O_element092]
  conduct = 2
  density = 1
  expand = 3
  formula = G4_SUCROSE
  name = G4_SUCROSE
  specific = 4
FEATURE [App::DocumentObjectGroupPython] C_element107  label="C_element : 18"  # scripted group (container) (typed FeaturePython)
  n = 18
  ref = C_element
FEATURE [App::DocumentObjectGroupPython] H_element098  label="H_element : 054"  # scripted group (container) (typed FeaturePython)
  n = 14
  ref = H_element
FEATURE [App::DocumentObjectGroupPython] G4_TERPHENYL  # scripted group (container) (typed FeaturePython)
  Dunit = g/cm3
  Dvalue = 1.24
  Group = -> [C_element107,H_element098]
  conduct = 2
  density = 1
  expand = 3
  formula = G4_TERPHENYL
  name = G4_TERPHENYL
  specific = 4
FEATURE [App::DocumentObjectGroupPython] H_element099  label="H_element : 0.146"  # scripted group (container) (typed FeaturePython)
  n = 0.106
FEATURE [App::DocumentObjectGroupPython] C_element108  label="C_element : 0.883"  # scripted group (container) (typed FeaturePython)
  n = 0.099
FEATURE [App::DocumentObjectGroupPython] N_element041  label="N_element : 0.020"  # scripted group (container) (typed FeaturePython)
  n = 0.02
FEATURE [App::DocumentObjectGroupPython] O_element093  label="O_element : 0.766"  # scripted group (container) (typed FeaturePython)
  n = 0.766
FEATURE [App::DocumentObjectGroupPython] Na_element018  label="Na_element : 0.101"  # scripted group (container) (typed FeaturePython)
  n = 0.002
FEATURE [App::DocumentObjectGroupPython] P_element010  label="P_element : 0.108"  # scripted group (container) (typed FeaturePython)
  n = 0.001
FEATURE [App::DocumentObjectGroupPython] S_element021  label="S_element : 0.022"  # scripted group (container) (typed FeaturePython)
  n = 0.002
FEATURE [App::DocumentObjectGroupPython] Cl_element024  label="Cl_element : 0.002"  # scripted group (container) (typed FeaturePython)
  n = 0.002
FEATURE [App::DocumentObjectGroupPython] K_element011  label="K_element : 0.017"  # scripted group (container) (typed FeaturePython)
  n = 0.002
FEATURE [App::DocumentObjectGroupPython] G4_TESTIS_ICRP  # scripted group (container) (typed FeaturePython)
  Dunit = g/cm3
  Dvalue = 1.04
  Group = -> [H_element099,C_element108,N_element041,O_element093,Na_element018,P_element010,S_element021,Cl_element024,K_element011]
  conduct = 2
  density = 1
  expand = 3
  formula = G4_TESTIS_ICRP
  name = G4_TESTIS_ICRP
  specific = 4
FEATURE [App::DocumentObjectGroupPython] C_element109  label="C_element : 060"  # scripted group (container) (typed FeaturePython)
  n = 2
  ref = C_element
FEATURE [App::DocumentObjectGroupPython] Cl_element025  label="Cl_element : 012"  # scripted group (container) (typed FeaturePython)
  n = 4
  ref = Cl_element
FEATURE [App::DocumentObjectGroupPython] G4_TETRACHLOROETHYLENE  # scripted group (container) (typed FeaturePython)
  Dunit = g/cm3
  Dvalue = 1.625
  Group = -> [C_element109,Cl_element025]
  conduct = 2
  density = 1
  expand = 3
  formula = G4_TETRACHLOROETHYLENE
  name = G4_TETRACHLOROETHYLENE
  specific = 4
FEATURE [App::DocumentObjectGroupPython] Tl_element001  label="Tl_element : 1"  # scripted group (container) (typed FeaturePython)
  n = 1
  ref = Tl_element
FEATURE [App::DocumentObjectGroupPython] Cl_element026  label="Cl_element : 013"  # scripted group (container) (typed FeaturePython)
  n = 1
  ref = Cl_element
FEATURE [App::DocumentObjectGroupPython] G4_THALLIUM_CHLORIDE  # scripted group (container) (typed FeaturePython)
  Dunit = g/cm3
  Dvalue = 7.004
  Group = -> [Tl_element001,Cl_element026]
  conduct = 2
  density = 1
  expand = 3
  formula = G4_THALLIUM_CHLORIDE
  name = G4_THALLIUM_CHLORIDE
  specific = 4
FEATURE [App::DocumentObjectGroupPython] H_element100  label="H_element : 0.147"  # scripted group (container) (typed FeaturePython)
  n = 0.105
FEATURE [App::DocumentObjectGroupPython] C_element110  label="C_element : 0.256"  # scripted group (container) (typed FeaturePython)
  n = 0.256
FEATURE [App::DocumentObjectGroupPython] N_element042  label="N_element : 0.760"  # scripted group (container) (typed FeaturePython)
  n = 0.027
FEATURE [App::DocumentObjectGroupPython] O_element094  label="O_element : 0.602"  # scripted group (container) (typed FeaturePython)
  n = 0.602
FEATURE [App::DocumentObjectGroupPython] Na_element019  label="Na_element : 0.102"  # scripted group (container) (typed FeaturePython)
  n = 0.001
FEATURE [App::DocumentObjectGroupPython] P_element011  label="P_element : 0.109"  # scripted group (container) (typed FeaturePython)
  n = 0.002
FEATURE [App::DocumentObjectGroupPython] S_element022  label="S_element : 0.023"  # scripted group (container) (typed FeaturePython)
  n = 0.003
FEATURE [App::DocumentObjectGroupPython] Cl_element027  label="Cl_element : 0.591"  # scripted group (container) (typed FeaturePython)
  n = 0.002
FEATURE [App::DocumentObjectGroupPython] K_element012  label="K_element : 0.018"  # scripted group (container) (typed FeaturePython)
  n = 0.002
FEATURE [App::DocumentObjectGroupPython] G4_TISSUE_SOFT_ICRP  # scripted group (container) (typed FeaturePython)
  Dunit = g/cm3
  Dvalue = 1.03
  Group = -> [H_element100,C_element110,N_element042,O_element094,Na_element019,P_element011,S_element022,Cl_element027,K_element012]
  conduct = 2
  density = 1
  expand = 3
  formula = G4_TISSUE_SOFT_ICRP
  name = G4_TISSUE_SOFT_ICRP
  specific = 4
FEATURE [App::DocumentObjectGroupPython] H_element101  label="H_element : 0.148"  # scripted group (container) (typed FeaturePython)
  n = 0.101
FEATURE [App::DocumentObjectGroupPython] C_element111  label="C_element : 0.111"  # scripted group (container) (typed FeaturePython)
  n = 0.111
FEATURE [App::DocumentObjectGroupPython] N_element043  label="N_element : 0.026"  # scripted group (container) (typed FeaturePython)
  n = 0.026
FEATURE [App::DocumentObjectGroupPython] O_element095  label="O_element : 0.762"  # scripted group (container) (typed FeaturePython)
  n = 0.762
FEATURE [App::DocumentObjectGroupPython] G4_TISSUE_SOFT_ICRU_4  label="G4_TISSUE_SOFT_ICRU-4"  # scripted group (container) (typed FeaturePython)
  Dunit = g/cm3
  Dvalue = 1
  Group = -> [H_element101,C_element111,N_element043,O_element095]
  conduct = 2
  density = 1
  expand = 3
  formula = G4_TISSUE_SOFT_ICRU-4
  name = G4_TISSUE_SOFT_ICRU-4
  specific = 4
FEATURE [App::DocumentObjectGroupPython] H_element102  label="H_element : 0.149"  # scripted group (container) (typed FeaturePython)
  n = 0.101869
FEATURE [App::DocumentObjectGroupPython] C_element112  label="C_element : 0.456"  # scripted group (container) (typed FeaturePython)
  n = 0.456179
FEATURE [App::DocumentObjectGroupPython] N_element044  label="N_element : 0.761"  # scripted group (container) (typed FeaturePython)
  n = 0.035172
FEATURE [App::DocumentObjectGroupPython] O_element096  label="O_element : 0.407"  # scripted group (container) (typed FeaturePython)
  n = 0.40678
FEATURE [App::DocumentObjectGroupPython] G4_TISSUE_METHANE  label="G4_TISSUE-METHANE"  # scripted group (container) (typed FeaturePython)
  Dunit = g/cm3
  Dvalue = 0.00106409
  Group = -> [H_element102,C_element112,N_element044,O_element096]
  conduct = 2
  density = 1
  expand = 3
  formula = G4_TISSUE-METHANE
  name = G4_TISSUE-METHANE
  specific = 4
FEATURE [App::DocumentObjectGroupPython] H_element103  label="H_element : 0.103"  # scripted group (container) (typed FeaturePython)
  n = 0.102672
FEATURE [App::DocumentObjectGroupPython] C_element113  label="C_element : 0.569"  # scripted group (container) (typed FeaturePython)
  n = 0.56894
FEATURE [App::DocumentObjectGroupPython] N_element045  label="N_element : 0.762"  # scripted group (container) (typed FeaturePython)
  n = 0.035022
FEATURE [App::DocumentObjectGroupPython] O_element097  label="O_element : 0.293"  # scripted group (container) (typed FeaturePython)
  n = 0.293366
FEATURE [App::DocumentObjectGroupPython] G4_TISSUE_PROPANE  label="G4_TISSUE-PROPANE"  # scripted group (container) (typed FeaturePython)
  Dunit = g/cm3
  Dvalue = 0.00182628
  Group = -> [H_element103,C_element113,N_element045,O_element097]
  conduct = 2
  density = 1
  expand = 3
  formula = G4_TISSUE-PROPANE
  name = G4_TISSUE-PROPANE
  specific = 4
FEATURE [App::DocumentObjectGroupPython] Ti_element003  label="Ti_element : 1"  # scripted group (container) (typed FeaturePython)
  n = 1
  ref = Ti_element
FEATURE [App::DocumentObjectGroupPython] O_element098  label="O_element : 052"  # scripted group (container) (typed FeaturePython)
  n = 2
  ref = O_element
FEATURE [App::DocumentObjectGroupPython] G4_TITANIUM_DIOXIDE  # scripted group (container) (typed FeaturePython)
  Dunit = g/cm3
  Dvalue = 4.26
  Group = -> [Ti_element003,O_element098]
  conduct = 2
  density = 1
  expand = 3
  formula = G4_TITANIUM_DIOXIDE
  name = G4_TITANIUM_DIOXIDE
  specific = 4
FEATURE [App::DocumentObjectGroupPython] C_element114  label="C_element : 061"  # scripted group (container) (typed FeaturePython)
  n = 7
  ref = C_element
FEATURE [App::DocumentObjectGroupPython] H_element104  label="H_element : 055"  # scripted group (container) (typed FeaturePython)
  n = 8
  ref = H_element
FEATURE [App::DocumentObjectGroupPython] G4_TOLUENE  # scripted group (container) (typed FeaturePython)
  Dunit = g/cm3
  Dvalue = 0.8669
  Group = -> [C_element114,H_element104]
  conduct = 2
  density = 1
  expand = 3
  formula = G4_TOLUENE
  name = G4_TOLUENE
  specific = 4
FEATURE [App::DocumentObjectGroupPython] C_element115  label="C_element : 062"  # scripted group (container) (typed FeaturePython)
  n = 2
  ref = C_element
FEATURE [App::DocumentObjectGroupPython] H_element105  label="H_element : 056"  # scripted group (container) (typed FeaturePython)
  n = 1
  ref = H_element
FEATURE [App::DocumentObjectGroupPython] Cl_element028  label="Cl_element : 014"  # scripted group (container) (typed FeaturePython)
  n = 3
  ref = Cl_element
FEATURE [App::DocumentObjectGroupPython] G4_TRICHLOROETHYLENE  # scripted group (container) (typed FeaturePython)
  Dunit = g/cm3
  Dvalue = 1.46
  Group = -> [C_element115,H_element105,Cl_element028]
  conduct = 2
  density = 1
  expand = 3
  formula = G4_TRICHLOROETHYLENE
  name = G4_TRICHLOROETHYLENE
  specific = 4
FEATURE [App::DocumentObjectGroupPython] C_element116  label="C_element : 063"  # scripted group (container) (typed FeaturePython)
  n = 6
  ref = C_element
FEATURE [App::DocumentObjectGroupPython] H_element106  label="H_element : 15"  # scripted group (container) (typed FeaturePython)
  n = 15
  ref = H_element
FEATURE [App::DocumentObjectGroupPython] O_element099  label="O_element : 053"  # scripted group (container) (typed FeaturePython)
  n = 4
  ref = O_element
FEATURE [App::DocumentObjectGroupPython] P_element012  label="P_element : 1"  # scripted group (container) (typed FeaturePython)
  n = 1
  ref = P_element
FEATURE [App::DocumentObjectGroupPython] G4_TRIETHYL_PHOSPHATE  # scripted group (container) (typed FeaturePython)
  Dunit = g/cm3
  Dvalue = 1.07
  Group = -> [C_element116,H_element106,O_element099,P_element012]
  conduct = 2
  density = 1
  expand = 3
  formula = G4_TRIETHYL_PHOSPHATE
  name = G4_TRIETHYL_PHOSPHATE
  specific = 4
FEATURE [App::DocumentObjectGroupPython] W_element003  label="W_element : 003"  # scripted group (container) (typed FeaturePython)
  n = 1
  ref = W_element
FEATURE [App::DocumentObjectGroupPython] F_element017  label="F_element : 6"  # scripted group (container) (typed FeaturePython)
  n = 6
  ref = F_element
FEATURE [App::DocumentObjectGroupPython] G4_TUNGSTEN_HEXAFLUORIDE  # scripted group (container) (typed FeaturePython)
  Dunit = g/cm3
  Dvalue = 2.4
  Group = -> [W_element003,F_element017]
  conduct = 2
  density = 1
  expand = 3
  formula = G4_TUNGSTEN_HEXAFLUORIDE
  name = G4_TUNGSTEN_HEXAFLUORIDE
  specific = 4
FEATURE [App::DocumentObjectGroupPython] U_element001  label="U_element : 1"  # scripted group (container) (typed FeaturePython)
  n = 1
  ref = U_element
FEATURE [App::DocumentObjectGroupPython] C_element117  label="C_element : 064"  # scripted group (container) (typed FeaturePython)
  n = 2
  ref = C_element
FEATURE [App::DocumentObjectGroupPython] G4_URANIUM_DICARBIDE  # scripted group (container) (typed FeaturePython)
  Dunit = g/cm3
  Dvalue = 11.28
  Group = -> [U_element001,C_element117]
  conduct = 2
  density = 1
  expand = 3
  formula = G4_URANIUM_DICARBIDE
  name = G4_URANIUM_DICARBIDE
  specific = 4
FEATURE [App::DocumentObjectGroupPython] U_element002  label="U_element : 002"  # scripted group (container) (typed FeaturePython)
  n = 1
  ref = U_element
FEATURE [App::DocumentObjectGroupPython] C_element118  label="C_element : 065"  # scripted group (container) (typed FeaturePython)
  n = 1
  ref = C_element
FEATURE [App::DocumentObjectGroupPython] G4_URANIUM_MONOCARBIDE  # scripted group (container) (typed FeaturePython)
  Dunit = g/cm3
  Dvalue = 13.63
  Group = -> [U_element002,C_element118]
  conduct = 2
  density = 1
  expand = 3
  formula = G4_URANIUM_MONOCARBIDE
  name = G4_URANIUM_MONOCARBIDE
  specific = 4
FEATURE [App::DocumentObjectGroupPython] U_element003  label="U_element : 003"  # scripted group (container) (typed FeaturePython)
  n = 1
  ref = U_element
FEATURE [App::DocumentObjectGroupPython] O_element100  label="O_element : 054"  # scripted group (container) (typed FeaturePython)
  n = 2
  ref = O_element
FEATURE [App::DocumentObjectGroupPython] G4_URANIUM_OXIDE  # scripted group (container) (typed FeaturePython)
  Dunit = g/cm3
  Dvalue = 10.96
  Group = -> [U_element003,O_element100]
  conduct = 2
  density = 1
  expand = 3
  formula = G4_URANIUM_OXIDE
  name = G4_URANIUM_OXIDE
  specific = 4
FEATURE [App::DocumentObjectGroupPython] C_element119  label="C_element : 066"  # scripted group (container) (typed FeaturePython)
  n = 1
  ref = C_element
FEATURE [App::DocumentObjectGroupPython] H_element107  label="H_element : 057"  # scripted group (container) (typed FeaturePython)
  n = 4
  ref = H_element
FEATURE [App::DocumentObjectGroupPython] N_element046  label="N_element : 019"  # scripted group (container) (typed FeaturePython)
  n = 2
  ref = N_element
FEATURE [App::DocumentObjectGroupPython] O_element101  label="O_element : 055"  # scripted group (container) (typed FeaturePython)
  n = 1
  ref = O_element
FEATURE [App::DocumentObjectGroupPython] G4_UREA  # scripted group (container) (typed FeaturePython)
  Dunit = g/cm3
  Dvalue = 1.323
  Group = -> [C_element119,H_element107,N_element046,O_element101]
  conduct = 2
  density = 1
  expand = 3
  formula = G4_UREA
  name = G4_UREA
  specific = 4
FEATURE [App::DocumentObjectGroupPython] C_element120  label="C_element : 067"  # scripted group (container) (typed FeaturePython)
  n = 5
  ref = C_element
FEATURE [App::DocumentObjectGroupPython] H_element108  label="H_element : 058"  # scripted group (container) (typed FeaturePython)
  n = 11
  ref = H_element
FEATURE [App::DocumentObjectGroupPython] N_element047  label="N_element : 020"  # scripted group (container) (typed FeaturePython)
  n = 1
  ref = N_element
FEATURE [App::DocumentObjectGroupPython] O_element102  label="O_element : 056"  # scripted group (container) (typed FeaturePython)
  n = 2
  ref = O_element
FEATURE [App::DocumentObjectGroupPython] G4_VALINE  # scripted group (container) (typed FeaturePython)
  Dunit = g/cm3
  Dvalue = 1.23
  Group = -> [C_element120,H_element108,N_element047,O_element102]
  conduct = 2
  density = 1
  expand = 3
  formula = G4_VALINE
  name = G4_VALINE
  specific = 4
FEATURE [App::DocumentObjectGroupPython] H_element109  label="H_element : 0.009"  # scripted group (container) (typed FeaturePython)
  n = 0.009417
FEATURE [App::DocumentObjectGroupPython] C_element121  label="C_element : 0.281"  # scripted group (container) (typed FeaturePython)
  n = 0.280555
FEATURE [App::DocumentObjectGroupPython] F_element018  label="F_element : 0.710"  # scripted group (container) (typed FeaturePython)
  n = 0.710028
FEATURE [App::DocumentObjectGroupPython] G4_VITON  # scripted group (container) (typed FeaturePython)
  Dunit = g/cm3
  Dvalue = 1.8
  Group = -> [H_element109,C_element121,F_element018]
  conduct = 2
  density = 1
  expand = 3
  formula = G4_VITON
  name = G4_VITON
  specific = 4
FEATURE [App::DocumentObjectGroupPython] H_element110  label="H_element : 059"  # scripted group (container) (typed FeaturePython)
  n = 2
  ref = H_element
FEATURE [App::DocumentObjectGroupPython] O_element103  label="O_element : 057"  # scripted group (container) (typed FeaturePython)
  n = 1
  ref = O_element
FEATURE [App::DocumentObjectGroupPython] G4_WATER  # scripted group (container) (typed FeaturePython)
  Dunit = g/cm3
  Dvalue = 1
  Group = -> [H_element110,O_element103]
  conduct = 2
  density = 1
  expand = 3
  formula = G4_WATER
  name = G4_WATER
  specific = 4
FEATURE [App::DocumentObjectGroupPython] H_element111  label="H_element : 060"  # scripted group (container) (typed FeaturePython)
  n = 2
  ref = H_element
FEATURE [App::DocumentObjectGroupPython] O_element104  label="O_element : 058"  # scripted group (container) (typed FeaturePython)
  n = 1
  ref = O_element
FEATURE [App::DocumentObjectGroupPython] G4_WATER_VAPOR  # scripted group (container) (typed FeaturePython)
  Dunit = g/cm3
  Dvalue = 0.000756182
  Group = -> [H_element111,O_element104]
  conduct = 2
  density = 1
  expand = 3
  formula = G4_WATER_VAPOR
  name = G4_WATER_VAPOR
  specific = 4
FEATURE [App::DocumentObjectGroupPython] C_element122  label="C_element : 068"  # scripted group (container) (typed FeaturePython)
  n = 8
  ref = C_element
FEATURE [App::DocumentObjectGroupPython] H_element112  label="H_element : 061"  # scripted group (container) (typed FeaturePython)
  n = 10
  ref = H_element
FEATURE [App::DocumentObjectGroupPython] G4_XYLENE  # scripted group (container) (typed FeaturePython)
  Dunit = g/cm3
  Dvalue = 0.87
  Group = -> [C_element122,H_element112]
  conduct = 2
  density = 1
  expand = 3
  formula = G4_XYLENE
  name = G4_XYLENE
  specific = 4
FEATURE [App::DocumentObjectGroupPython] C_element123  label="C_element : 069"  # scripted group (container) (typed FeaturePython)
  n = 1
  ref = C_element
FEATURE [App::DocumentObjectGroupPython] G4_GRAPHITE  # scripted group (container) (typed FeaturePython)
  Dunit = g/cm3
  Dvalue = 2.21
  Group = -> [C_element123]
  conduct = 2
  density = 1
  expand = 3
  formula = G4_GRAPHITE
  name = G4_GRAPHITE
  specific = 4
FEATURE [App::DocumentObjectGroupPython] NIST  # scripted group (container) (typed FeaturePython)
  Group = -> [G4_A_150_TISSUE,G4_ACETONE,G4_ACETYLENE,G4_ADENINE,G4_ADIPOSE_TISSUE_ICRP,G4_AIR,G4_ALANINE,G4_ALUMINUM_OXIDE,G4_AMBER,G4_AMMONIA,G4_ANILINE,G4_ANTHRACENE,G4_B_100_BONE,G4_BAKELITE,G4_BARIUM_FLUORIDE,G4_BARIUM_SULFATE,G4_BENZENE,G4_BERYLLIUM_OXIDE,G4_BGO,G4_BLOOD_ICRP,G4_BONE_COMPACT_ICRU,G4_BONE_CORTICAL_ICRP,G4_BORON_CARBIDE,G4_BORON_OXIDE,G4_BRAIN_ICRP,G4_BUTANE,G4_N_BUTYL_ALCOHOL,G4_C_552,+152 more]
FEATURE [App::DocumentObjectGroupPython] H_element113  label="H_element : 062"  # scripted group (container) (typed FeaturePython)
  n = 1
  ref = H_element
FEATURE [App::DocumentObjectGroupPython] G4_H  # scripted group (container) (typed FeaturePython)
  Dunit = g/cm3
  Dvalue = 8.3748e-05
  Group = -> [H_element113]
  conduct = 2
  density = 1
  expand = 3
  formula = H
  name = G4_H
  specific = 4
FEATURE [App::DocumentObjectGroupPython] He_element001  label="He_element : 1"  # scripted group (container) (typed FeaturePython)
  n = 1
  ref = He_element
FEATURE [App::DocumentObjectGroupPython] G4_He  # scripted group (container) (typed FeaturePython)
  Dunit = g/cm3
  Dvalue = 0.000166322
  Group = -> [He_element001]
  conduct = 2
  density = 1
  expand = 3
  formula = He
  name = G4_He
  specific = 4
FEATURE [App::DocumentObjectGroupPython] Li_element008  label="Li_element : 008"  # scripted group (container) (typed FeaturePython)
  n = 1
  ref = Li_element
FEATURE [App::DocumentObjectGroupPython] G4_Li  # scripted group (container) (typed FeaturePython)
  Dunit = g/cm3
  Dvalue = 0.534
  Group = -> [Li_element008]
  conduct = 2
  density = 1
  expand = 3
  formula = Li
  name = G4_Li
  specific = 4
FEATURE [App::DocumentObjectGroupPython] Be_element002  label="Be_element : 002"  # scripted group (container) (typed FeaturePython)
  n = 1
  ref = Be_element
FEATURE [App::DocumentObjectGroupPython] G4_Be  # scripted group (container) (typed FeaturePython)
  Dunit = g/cm3
  Dvalue = 1.848
  Group = -> [Be_element002]
  conduct = 2
  density = 1
  expand = 3
  formula = Be
  name = G4_Be
  specific = 4
FEATURE [App::DocumentObjectGroupPython] B_element007  label="B_element : 007"  # scripted group (container) (typed FeaturePython)
  n = 1
  ref = B_element
FEATURE [App::DocumentObjectGroupPython] G4_B  # scripted group (container) (typed FeaturePython)
  Dunit = g/cm3
  Dvalue = 2.37
  Group = -> [B_element007]
  conduct = 2
  density = 1
  expand = 3
  formula = B
  name = G4_B
  specific = 4
FEATURE [App::DocumentObjectGroupPython] C_element124  label="C_element : 070"  # scripted group (container) (typed FeaturePython)
  n = 1
  ref = C_element
FEATURE [App::DocumentObjectGroupPython] G4_C  # scripted group (container) (typed FeaturePython)
  Dunit = g/cm3
  Dvalue = 2
  Group = -> [C_element124]
  conduct = 2
  density = 1
  expand = 3
  formula = C
  name = G4_C
  specific = 4
FEATURE [App::DocumentObjectGroupPython] N_element048  label="N_element : 021"  # scripted group (container) (typed FeaturePython)
  n = 1
  ref = N_element
FEATURE [App::DocumentObjectGroupPython] G4_N  # scripted group (container) (typed FeaturePython)
  Dunit = g/cm3
  Dvalue = 0.0011652
  Group = -> [N_element048]
  conduct = 2
  density = 1
  expand = 3
  formula = N
  name = G4_N
  specific = 4
FEATURE [App::DocumentObjectGroupPython] O_element105  label="O_element : 059"  # scripted group (container) (typed FeaturePython)
  n = 1
  ref = O_element
FEATURE [App::DocumentObjectGroupPython] G4_O  # scripted group (container) (typed FeaturePython)
  Dunit = g/cm3
  Dvalue = 0.00133151
  Group = -> [O_element105]
  conduct = 2
  density = 1
  expand = 3
  formula = O
  name = G4_O
  specific = 4
FEATURE [App::DocumentObjectGroupPython] F_element019  label="F_element : 008"  # scripted group (container) (typed FeaturePython)
  n = 1
  ref = F_element
FEATURE [App::DocumentObjectGroupPython] G4_F  # scripted group (container) (typed FeaturePython)
  Dunit = g/cm3
  Dvalue = 0.00158029
  Group = -> [F_element019]
  conduct = 2
  density = 1
  expand = 3
  formula = F
  name = G4_F
  specific = 4
FEATURE [App::DocumentObjectGroupPython] Ne_element001  label="Ne_element : 1"  # scripted group (container) (typed FeaturePython)
  n = 1
  ref = Ne_element
FEATURE [App::DocumentObjectGroupPython] G4_Ne  # scripted group (container) (typed FeaturePython)
  Dunit = g/cm3
  Dvalue = 0.000838505
  Group = -> [Ne_element001]
  conduct = 2
  density = 1
  expand = 3
  formula = Ne
  name = G4_Ne
  specific = 4
FEATURE [App::DocumentObjectGroupPython] Na_element020  label="Na_element : 005"  # scripted group (container) (typed FeaturePython)
  n = 1
  ref = Na_element
FEATURE [App::DocumentObjectGroupPython] G4_Na  # scripted group (container) (typed FeaturePython)
  Dunit = g/cm3
  Dvalue = 0.971
  Group = -> [Na_element020]
  conduct = 2
  density = 1
  expand = 3
  formula = Na
  name = G4_Na
  specific = 4
FEATURE [App::DocumentObjectGroupPython] Mg_element011  label="Mg_element : 005"  # scripted group (container) (typed FeaturePython)
  n = 1
  ref = Mg_element
FEATURE [App::DocumentObjectGroupPython] G4_Mg  # scripted group (container) (typed FeaturePython)
  Dunit = g/cm3
  Dvalue = 1.74
  Group = -> [Mg_element011]
  conduct = 2
  density = 1
  expand = 3
  formula = Mg
  name = G4_Mg
  specific = 4
FEATURE [App::DocumentObjectGroupPython] Al_element004  label="Al_element : 1"  # scripted group (container) (typed FeaturePython)
  n = 1
  ref = Al_element
FEATURE [App::DocumentObjectGroupPython] G4_Al  # scripted group (container) (typed FeaturePython)
  Dunit = g/cm3
  Dvalue = 2.699
  Group = -> [Al_element004]
  conduct = 2
  density = 1
  expand = 3
  formula = Al
  name = G4_Al
  specific = 4
FEATURE [App::DocumentObjectGroupPython] Si_element007  label="Si_element : 002"  # scripted group (container) (typed FeaturePython)
  n = 1
  ref = Si_element
FEATURE [App::DocumentObjectGroupPython] G4_Si  # scripted group (container) (typed FeaturePython)
  Dunit = g/cm3
  Dvalue = 2.33
  Group = -> [Si_element007]
  conduct = 2
  density = 1
  expand = 3
  formula = Si
  name = G4_Si
  specific = 4
FEATURE [App::DocumentObjectGroupPython] P_element013  label="P_element : 002"  # scripted group (container) (typed FeaturePython)
  n = 1
  ref = P_element
FEATURE [App::DocumentObjectGroupPython] G4_P  # scripted group (container) (typed FeaturePython)
  Dunit = g/cm3
  Dvalue = 2.2
  Group = -> [P_element013]
  conduct = 2
  density = 1
  expand = 3
  formula = P
  name = G4_P
  specific = 4
FEATURE [App::DocumentObjectGroupPython] S_element023  label="S_element : 007"  # scripted group (container) (typed FeaturePython)
  n = 1
  ref = S_element
FEATURE [App::DocumentObjectGroupPython] G4_S  # scripted group (container) (typed FeaturePython)
  Dunit = g/cm3
  Dvalue = 2
  Group = -> [S_element023]
  conduct = 2
  density = 1
  expand = 3
  formula = S
  name = G4_S
  specific = 4
FEATURE [App::DocumentObjectGroupPython] Cl_element029  label="Cl_element : 015"  # scripted group (container) (typed FeaturePython)
  n = 1
  ref = Cl_element
FEATURE [App::DocumentObjectGroupPython] G4_Cl  # scripted group (container) (typed FeaturePython)
  Dunit = g/cm3
  Dvalue = 0.00299473
  Group = -> [Cl_element029]
  conduct = 2
  density = 1
  expand = 3
  formula = Cl
  name = G4_Cl
  specific = 4
FEATURE [App::DocumentObjectGroupPython] Ar_element002  label="Ar_element : 1"  # scripted group (container) (typed FeaturePython)
  n = 1
  ref = Ar_element
FEATURE [App::DocumentObjectGroupPython] G4_Ar  # scripted group (container) (typed FeaturePython)
  Dunit = g/cm3
  Dvalue = 0.00166201
  Group = -> [Ar_element002]
  conduct = 2
  density = 1
  expand = 3
  formula = Ar
  name = G4_Ar
  specific = 4
FEATURE [App::DocumentObjectGroupPython] K_element013  label="K_element : 003"  # scripted group (container) (typed FeaturePython)
  n = 1
  ref = K_element
FEATURE [App::DocumentObjectGroupPython] G4_K  # scripted group (container) (typed FeaturePython)
  Dunit = g/cm3
  Dvalue = 0.862
  Group = -> [K_element013]
  conduct = 2
  density = 1
  expand = 3
  formula = K
  name = G4_K
  specific = 4
FEATURE [App::DocumentObjectGroupPython] Ca_element014  label="Ca_element : 007"  # scripted group (container) (typed FeaturePython)
  n = 1
  ref = Ca_element
FEATURE [App::DocumentObjectGroupPython] G4_Ca  # scripted group (container) (typed FeaturePython)
  Dunit = g/cm3
  Dvalue = 1.55
  Group = -> [Ca_element014]
  conduct = 2
  density = 1
  expand = 3
  formula = Ca
  name = G4_Ca
  specific = 4
FEATURE [App::DocumentObjectGroupPython] Sc_element001  label="Sc_element : 1"  # scripted group (container) (typed FeaturePython)
  n = 1
  ref = Sc_element
FEATURE [App::DocumentObjectGroupPython] G4_Sc  # scripted group (container) (typed FeaturePython)
  Dunit = g/cm3
  Dvalue = 2.989
  Group = -> [Sc_element001]
  conduct = 2
  density = 1
  expand = 3
  formula = Sc
  name = G4_Sc
  specific = 4
FEATURE [App::DocumentObjectGroupPython] Ti_element004  label="Ti_element : 002"  # scripted group (container) (typed FeaturePython)
  n = 1
  ref = Ti_element
FEATURE [App::DocumentObjectGroupPython] G4_Ti  # scripted group (container) (typed FeaturePython)
  Dunit = g/cm3
  Dvalue = 4.54
  Group = -> [Ti_element004]
  conduct = 2
  density = 1
  expand = 3
  formula = Ti
  name = G4_Ti
  specific = 4
FEATURE [App::DocumentObjectGroupPython] V_element001  label="V_element : 1"  # scripted group (container) (typed FeaturePython)
  n = 1
  ref = V_element
FEATURE [App::DocumentObjectGroupPython] G4_V  # scripted group (container) (typed FeaturePython)
  Dunit = g/cm3
  Dvalue = 6.11
  Group = -> [V_element001]
  conduct = 2
  density = 1
  expand = 3
  formula = V
  name = G4_V
  specific = 4
FEATURE [App::DocumentObjectGroupPython] Cr_element001  label="Cr_element : 1"  # scripted group (container) (typed FeaturePython)
  n = 1
  ref = Cr_element
FEATURE [App::DocumentObjectGroupPython] G4_Cr  # scripted group (container) (typed FeaturePython)
  Dunit = g/cm3
  Dvalue = 7.18
  Group = -> [Cr_element001]
  conduct = 2
  density = 1
  expand = 3
  formula = Cr
  name = G4_Cr
  specific = 4
FEATURE [App::DocumentObjectGroupPython] Mn_element001  label="Mn_element : 1"  # scripted group (container) (typed FeaturePython)
  n = 1
  ref = Mn_element
FEATURE [App::DocumentObjectGroupPython] G4_Mn  # scripted group (container) (typed FeaturePython)
  Dunit = g/cm3
  Dvalue = 7.44
  Group = -> [Mn_element001]
  conduct = 2
  density = 1
  expand = 3
  formula = Mn
  name = G4_Mn
  specific = 4
FEATURE [App::DocumentObjectGroupPython] Fe_element007  label="Fe_element : 004"  # scripted group (container) (typed FeaturePython)
  n = 1
  ref = Fe_element
FEATURE [App::DocumentObjectGroupPython] G4_Fe  # scripted group (container) (typed FeaturePython)
  Dunit = g/cm3
  Dvalue = 7.874
  Group = -> [Fe_element007]
  conduct = 2
  density = 1
  expand = 3
  formula = Fe
  name = G4_Fe
  specific = 4
FEATURE [App::DocumentObjectGroupPython] Co_element001  label="Co_element : 1"  # scripted group (container) (typed FeaturePython)
  n = 1
  ref = Co_element
FEATURE [App::DocumentObjectGroupPython] G4_Co  # scripted group (container) (typed FeaturePython)
  Dunit = g/cm3
  Dvalue = 8.9
  Group = -> [Co_element001]
  conduct = 2
  density = 1
  expand = 3
  formula = Co
  name = G4_Co
  specific = 4
FEATURE [App::DocumentObjectGroupPython] Ni_element001  label="Ni_element : 1"  # scripted group (container) (typed FeaturePython)
  n = 1
  ref = Ni_element
FEATURE [App::DocumentObjectGroupPython] G4_Ni  # scripted group (container) (typed FeaturePython)
  Dunit = g/cm3
  Dvalue = 8.902
  Group = -> [Ni_element001]
  conduct = 2
  density = 1
  expand = 3
  formula = Ni
  name = G4_Ni
  specific = 4
FEATURE [App::DocumentObjectGroupPython] Cu_element001  label="Cu_element : 1"  # scripted group (container) (typed FeaturePython)
  n = 1
  ref = Cu_element
FEATURE [App::DocumentObjectGroupPython] G4_Cu  # scripted group (container) (typed FeaturePython)
  Dunit = g/cm3
  Dvalue = 8.96
  Group = -> [Cu_element001]
  conduct = 2
  density = 1
  expand = 3
  formula = Cu
  name = G4_Cu
  specific = 4
FEATURE [App::DocumentObjectGroupPython] Zn_element001  label="Zn_element : 1"  # scripted group (container) (typed FeaturePython)
  n = 1
  ref = Zn_element
FEATURE [App::DocumentObjectGroupPython] G4_Zn  # scripted group (container) (typed FeaturePython)
  Dunit = g/cm3
  Dvalue = 7.133
  Group = -> [Zn_element001]
  conduct = 2
  density = 1
  expand = 3
  formula = Zn
  name = G4_Zn
  specific = 4
FEATURE [App::DocumentObjectGroupPython] Ga_element002  label="Ga_element : 002"  # scripted group (container) (typed FeaturePython)
  n = 1
  ref = Ga_element
FEATURE [App::DocumentObjectGroupPython] G4_Ga  # scripted group (container) (typed FeaturePython)
  Dunit = g/cm3
  Dvalue = 5.904
  Group = -> [Ga_element002]
  conduct = 2
  density = 1
  expand = 3
  formula = Ga
  name = G4_Ga
  specific = 4
FEATURE [App::DocumentObjectGroupPython] Ge_element002  label="Ge_element : 1"  # scripted group (container) (typed FeaturePython)
  n = 1
  ref = Ge_element
FEATURE [App::DocumentObjectGroupPython] G4_Ge  # scripted group (container) (typed FeaturePython)
  Dunit = g/cm3
  Dvalue = 5.323
  Group = -> [Ge_element002]
  conduct = 2
  density = 1
  expand = 3
  formula = Ge
  name = G4_Ge
  specific = 4
FEATURE [App::DocumentObjectGroupPython] As_element003  label="As_element : 002"  # scripted group (container) (typed FeaturePython)
  n = 1
  ref = As_element
FEATURE [App::DocumentObjectGroupPython] G4_As  # scripted group (container) (typed FeaturePython)
  Dunit = g/cm3
  Dvalue = 5.73
  Group = -> [As_element003]
  conduct = 2
  density = 1
  expand = 3
  formula = As
  name = G4_As
  specific = 4
FEATURE [App::DocumentObjectGroupPython] Se_element001  label="Se_element : 1"  # scripted group (container) (typed FeaturePython)
  n = 1
  ref = Se_element
FEATURE [App::DocumentObjectGroupPython] G4_Se  # scripted group (container) (typed FeaturePython)
  Dunit = g/cm3
  Dvalue = 4.5
  Group = -> [Se_element001]
  conduct = 2
  density = 1
  expand = 3
  formula = Se
  name = G4_Se
  specific = 4
FEATURE [App::DocumentObjectGroupPython] Br_element007  label="Br_element : 004"  # scripted group (container) (typed FeaturePython)
  n = 1
  ref = Br_element
FEATURE [App::DocumentObjectGroupPython] G4_Br  # scripted group (container) (typed FeaturePython)
  Dunit = g/cm3
  Dvalue = 0.0070721
  Group = -> [Br_element007]
  conduct = 2
  density = 1
  expand = 3
  formula = Br
  name = G4_Br
  specific = 4
FEATURE [App::DocumentObjectGroupPython] Kr_element001  label="Kr_element : 1"  # scripted group (container) (typed FeaturePython)
  n = 1
  ref = Kr_element
FEATURE [App::DocumentObjectGroupPython] G4_Kr  # scripted group (container) (typed FeaturePython)
  Dunit = g/cm3
  Dvalue = 0.00347832
  Group = -> [Kr_element001]
  conduct = 2
  density = 1
  expand = 3
  formula = Kr
  name = G4_Kr
  specific = 4
FEATURE [App::DocumentObjectGroupPython] Rb_element001  label="Rb_element : 1"  # scripted group (container) (typed FeaturePython)
  n = 1
  ref = Rb_element
FEATURE [App::DocumentObjectGroupPython] G4_Rb  # scripted group (container) (typed FeaturePython)
  Dunit = g/cm3
  Dvalue = 1.532
  Group = -> [Rb_element001]
  conduct = 2
  density = 1
  expand = 3
  formula = Rb
  name = G4_Rb
  specific = 4
FEATURE [App::DocumentObjectGroupPython] Sr_element001  label="Sr_element : 1"  # scripted group (container) (typed FeaturePython)
  n = 1
  ref = Sr_element
FEATURE [App::DocumentObjectGroupPython] G4_Sr  # scripted group (container) (typed FeaturePython)
  Dunit = g/cm3
  Dvalue = 2.54
  Group = -> [Sr_element001]
  conduct = 2
  density = 1
  expand = 3
  formula = Sr
  name = G4_Sr
  specific = 4
FEATURE [App::DocumentObjectGroupPython] Y_element001  label="Y_element : 1"  # scripted group (container) (typed FeaturePython)
  n = 1
  ref = Y_element
FEATURE [App::DocumentObjectGroupPython] G4_Y  # scripted group (container) (typed FeaturePython)
  Dunit = g/cm3
  Dvalue = 4.469
  Group = -> [Y_element001]
  conduct = 2
  density = 1
  expand = 3
  formula = Y
  name = G4_Y
  specific = 4
FEATURE [App::DocumentObjectGroupPython] Zr_element001  label="Zr_element : 1"  # scripted group (container) (typed FeaturePython)
  n = 1
  ref = Zr_element
FEATURE [App::DocumentObjectGroupPython] G4_Zr  # scripted group (container) (typed FeaturePython)
  Dunit = g/cm3
  Dvalue = 6.506
  Group = -> [Zr_element001]
  conduct = 2
  density = 1
  expand = 3
  formula = Zr
  name = G4_Zr
  specific = 4
FEATURE [App::DocumentObjectGroupPython] Nb_element001  label="Nb_element : 1"  # scripted group (container) (typed FeaturePython)
  n = 1
  ref = Nb_element
FEATURE [App::DocumentObjectGroupPython] G4_Nb  # scripted group (container) (typed FeaturePython)
  Dunit = g/cm3
  Dvalue = 8.57
  Group = -> [Nb_element001]
  conduct = 2
  density = 1
  expand = 3
  formula = Nb
  name = G4_Nb
  specific = 4
FEATURE [App::DocumentObjectGroupPython] Mo_element001  label="Mo_element : 1"  # scripted group (container) (typed FeaturePython)
  n = 1
  ref = Mo_element
FEATURE [App::DocumentObjectGroupPython] G4_Mo  # scripted group (container) (typed FeaturePython)
  Dunit = g/cm3
  Dvalue = 10.22
  Group = -> [Mo_element001]
  conduct = 2
  density = 1
  expand = 3
  formula = Mo
  name = G4_Mo
  specific = 4
FEATURE [App::DocumentObjectGroupPython] Tc_element001  label="Tc_element : 1"  # scripted group (container) (typed FeaturePython)
  n = 1
  ref = Tc_element
FEATURE [App::DocumentObjectGroupPython] G4_Tc  # scripted group (container) (typed FeaturePython)
  Dunit = g/cm3
  Dvalue = 11.5
  Group = -> [Tc_element001]
  conduct = 2
  density = 1
  expand = 3
  formula = Tc
  name = G4_Tc
  specific = 4
FEATURE [App::DocumentObjectGroupPython] Ru_element001  label="Ru_element : 1"  # scripted group (container) (typed FeaturePython)
  n = 1
  ref = Ru_element
FEATURE [App::DocumentObjectGroupPython] G4_Ru  # scripted group (container) (typed FeaturePython)
  Dunit = g/cm3
  Dvalue = 12.41
  Group = -> [Ru_element001]
  conduct = 2
  density = 1
  expand = 3
  formula = Ru
  name = G4_Ru
  specific = 4
FEATURE [App::DocumentObjectGroupPython] Rh_element001  label="Rh_element : 1"  # scripted group (container) (typed FeaturePython)
  n = 1
  ref = Rh_element
FEATURE [App::DocumentObjectGroupPython] G4_Rh  # scripted group (container) (typed FeaturePython)
  Dunit = g/cm3
  Dvalue = 12.41
  Group = -> [Rh_element001]
  conduct = 2
  density = 1
  expand = 3
  formula = Rh
  name = G4_Rh
  specific = 4
FEATURE [App::DocumentObjectGroupPython] Pd_element001  label="Pd_element : 1"  # scripted group (container) (typed FeaturePython)
  n = 1
  ref = Pd_element
FEATURE [App::DocumentObjectGroupPython] G4_Pd  # scripted group (container) (typed FeaturePython)
  Dunit = g/cm3
  Dvalue = 12.02
  Group = -> [Pd_element001]
  conduct = 2
  density = 1
  expand = 3
  formula = Pd
  name = G4_Pd
  specific = 4
FEATURE [App::DocumentObjectGroupPython] Ag_element006  label="Ag_element : 004"  # scripted group (container) (typed FeaturePython)
  n = 1
  ref = Ag_element
FEATURE [App::DocumentObjectGroupPython] G4_Ag  # scripted group (container) (typed FeaturePython)
  Dunit = g/cm3
  Dvalue = 10.5
  Group = -> [Ag_element006]
  conduct = 2
  density = 1
  expand = 3
  formula = Ag
  name = G4_Ag
  specific = 4
FEATURE [App::DocumentObjectGroupPython] Cd_element003  label="Cd_element : 003"  # scripted group (container) (typed FeaturePython)
  n = 1
  ref = Cd_element
FEATURE [App::DocumentObjectGroupPython] G4_Cd  # scripted group (container) (typed FeaturePython)
  Dunit = g/cm3
  Dvalue = 8.65
  Group = -> [Cd_element003]
  conduct = 2
  density = 1
  expand = 3
  formula = Cd
  name = G4_Cd
  specific = 4
FEATURE [App::DocumentObjectGroupPython] In_element001  label="In_element : 1"  # scripted group (container) (typed FeaturePython)
  n = 1
  ref = In_element
FEATURE [App::DocumentObjectGroupPython] G4_In  # scripted group (container) (typed FeaturePython)
  Dunit = g/cm3
  Dvalue = 7.31
  Group = -> [In_element001]
  conduct = 2
  density = 1
  expand = 3
  formula = In
  name = G4_In
  specific = 4
FEATURE [App::DocumentObjectGroupPython] Sn_element001  label="Sn_element : 1"  # scripted group (container) (typed FeaturePython)
  n = 1
  ref = Sn_element
FEATURE [App::DocumentObjectGroupPython] G4_Sn  # scripted group (container) (typed FeaturePython)
  Dunit = g/cm3
  Dvalue = 7.31
  Group = -> [Sn_element001]
  conduct = 2
  density = 1
  expand = 3
  formula = Sn
  name = G4_Sn
  specific = 4
FEATURE [App::DocumentObjectGroupPython] Sb_element001  label="Sb_element : 1"  # scripted group (container) (typed FeaturePython)
  n = 1
  ref = Sb_element
FEATURE [App::DocumentObjectGroupPython] G4_Sb  # scripted group (container) (typed FeaturePython)
  Dunit = g/cm3
  Dvalue = 6.691
  Group = -> [Sb_element001]
  conduct = 2
  density = 1
  expand = 3
  formula = Sb
  name = G4_Sb
  specific = 4
FEATURE [App::DocumentObjectGroupPython] Te_element002  label="Te_element : 002"  # scripted group (container) (typed FeaturePython)
  n = 1
  ref = Te_element
FEATURE [App::DocumentObjectGroupPython] G4_Te  # scripted group (container) (typed FeaturePython)
  Dunit = g/cm3
  Dvalue = 6.24
  Group = -> [Te_element002]
  conduct = 2
  density = 1
  expand = 3
  formula = Te
  name = G4_Te
  specific = 4
FEATURE [App::DocumentObjectGroupPython] I_element010  label="I_element : 006"  # scripted group (container) (typed FeaturePython)
  n = 1
  ref = I_element
FEATURE [App::DocumentObjectGroupPython] G4_I  # scripted group (container) (typed FeaturePython)
  Dunit = g/cm3
  Dvalue = 4.93
  Group = -> [I_element010]
  conduct = 2
  density = 1
  expand = 3
  formula = I
  name = G4_I
  specific = 4
FEATURE [App::DocumentObjectGroupPython] Xe_element001  label="Xe_element : 1"  # scripted group (container) (typed FeaturePython)
  n = 1
  ref = Xe_element
FEATURE [App::DocumentObjectGroupPython] G4_Xe  # scripted group (container) (typed FeaturePython)
  Dunit = g/cm3
  Dvalue = 0.00548536
  Group = -> [Xe_element001]
  conduct = 2
  density = 1
  expand = 3
  formula = Xe
  name = G4_Xe
  specific = 4
FEATURE [App::DocumentObjectGroupPython] Cs_element003  label="Cs_element : 003"  # scripted group (container) (typed FeaturePython)
  n = 1
  ref = Cs_element
FEATURE [App::DocumentObjectGroupPython] G4_Cs  # scripted group (container) (typed FeaturePython)
  Dunit = g/cm3
  Dvalue = 1.873
  Group = -> [Cs_element003]
  conduct = 2
  density = 1
  expand = 3
  formula = Cs
  name = G4_Cs
  specific = 4
FEATURE [App::DocumentObjectGroupPython] Ba_element003  label="Ba_element : 003"  # scripted group (container) (typed FeaturePython)
  n = 1
  ref = Ba_element
FEATURE [App::DocumentObjectGroupPython] G4_Ba  # scripted group (container) (typed FeaturePython)
  Dunit = g/cm3
  Dvalue = 3.5
  Group = -> [Ba_element003]
  conduct = 2
  density = 1
  expand = 3
  formula = Ba
  name = G4_Ba
  specific = 4
FEATURE [App::DocumentObjectGroupPython] La_element003  label="La_element : 003"  # scripted group (container) (typed FeaturePython)
  n = 1
  ref = La_element
FEATURE [App::DocumentObjectGroupPython] G4_La  # scripted group (container) (typed FeaturePython)
  Dunit = g/cm3
  Dvalue = 6.154
  Group = -> [La_element003]
  conduct = 2
  density = 1
  expand = 3
  formula = La
  name = G4_La
  specific = 4
FEATURE [App::DocumentObjectGroupPython] Ce_element002  label="Ce_element : 1"  # scripted group (container) (typed FeaturePython)
  n = 1
  ref = Ce_element
FEATURE [App::DocumentObjectGroupPython] G4_Ce  # scripted group (container) (typed FeaturePython)
  Dunit = g/cm3
  Dvalue = 6.657
  Group = -> [Ce_element002]
  conduct = 2
  density = 1
  expand = 3
  formula = Ce
  name = G4_Ce
  specific = 4
FEATURE [App::DocumentObjectGroupPython] Pr_element001  label="Pr_element : 1"  # scripted group (container) (typed FeaturePython)
  n = 1
  ref = Pr_element
FEATURE [App::DocumentObjectGroupPython] G4_Pr  # scripted group (container) (typed FeaturePython)
  Dunit = g/cm3
  Dvalue = 6.71
  Group = -> [Pr_element001]
  conduct = 2
  density = 1
  expand = 3
  formula = Pr
  name = G4_Pr
  specific = 4
FEATURE [App::DocumentObjectGroupPython] Nd_element001  label="Nd_element : 1"  # scripted group (container) (typed FeaturePython)
  n = 1
  ref = Nd_element
FEATURE [App::DocumentObjectGroupPython] G4_Nd  # scripted group (container) (typed FeaturePython)
  Dunit = g/cm3
  Dvalue = 6.9
  Group = -> [Nd_element001]
  conduct = 2
  density = 1
  expand = 3
  formula = Nd
  name = G4_Nd
  specific = 4
FEATURE [App::DocumentObjectGroupPython] Pm_element001  label="Pm_element : 1"  # scripted group (container) (typed FeaturePython)
  n = 1
  ref = Pm_element
FEATURE [App::DocumentObjectGroupPython] G4_Pm  # scripted group (container) (typed FeaturePython)
  Dunit = g/cm3
  Dvalue = 7.22
  Group = -> [Pm_element001]
  conduct = 2
  density = 1
  expand = 3
  formula = Pm
  name = G4_Pm
  specific = 4
FEATURE [App::DocumentObjectGroupPython] Sm_element001  label="Sm_element : 1"  # scripted group (container) (typed FeaturePython)
  n = 1
  ref = Sm_element
FEATURE [App::DocumentObjectGroupPython] G4_Sm  # scripted group (container) (typed FeaturePython)
  Dunit = g/cm3
  Dvalue = 7.46
  Group = -> [Sm_element001]
  conduct = 2
  density = 1
  expand = 3
  formula = Sm
  name = G4_Sm
  specific = 4
FEATURE [App::DocumentObjectGroupPython] Eu_element001  label="Eu_element : 1"  # scripted group (container) (typed FeaturePython)
  n = 1
  ref = Eu_element
FEATURE [App::DocumentObjectGroupPython] G4_Eu  # scripted group (container) (typed FeaturePython)
  Dunit = g/cm3
  Dvalue = 5.243
  Group = -> [Eu_element001]
  conduct = 2
  density = 1
  expand = 3
  formula = Eu
  name = G4_Eu
  specific = 4
FEATURE [App::DocumentObjectGroupPython] Gd_element002  label="Gd_element : 1"  # scripted group (container) (typed FeaturePython)
  n = 1
  ref = Gd_element
FEATURE [App::DocumentObjectGroupPython] G4_Gd  # scripted group (container) (typed FeaturePython)
  Dunit = g/cm3
  Dvalue = 7.9004
  Group = -> [Gd_element002]
  conduct = 2
  density = 1
  expand = 3
  formula = Gd
  name = G4_Gd
  specific = 4
FEATURE [App::DocumentObjectGroupPython] Tb_element001  label="Tb_element : 1"  # scripted group (container) (typed FeaturePython)
  n = 1
  ref = Tb_element
FEATURE [App::DocumentObjectGroupPython] G4_Tb  # scripted group (container) (typed FeaturePython)
  Dunit = g/cm3
  Dvalue = 8.229
  Group = -> [Tb_element001]
  conduct = 2
  density = 1
  expand = 3
  formula = Tb
  name = G4_Tb
  specific = 4
FEATURE [App::DocumentObjectGroupPython] Dy_element001  label="Dy_element : 1"  # scripted group (container) (typed FeaturePython)
  n = 1
  ref = Dy_element
FEATURE [App::DocumentObjectGroupPython] G4_Dy  # scripted group (container) (typed FeaturePython)
  Dunit = g/cm3
  Dvalue = 8.55
  Group = -> [Dy_element001]
  conduct = 2
  density = 1
  expand = 3
  formula = Dy
  name = G4_Dy
  specific = 4
FEATURE [App::DocumentObjectGroupPython] Ho_element001  label="Ho_element : 1"  # scripted group (container) (typed FeaturePython)
  n = 1
  ref = Ho_element
FEATURE [App::DocumentObjectGroupPython] G4_Ho  # scripted group (container) (typed FeaturePython)
  Dunit = g/cm3
  Dvalue = 8.795
  Group = -> [Ho_element001]
  conduct = 2
  density = 1
  expand = 3
  formula = Ho
  name = G4_Ho
  specific = 4
FEATURE [App::DocumentObjectGroupPython] Er_element001  label="Er_element : 1"  # scripted group (container) (typed FeaturePython)
  n = 1
  ref = Er_element
FEATURE [App::DocumentObjectGroupPython] G4_Er  # scripted group (container) (typed FeaturePython)
  Dunit = g/cm3
  Dvalue = 9.066
  Group = -> [Er_element001]
  conduct = 2
  density = 1
  expand = 3
  formula = Er
  name = G4_Er
  specific = 4
FEATURE [App::DocumentObjectGroupPython] Tm_element001  label="Tm_element : 1"  # scripted group (container) (typed FeaturePython)
  n = 1
  ref = Tm_element
FEATURE [App::DocumentObjectGroupPython] G4_Tm  # scripted group (container) (typed FeaturePython)
  Dunit = g/cm3
  Dvalue = 9.321
  Group = -> [Tm_element001]
  conduct = 2
  density = 1
  expand = 3
  formula = Tm
  name = G4_Tm
  specific = 4
FEATURE [App::DocumentObjectGroupPython] Yb_element001  label="Yb_element : 1"  # scripted group (container) (typed FeaturePython)
  n = 1
  ref = Yb_element
FEATURE [App::DocumentObjectGroupPython] G4_Yb  # scripted group (container) (typed FeaturePython)
  Dunit = g/cm3
  Dvalue = 6.73
  Group = -> [Yb_element001]
  conduct = 2
  density = 1
  expand = 3
  formula = Yb
  name = G4_Yb
  specific = 4
FEATURE [App::DocumentObjectGroupPython] Lu_element001  label="Lu_element : 1"  # scripted group (container) (typed FeaturePython)
  n = 1
  ref = Lu_element
FEATURE [App::DocumentObjectGroupPython] G4_Lu  # scripted group (container) (typed FeaturePython)
  Dunit = g/cm3
  Dvalue = 9.84
  Group = -> [Lu_element001]
  conduct = 2
  density = 1
  expand = 3
  formula = Lu
  name = G4_Lu
  specific = 4
FEATURE [App::DocumentObjectGroupPython] Hf_element001  label="Hf_element : 1"  # scripted group (container) (typed FeaturePython)
  n = 1
  ref = Hf_element
FEATURE [App::DocumentObjectGroupPython] G4_Hf  # scripted group (container) (typed FeaturePython)
  Dunit = g/cm3
  Dvalue = 13.31
  Group = -> [Hf_element001]
  conduct = 2
  density = 1
  expand = 3
  formula = Hf
  name = G4_Hf
  specific = 4
FEATURE [App::DocumentObjectGroupPython] Ta_element001  label="Ta_element : 1"  # scripted group (container) (typed FeaturePython)
  n = 1
  ref = Ta_element
FEATURE [App::DocumentObjectGroupPython] G4_Ta  # scripted group (container) (typed FeaturePython)
  Dunit = g/cm3
  Dvalue = 16.654
  Group = -> [Ta_element001]
  conduct = 2
  density = 1
  expand = 3
  formula = Ta
  name = G4_Ta
  specific = 4
FEATURE [App::DocumentObjectGroupPython] W_element004  label="W_element : 004"  # scripted group (container) (typed FeaturePython)
  n = 1
  ref = W_element
FEATURE [App::DocumentObjectGroupPython] G4_W  # scripted group (container) (typed FeaturePython)
  Dunit = g/cm3
  Dvalue = 19.3
  Group = -> [W_element004]
  conduct = 2
  density = 1
  expand = 3
  formula = W
  name = G4_W
  specific = 4
FEATURE [App::DocumentObjectGroupPython] Re_element001  label="Re_element : 1"  # scripted group (container) (typed FeaturePython)
  n = 1
  ref = Re_element
FEATURE [App::DocumentObjectGroupPython] G4_Re  # scripted group (container) (typed FeaturePython)
  Dunit = g/cm3
  Dvalue = 21.02
  Group = -> [Re_element001]
  conduct = 2
  density = 1
  expand = 3
  formula = Re
  name = G4_Re
  specific = 4
FEATURE [App::DocumentObjectGroupPython] Os_element001  label="Os_element : 1"  # scripted group (container) (typed FeaturePython)
  n = 1
  ref = Os_element
FEATURE [App::DocumentObjectGroupPython] G4_Os  # scripted group (container) (typed FeaturePython)
  Dunit = g/cm3
  Dvalue = 22.57
  Group = -> [Os_element001]
  conduct = 2
  density = 1
  expand = 3
  formula = Os
  name = G4_Os
  specific = 4
FEATURE [App::DocumentObjectGroupPython] Ir_element001  label="Ir_element : 1"  # scripted group (container) (typed FeaturePython)
  n = 1
  ref = Ir_element
FEATURE [App::DocumentObjectGroupPython] G4_Ir  # scripted group (container) (typed FeaturePython)
  Dunit = g/cm3
  Dvalue = 22.42
  Group = -> [Ir_element001]
  conduct = 2
  density = 1
  expand = 3
  formula = Ir
  name = G4_Ir
  specific = 4
FEATURE [App::DocumentObjectGroupPython] Pt_element001  label="Pt_element : 1"  # scripted group (container) (typed FeaturePython)
  n = 1
  ref = Pt_element
FEATURE [App::DocumentObjectGroupPython] G4_Pt  # scripted group (container) (typed FeaturePython)
  Dunit = g/cm3
  Dvalue = 21.45
  Group = -> [Pt_element001]
  conduct = 2
  density = 1
  expand = 3
  formula = Pt
  name = G4_Pt
  specific = 4
FEATURE [App::DocumentObjectGroupPython] Au_element001  label="Au_element : 1"  # scripted group (container) (typed FeaturePython)
  n = 1
  ref = Au_element
FEATURE [App::DocumentObjectGroupPython] G4_Au  # scripted group (container) (typed FeaturePython)
  Dunit = g/cm3
  Dvalue = 19.32
  Group = -> [Au_element001]
  conduct = 2
  density = 1
  expand = 3
  formula = Au
  name = G4_Au
  specific = 4
FEATURE [App::DocumentObjectGroupPython] Hg_element002  label="Hg_element : 002"  # scripted group (container) (typed FeaturePython)
  n = 1
  ref = Hg_element
FEATURE [App::DocumentObjectGroupPython] G4_Hg  # scripted group (container) (typed FeaturePython)
  Dunit = g/cm3
  Dvalue = 13.546
  Group = -> [Hg_element002]
  conduct = 2
  density = 1
  expand = 3
  formula = Hg
  name = G4_Hg
  specific = 4
FEATURE [App::DocumentObjectGroupPython] Tl_element002  label="Tl_element : 002"  # scripted group (container) (typed FeaturePython)
  n = 1
  ref = Tl_element
FEATURE [App::DocumentObjectGroupPython] G4_Tl  # scripted group (container) (typed FeaturePython)
  Dunit = g/cm3
  Dvalue = 11.72
  Group = -> [Tl_element002]
  conduct = 2
  density = 1
  expand = 3
  formula = Tl
  name = G4_Tl
  specific = 4
FEATURE [App::DocumentObjectGroupPython] Pb_element003  label="Pb_element : 1"  # scripted group (container) (typed FeaturePython)
  n = 1
  ref = Pb_element
FEATURE [App::DocumentObjectGroupPython] G4_Pb  # scripted group (container) (typed FeaturePython)
  Dunit = g/cm3
  Dvalue = 11.35
  Group = -> [Pb_element003]
  conduct = 2
  density = 1
  expand = 3
  formula = Pb
  name = G4_Pb
  specific = 4
FEATURE [App::DocumentObjectGroupPython] Bi_element002  label="Bi_element : 1"  # scripted group (container) (typed FeaturePython)
  n = 1
  ref = Bi_element
FEATURE [App::DocumentObjectGroupPython] G4_Bi  # scripted group (container) (typed FeaturePython)
  Dunit = g/cm3
  Dvalue = 9.747
  Group = -> [Bi_element002]
  conduct = 2
  density = 1
  expand = 3
  formula = Bi
  name = G4_Bi
  specific = 4
FEATURE [App::DocumentObjectGroupPython] Po_element001  label="Po_element : 1"  # scripted group (container) (typed FeaturePython)
  n = 1
  ref = Po_element
FEATURE [App::DocumentObjectGroupPython] G4_Po  # scripted group (container) (typed FeaturePython)
  Dunit = g/cm3
  Dvalue = 9.32
  Group = -> [Po_element001]
  conduct = 2
  density = 1
  expand = 3
  formula = Po
  name = G4_Po
  specific = 4
FEATURE [App::DocumentObjectGroupPython] At_element001  label="At_element : 1"  # scripted group (container) (typed FeaturePython)
  n = 1
  ref = At_element
FEATURE [App::DocumentObjectGroupPython] G4_At  # scripted group (container) (typed FeaturePython)
  Dunit = g/cm3
  Dvalue = 9.32
  Group = -> [At_element001]
  conduct = 2
  density = 1
  expand = 3
  formula = At
  name = G4_At
  specific = 4
FEATURE [App::DocumentObjectGroupPython] Rn_element001  label="Rn_element : 1"  # scripted group (container) (typed FeaturePython)
  n = 1
  ref = Rn_element
FEATURE [App::DocumentObjectGroupPython] G4_Rn  # scripted group (container) (typed FeaturePython)
  Dunit = g/cm3
  Dvalue = 0.00900662
  Group = -> [Rn_element001]
  conduct = 2
  density = 1
  expand = 3
  formula = Rn
  name = G4_Rn
  specific = 4
FEATURE [App::DocumentObjectGroupPython] Fr_element001  label="Fr_element : 1"  # scripted group (container) (typed FeaturePython)
  n = 1
  ref = Fr_element
FEATURE [App::DocumentObjectGroupPython] G4_Fr  # scripted group (container) (typed FeaturePython)
  Dunit = g/cm3
  Dvalue = 1
  Group = -> [Fr_element001]
  conduct = 2
  density = 1
  expand = 3
  formula = Fr
  name = G4_Fr
  specific = 4
FEATURE [App::DocumentObjectGroupPython] Ra_element001  label="Ra_element : 1"  # scripted group (container) (typed FeaturePython)
  n = 1
  ref = Ra_element
FEATURE [App::DocumentObjectGroupPython] G4_Ra  # scripted group (container) (typed FeaturePython)
  Dunit = g/cm3
  Dvalue = 5
  Group = -> [Ra_element001]
  conduct = 2
  density = 1
  expand = 3
  formula = Ra
  name = G4_Ra
  specific = 4
FEATURE [App::DocumentObjectGroupPython] Ac_element001  label="Ac_element : 1"  # scripted group (container) (typed FeaturePython)
  n = 1
  ref = Ac_element
FEATURE [App::DocumentObjectGroupPython] G4_Ac  # scripted group (container) (typed FeaturePython)
  Dunit = g/cm3
  Dvalue = 10.07
  Group = -> [Ac_element001]
  conduct = 2
  density = 1
  expand = 3
  formula = Ac
  name = G4_Ac
  specific = 4
FEATURE [App::DocumentObjectGroupPython] Th_element001  label="Th_element : 1"  # scripted group (container) (typed FeaturePython)
  n = 1
  ref = Th_element
FEATURE [App::DocumentObjectGroupPython] G4_Th  # scripted group (container) (typed FeaturePython)
  Dunit = g/cm3
  Dvalue = 11.72
  Group = -> [Th_element001]
  conduct = 2
  density = 1
  expand = 3
  formula = Th
  name = G4_Th
  specific = 4
FEATURE [App::DocumentObjectGroupPython] Pa_element001  label="Pa_element : 1"  # scripted group (container) (typed FeaturePython)
  n = 1
  ref = Pa_element
FEATURE [App::DocumentObjectGroupPython] G4_Pa  # scripted group (container) (typed FeaturePython)
  Dunit = g/cm3
  Dvalue = 15.37
  Group = -> [Pa_element001]
  conduct = 2
  density = 1
  expand = 3
  formula = Pa
  name = G4_Pa
  specific = 4
FEATURE [App::DocumentObjectGroupPython] U_element004  label="U_element : 004"  # scripted group (container) (typed FeaturePython)
  n = 1
  ref = U_element
FEATURE [App::DocumentObjectGroupPython] G4_U  # scripted group (container) (typed FeaturePython)
  Dunit = g/cm3
  Dvalue = 18.95
  Group = -> [U_element004]
  conduct = 2
  density = 1
  expand = 3
  formula = U
  name = G4_U
  specific = 4
FEATURE [App::DocumentObjectGroupPython] Np_element001  label="Np_element : 1"  # scripted group (container) (typed FeaturePython)
  n = 1
  ref = Np_element
FEATURE [App::DocumentObjectGroupPython] G4_Np  # scripted group (container) (typed FeaturePython)
  Dunit = g/cm3
  Dvalue = 20.25
  Group = -> [Np_element001]
  conduct = 2
  density = 1
  expand = 3
  formula = Np
  name = G4_Np
  specific = 4
FEATURE [App::DocumentObjectGroupPython] Pu_element002  label="Pu_element : 002"  # scripted group (container) (typed FeaturePython)
  n = 1
  ref = Pu_element
FEATURE [App::DocumentObjectGroupPython] G4_Pu  # scripted group (container) (typed FeaturePython)
  Dunit = g/cm3
  Dvalue = 19.84
  Group = -> [Pu_element002]
  conduct = 2
  density = 1
  expand = 3
  formula = Pu
  name = G4_Pu
  specific = 4
FEATURE [App::DocumentObjectGroupPython] Am_element001  label="Am_element : 1"  # scripted group (container) (typed FeaturePython)
  n = 1
  ref = Am_element
FEATURE [App::DocumentObjectGroupPython] G4_Am  # scripted group (container) (typed FeaturePython)
  Dunit = g/cm3
  Dvalue = 13.67
  Group = -> [Am_element001]
  conduct = 2
  density = 1
  expand = 3
  formula = Am
  name = G4_Am
  specific = 4
FEATURE [App::DocumentObjectGroupPython] Cm_element001  label="Cm_element : 1"  # scripted group (container) (typed FeaturePython)
  n = 1
  ref = Cm_element
FEATURE [App::DocumentObjectGroupPython] G4_Cm  # scripted group (container) (typed FeaturePython)
  Dunit = g/cm3
  Dvalue = 13.51
  Group = -> [Cm_element001]
  conduct = 2
  density = 1
  expand = 3
  formula = Cm
  name = G4_Cm
  specific = 4
FEATURE [App::DocumentObjectGroupPython] Bk_element001  label="Bk_element : 1"  # scripted group (container) (typed FeaturePython)
  n = 1
  ref = Bk_element
FEATURE [App::DocumentObjectGroupPython] G4_Bk  # scripted group (container) (typed FeaturePython)
  Dunit = g/cm3
  Dvalue = 14
  Group = -> [Bk_element001]
  conduct = 2
  density = 1
  expand = 3
  formula = Bk
  name = G4_Bk
  specific = 4
FEATURE [App::DocumentObjectGroupPython] Cf_element001  label="Cf_element : 1"  # scripted group (container) (typed FeaturePython)
  n = 1
  ref = Cf_element
FEATURE [App::DocumentObjectGroupPython] G4_Cf  # scripted group (container) (typed FeaturePython)
  Dunit = g/cm3
  Dvalue = 10
  Group = -> [Cf_element001]
  conduct = 2
  density = 1
  expand = 3
  formula = Cf
  name = G4_Cf
  specific = 4
FEATURE [App::DocumentObjectGroupPython] Element  # scripted group (container) (typed FeaturePython)
  Group = -> [G4_H,G4_He,G4_Li,G4_Be,G4_B,G4_C,G4_N,G4_O,G4_F,G4_Ne,G4_Na,G4_Mg,G4_Al,G4_Si,G4_P,G4_S,G4_Cl,G4_Ar,G4_K,G4_Ca,G4_Sc,G4_Ti,G4_V,G4_Cr,G4_Mn,G4_Fe,G4_Co,G4_Ni,G4_Cu,G4_Zn,G4_Ga,G4_Ge,G4_As,G4_Se,G4_Br,G4_Kr,G4_Rb,G4_Sr,G4_Y,G4_Zr,G4_Nb,G4_Mo,G4_Tc,G4_Ru,G4_Rh,G4_Pd,G4_Ag,G4_Cd,G4_In,G4_Sn,G4_Sb,G4_Te,G4_I,G4_Xe,G4_Cs,G4_Ba,G4_La,G4_Ce,G4_Pr,G4_Nd,G4_Pm,G4_Sm,G4_Eu,G4_Gd,G4_Tb,G4_Dy,G4_Ho,G4_Er,+30 more]
FEATURE [App::DocumentObjectGroupPython] H_element114  label="H_element : 063"  # scripted group (container) (typed FeaturePython)
  n = 2
  ref = H_element
FEATURE [App::DocumentObjectGroupPython] G4_lH2  # scripted group (container) (typed FeaturePython)
  Dunit = g/cm3
  Dvalue = 0.0708
  Group = -> [H_element114]
  conduct = 2
  density = 1
  expand = 3
  formula = G4_lH2
  name = G4_lH2
  specific = 4
FEATURE [App::DocumentObjectGroupPython] N_element049  label="N_element : 022"  # scripted group (container) (typed FeaturePython)
  n = 2
  ref = N_element
FEATURE [App::DocumentObjectGroupPython] G4_lN2  # scripted group (container) (typed FeaturePython)
  Dunit = g/cm3
  Dvalue = 0.807
  Group = -> [N_element049]
  conduct = 2
  density = 1
  expand = 3
  formula = G4_lN2
  name = G4_lN2
  specific = 4
FEATURE [App::DocumentObjectGroupPython] O_element106  label="O_element : 060"  # scripted group (container) (typed FeaturePython)
  n = 2
  ref = O_element
FEATURE [App::DocumentObjectGroupPython] G4_lO2  # scripted group (container) (typed FeaturePython)
  Dunit = g/cm3
  Dvalue = 1.141
  Group = -> [O_element106]
  conduct = 2
  density = 1
  expand = 3
  formula = G4_lO2
  name = G4_lO2
  specific = 4
FEATURE [App::DocumentObjectGroupPython] Ar_element003  label="Ar_element : 002"  # scripted group (container) (typed FeaturePython)
  n = 1
  ref = Ar_element
FEATURE [App::DocumentObjectGroupPython] G4_lAr  # scripted group (container) (typed FeaturePython)
  Dunit = g/cm3
  Dvalue = 1.396
  Group = -> [Ar_element003]
  conduct = 2
  density = 1
  expand = 3
  formula = G4_lAr
  name = G4_lAr
  specific = 4
FEATURE [App::DocumentObjectGroupPython] Br_element008  label="Br_element : 005"  # scripted group (container) (typed FeaturePython)
  n = 1
  ref = Br_element
FEATURE [App::DocumentObjectGroupPython] G4_lBr  # scripted group (container) (typed FeaturePython)
  Dunit = g/cm3
  Dvalue = 3.1028
  Group = -> [Br_element008]
  conduct = 2
  density = 1
  expand = 3
  formula = G4_lBr
  name = G4_lBr
  specific = 4
FEATURE [App::DocumentObjectGroupPython] Kr_element002  label="Kr_element : 002"  # scripted group (container) (typed FeaturePython)
  n = 1
  ref = Kr_element
FEATURE [App::DocumentObjectGroupPython] G4_lKr  # scripted group (container) (typed FeaturePython)
  Dunit = g/cm3
  Dvalue = 2.418
  Group = -> [Kr_element002]
  conduct = 2
  density = 1
  expand = 3
  formula = G4_lKr
  name = G4_lKr
  specific = 4
FEATURE [App::DocumentObjectGroupPython] Xe_element002  label="Xe_element : 002"  # scripted group (container) (typed FeaturePython)
  n = 1
  ref = Xe_element
FEATURE [App::DocumentObjectGroupPython] G4_lXe  # scripted group (container) (typed FeaturePython)
  Dunit = g/cm3
  Dvalue = 2.953
  Group = -> [Xe_element002]
  conduct = 2
  density = 1
  expand = 3
  formula = G4_lXe
  name = G4_lXe
  specific = 4
FEATURE [App::DocumentObjectGroupPython] O_element107  label="O_element : 061"  # scripted group (container) (typed FeaturePython)
  n = 4
  ref = O_element
FEATURE [App::DocumentObjectGroupPython] Pb_element004  label="Pb_element : 002"  # scripted group (container) (typed FeaturePython)
  n = 1
  ref = Pb_element
FEATURE [App::DocumentObjectGroupPython] W_element005  label="W_element : 005"  # scripted group (container) (typed FeaturePython)
  n = 1
  ref = W_element
FEATURE [App::DocumentObjectGroupPython] G4_PbWO4  # scripted group (container) (typed FeaturePython)
  Dunit = g/cm3
  Dvalue = 8.28
  Group = -> [O_element107,Pb_element004,W_element005]
  conduct = 2
  density = 1
  expand = 3
  formula = G4_PbWO4
  name = G4_PbWO4
  specific = 4
FEATURE [App::DocumentObjectGroupPython] H_element115  label="H_element : 064"  # scripted group (container) (typed FeaturePython)
  n = 1
  ref = H_element
FEATURE [App::DocumentObjectGroupPython] G4_Galactic  # scripted group (container) (typed FeaturePython)
  Dunit = g/cm3
  Dvalue = 0
  Group = -> [H_element115]
  conduct = 2
  density = 1
  expand = 3
  formula = G4_Galactic
  name = G4_Galactic
  specific = 4
FEATURE [App::DocumentObjectGroupPython] C_element125  label="C_element : 071"  # scripted group (container) (typed FeaturePython)
  n = 1
  ref = C_element
FEATURE [App::DocumentObjectGroupPython] G4_GRAPHITE_POROUS  # scripted group (container) (typed FeaturePython)
  Dunit = g/cm3
  Dvalue = 1.7
  Group = -> [C_element125]
  conduct = 2
  density = 1
  expand = 3
  formula = G4_GRAPHITE_POROUS
  name = G4_GRAPHITE_POROUS
  specific = 4
FEATURE [App::DocumentObjectGroupPython] H_element116  label="H_element : 0.150"  # scripted group (container) (typed FeaturePython)
  n = 0.080538
FEATURE [App::DocumentObjectGroupPython] C_element126  label="C_element : 0.600"  # scripted group (container) (typed FeaturePython)
  n = 0.599848
FEATURE [App::DocumentObjectGroupPython] O_element108  label="O_element : 0.320"  # scripted group (container) (typed FeaturePython)
  n = 0.319614
FEATURE [App::DocumentObjectGroupPython] G4_LUCITE  # scripted group (container) (typed FeaturePython)
  Dunit = g/cm3
  Dvalue = 1.19
  Group = -> [H_element116,C_element126,O_element108]
  conduct = 2
  density = 1
  expand = 3
  formula = G4_LUCITE
  name = G4_LUCITE
  specific = 4
FEATURE [App::DocumentObjectGroupPython] Cu_element002  label="Cu_element : 62"  # scripted group (container) (typed FeaturePython)
  n = 62
  ref = Cu_element
FEATURE [App::DocumentObjectGroupPython] Zn_element002  label="Zn_element : 35"  # scripted group (container) (typed FeaturePython)
  n = 35
  ref = Zn_element
FEATURE [App::DocumentObjectGroupPython] Pb_element005  label="Pb_element : 3"  # scripted group (container) (typed FeaturePython)
  n = 3
  ref = Pb_element
FEATURE [App::DocumentObjectGroupPython] G4_BRASS  # scripted group (container) (typed FeaturePython)
  Dunit = g/cm3
  Dvalue = 8.52
  Group = -> [Cu_element002,Zn_element002,Pb_element005]
  conduct = 2
  density = 1
  expand = 3
  formula = G4_BRASS
  name = G4_BRASS
  specific = 4
FEATURE [App::DocumentObjectGroupPython] Cu_element003  label="Cu_element : 89"  # scripted group (container) (typed FeaturePython)
  n = 89
  ref = Cu_element
FEATURE [App::DocumentObjectGroupPython] Zn_element003  label="Zn_element : 9"  # scripted group (container) (typed FeaturePython)
  n = 9
  ref = Zn_element
FEATURE [App::DocumentObjectGroupPython] Pb_element006  label="Pb_element : 2"  # scripted group (container) (typed FeaturePython)
  n = 2
  ref = Pb_element
FEATURE [App::DocumentObjectGroupPython] G4_BRONZE  # scripted group (container) (typed FeaturePython)
  Dunit = g/cm3
  Dvalue = 8.82
  Group = -> [Cu_element003,Zn_element003,Pb_element006]
  conduct = 2
  density = 1
  expand = 3
  formula = G4_BRONZE
  name = G4_BRONZE
  specific = 4
FEATURE [App::DocumentObjectGroupPython] Fe_element008  label="Fe_element : 74"  # scripted group (container) (typed FeaturePython)
  n = 74
  ref = Fe_element
FEATURE [App::DocumentObjectGroupPython] Cr_element002  label="Cr_element : 18"  # scripted group (container) (typed FeaturePython)
  n = 18
  ref = Cr_element
FEATURE [App::DocumentObjectGroupPython] Ni_element002  label="Ni_element : 8"  # scripted group (container) (typed FeaturePython)
  n = 8
  ref = Ni_element
FEATURE [App::DocumentObjectGroupPython] G4_STAINLESS_STEEL  label="G4_STAINLESS-STEEL"  # scripted group (container) (typed FeaturePython)
  Dunit = g/cm3
  Dvalue = 8
  Group = -> [Fe_element008,Cr_element002,Ni_element002]
  conduct = 2
  density = 1
  expand = 3
  formula = G4_STAINLESS-STEEL
  name = G4_STAINLESS-STEEL
  specific = 4
FEATURE [App::DocumentObjectGroupPython] H_element117  label="H_element : 065"  # scripted group (container) (typed FeaturePython)
  n = 18
  ref = H_element
FEATURE [App::DocumentObjectGroupPython] C_element127  label="C_element : 072"  # scripted group (container) (typed FeaturePython)
  n = 12
  ref = C_element
FEATURE [App::DocumentObjectGroupPython] O_element109  label="O_element : 062"  # scripted group (container) (typed FeaturePython)
  n = 7
  ref = O_element
FEATURE [App::DocumentObjectGroupPython] G4_CR39  # scripted group (container) (typed FeaturePython)
  Dunit = g/cm3
  Dvalue = 1.32
  Group = -> [H_element117,C_element127,O_element109]
  conduct = 2
  density = 1
  expand = 3
  formula = G4_CR39
  name = G4_CR39
  specific = 4
FEATURE [App::DocumentObjectGroupPython] H_element118  label="H_element : 38"  # scripted group (container) (typed FeaturePython)
  n = 38
  ref = H_element
FEATURE [App::DocumentObjectGroupPython] C_element128  label="C_element : 073"  # scripted group (container) (typed FeaturePython)
  n = 18
  ref = C_element
FEATURE [App::DocumentObjectGroupPython] O_element110  label="O_element : 063"  # scripted group (container) (typed FeaturePython)
  n = 1
  ref = O_element
FEATURE [App::DocumentObjectGroupPython] G4_OCTADECANOL  # scripted group (container) (typed FeaturePython)
  Dunit = g/cm3
  Dvalue = 0.812
  Group = -> [H_element118,C_element128,O_element110]
  conduct = 2
  density = 1
  expand = 3
  formula = G4_OCTADECANOL
  name = G4_OCTADECANOL
  specific = 4
FEATURE [App::DocumentObjectGroupPython] HEP  # scripted group (container) (typed FeaturePython)
  Group = -> [G4_lH2,G4_lN2,G4_lO2,G4_lAr,G4_lBr,G4_lKr,G4_lXe,G4_PbWO4,G4_Galactic,G4_GRAPHITE_POROUS,G4_LUCITE,G4_BRASS,G4_BRONZE,G4_STAINLESS_STEEL,G4_CR39,G4_OCTADECANOL]
FEATURE [App::DocumentObjectGroupPython] C_element129  label="C_element : 074"  # scripted group (container) (typed FeaturePython)
  n = 14
  ref = C_element
FEATURE [App::DocumentObjectGroupPython] H_element119  label="H_element : 066"  # scripted group (container) (typed FeaturePython)
  n = 10
  ref = H_element
FEATURE [App::DocumentObjectGroupPython] O_element111  label="O_element : 064"  # scripted group (container) (typed FeaturePython)
  n = 2
  ref = O_element
FEATURE [App::DocumentObjectGroupPython] N_element050  label="N_element : 023"  # scripted group (container) (typed FeaturePython)
  n = 2
  ref = N_element
FEATURE [App::DocumentObjectGroupPython] G4_KEVLAR  # scripted group (container) (typed FeaturePython)
  Dunit = g/cm3
  Dvalue = 1.44
  Group = -> [C_element129,H_element119,O_element111,N_element050]
  conduct = 2
  density = 1
  expand = 3
  formula = G4_KEVLAR
  name = G4_KEVLAR
  specific = 4
FEATURE [App::DocumentObjectGroupPython] C_element130  label="C_element : 075"  # scripted group (container) (typed FeaturePython)
  n = 10
  ref = C_element
FEATURE [App::DocumentObjectGroupPython] H_element120  label="H_element : 067"  # scripted group (container) (typed FeaturePython)
  n = 8
  ref = H_element
FEATURE [App::DocumentObjectGroupPython] O_element112  label="O_element : 065"  # scripted group (container) (typed FeaturePython)
  n = 4
  ref = O_element
FEATURE [App::DocumentObjectGroupPython] G4_DACRON  # scripted group (container) (typed FeaturePython)
  Dunit = g/cm3
  Dvalue = 1.4
  Group = -> [C_element130,H_element120,O_element112]
  conduct = 2
  density = 1
  expand = 3
  formula = G4_DACRON
  name = G4_DACRON
  specific = 4
FEATURE [App::DocumentObjectGroupPython] C_element131  label="C_element : 076"  # scripted group (container) (typed FeaturePython)
  n = 4
  ref = C_element
FEATURE [App::DocumentObjectGroupPython] H_element121  label="H_element : 068"  # scripted group (container) (typed FeaturePython)
  n = 5
  ref = H_element
FEATURE [App::DocumentObjectGroupPython] Cl_element030  label="Cl_element : 016"  # scripted group (container) (typed FeaturePython)
  n = 1
  ref = Cl_element
FEATURE [App::DocumentObjectGroupPython] G4_NEOPRENE  # scripted group (container) (typed FeaturePython)
  Dunit = g/cm3
  Dvalue = 1.23
  Group = -> [C_element131,H_element121,Cl_element030]
  conduct = 2
  density = 1
  expand = 3
  formula = G4_NEOPRENE
  name = G4_NEOPRENE
  specific = 4
FEATURE [App::DocumentObjectGroupPython] Space  # scripted group (container) (typed FeaturePython)
  Group = -> [G4_KEVLAR,G4_DACRON,G4_NEOPRENE]
FEATURE [App::DocumentObjectGroupPython] H_element122  label="H_element : 069"  # scripted group (container) (typed FeaturePython)
  n = 5
  ref = H_element
FEATURE [App::DocumentObjectGroupPython] C_element132  label="C_element : 077"  # scripted group (container) (typed FeaturePython)
  n = 4
  ref = C_element
FEATURE [App::DocumentObjectGroupPython] N_element051  label="N_element : 3"  # scripted group (container) (typed FeaturePython)
  n = 3
  ref = N_element
FEATURE [App::DocumentObjectGroupPython] O_element113  label="O_element : 066"  # scripted group (container) (typed FeaturePython)
  n = 1
  ref = O_element
FEATURE [App::DocumentObjectGroupPython] G4_CYTOSINE  # scripted group (container) (typed FeaturePython)
  Dunit = g/cm3
  Dvalue = 1.55
  Group = -> [H_element122,C_element132,N_element051,O_element113]
  conduct = 2
  density = 1
  expand = 3
  formula = G4_CYTOSINE
  name = G4_CYTOSINE
  specific = 4
FEATURE [App::DocumentObjectGroupPython] H_element123  label="H_element : 070"  # scripted group (container) (typed FeaturePython)
  n = 6
  ref = H_element
FEATURE [App::DocumentObjectGroupPython] C_element133  label="C_element : 078"  # scripted group (container) (typed FeaturePython)
  n = 5
  ref = C_element
FEATURE [App::DocumentObjectGroupPython] N_element052  label="N_element : 024"  # scripted group (container) (typed FeaturePython)
  n = 2
  ref = N_element
FEATURE [App::DocumentObjectGroupPython] O_element114  label="O_element : 067"  # scripted group (container) (typed FeaturePython)
  n = 2
  ref = O_element
FEATURE [App::DocumentObjectGroupPython] G4_THYMINE  # scripted group (container) (typed FeaturePython)
  Dunit = g/cm3
  Dvalue = 1.23
  Group = -> [H_element123,C_element133,N_element052,O_element114]
  conduct = 2
  density = 1
  expand = 3
  formula = G4_THYMINE
  name = G4_THYMINE
  specific = 4
FEATURE [App::DocumentObjectGroupPython] H_element124  label="H_element : 071"  # scripted group (container) (typed FeaturePython)
  n = 4
  ref = H_element
FEATURE [App::DocumentObjectGroupPython] C_element134  label="C_element : 079"  # scripted group (container) (typed FeaturePython)
  n = 4
  ref = C_element
FEATURE [App::DocumentObjectGroupPython] N_element053  label="N_element : 025"  # scripted group (container) (typed FeaturePython)
  n = 2
  ref = N_element
FEATURE [App::DocumentObjectGroupPython] O_element115  label="O_element : 068"  # scripted group (container) (typed FeaturePython)
  n = 2
  ref = O_element
FEATURE [App::DocumentObjectGroupPython] G4_URACIL  # scripted group (container) (typed FeaturePython)
  Dunit = g/cm3
  Dvalue = 1.32
  Group = -> [H_element124,C_element134,N_element053,O_element115]
  conduct = 2
  density = 1
  expand = 3
  formula = G4_URACIL
  name = G4_URACIL
  specific = 4
FEATURE [App::DocumentObjectGroupPython] H_element125  label="H_element : 072"  # scripted group (container) (typed FeaturePython)
  n = 4
  ref = H_element
FEATURE [App::DocumentObjectGroupPython] C_element135  label="C_element : 080"  # scripted group (container) (typed FeaturePython)
  n = 5
  ref = C_element
FEATURE [App::DocumentObjectGroupPython] N_element054  label="N_element : 026"  # scripted group (container) (typed FeaturePython)
  n = 5
  ref = N_element
FEATURE [App::DocumentObjectGroupPython] G4_DNA_ADENINE  # scripted group (container) (typed FeaturePython)
  Dunit = g/cm3
  Dvalue = 1
  Group = -> [H_element125,C_element135,N_element054]
  conduct = 2
  density = 1
  expand = 3
  formula = G4_DNA_ADENINE
  name = G4_DNA_ADENINE
  specific = 4
FEATURE [App::DocumentObjectGroupPython] H_element126  label="H_element : 073"  # scripted group (container) (typed FeaturePython)
  n = 4
  ref = H_element
FEATURE [App::DocumentObjectGroupPython] C_element136  label="C_element : 081"  # scripted group (container) (typed FeaturePython)
  n = 5
  ref = C_element
FEATURE [App::DocumentObjectGroupPython] N_element055  label="N_element : 027"  # scripted group (container) (typed FeaturePython)
  n = 5
  ref = N_element
FEATURE [App::DocumentObjectGroupPython] O_element116  label="O_element : 069"  # scripted group (container) (typed FeaturePython)
  n = 1
  ref = O_element
FEATURE [App::DocumentObjectGroupPython] G4_DNA_GUANINE  # scripted group (container) (typed FeaturePython)
  Dunit = g/cm3
  Dvalue = 1
  Group = -> [H_element126,C_element136,N_element055,O_element116]
  conduct = 2
  density = 1
  expand = 3
  formula = G4_DNA_GUANINE
  name = G4_DNA_GUANINE
  specific = 4
FEATURE [App::DocumentObjectGroupPython] H_element127  label="H_element : 074"  # scripted group (container) (typed FeaturePython)
  n = 4
  ref = H_element
FEATURE [App::DocumentObjectGroupPython] C_element137  label="C_element : 082"  # scripted group (container) (typed FeaturePython)
  n = 4
  ref = C_element
FEATURE [App::DocumentObjectGroupPython] N_element056  label="N_element : 028"  # scripted group (container) (typed FeaturePython)
  n = 3
  ref = N_element
FEATURE [App::DocumentObjectGroupPython] O_element117  label="O_element : 070"  # scripted group (container) (typed FeaturePython)
  n = 1
  ref = O_element
FEATURE [App::DocumentObjectGroupPython] G4_DNA_CYTOSINE  # scripted group (container) (typed FeaturePython)
  Dunit = g/cm3
  Dvalue = 1
  Group = -> [H_element127,C_element137,N_element056,O_element117]
  conduct = 2
  density = 1
  expand = 3
  formula = G4_DNA_CYTOSINE
  name = G4_DNA_CYTOSINE
  specific = 4
FEATURE [App::DocumentObjectGroupPython] H_element128  label="H_element : 075"  # scripted group (container) (typed FeaturePython)
  n = 5
  ref = H_element
FEATURE [App::DocumentObjectGroupPython] C_element138  label="C_element : 083"  # scripted group (container) (typed FeaturePython)
  n = 5
  ref = C_element
FEATURE [App::DocumentObjectGroupPython] N_element057  label="N_element : 029"  # scripted group (container) (typed FeaturePython)
  n = 2
  ref = N_element
FEATURE [App::DocumentObjectGroupPython] O_element118  label="O_element : 071"  # scripted group (container) (typed FeaturePython)
  n = 2
  ref = O_element
FEATURE [App::DocumentObjectGroupPython] G4_DNA_THYMINE  # scripted group (container) (typed FeaturePython)
  Dunit = g/cm3
  Dvalue = 1
  Group = -> [H_element128,C_element138,N_element057,O_element118]
  conduct = 2
  density = 1
  expand = 3
  formula = G4_DNA_THYMINE
  name = G4_DNA_THYMINE
  specific = 4
FEATURE [App::DocumentObjectGroupPython] H_element129  label="H_element : 076"  # scripted group (container) (typed FeaturePython)
  n = 3
  ref = H_element
FEATURE [App::DocumentObjectGroupPython] C_element139  label="C_element : 084"  # scripted group (container) (typed FeaturePython)
  n = 4
  ref = C_element
FEATURE [App::DocumentObjectGroupPython] N_element058  label="N_element : 030"  # scripted group (container) (typed FeaturePython)
  n = 2
  ref = N_element
FEATURE [App::DocumentObjectGroupPython] O_element119  label="O_element : 072"  # scripted group (container) (typed FeaturePython)
  n = 2
  ref = O_element
FEATURE [App::DocumentObjectGroupPython] G4_DNA_URACIL  # scripted group (container) (typed FeaturePython)
  Dunit = g/cm3
  Dvalue = 1
  Group = -> [H_element129,C_element139,N_element058,O_element119]
  conduct = 2
  density = 1
  expand = 3
  formula = G4_DNA_URACIL
  name = G4_DNA_URACIL
  specific = 4
FEATURE [App::DocumentObjectGroupPython] H_element130  label="H_element : 077"  # scripted group (container) (typed FeaturePython)
  n = 10
  ref = H_element
FEATURE [App::DocumentObjectGroupPython] C_element140  label="C_element : 085"  # scripted group (container) (typed FeaturePython)
  n = 10
  ref = C_element
FEATURE [App::DocumentObjectGroupPython] N_element059  label="N_element : 031"  # scripted group (container) (typed FeaturePython)
  n = 5
  ref = N_element
FEATURE [App::DocumentObjectGroupPython] O_element120  label="O_element : 073"  # scripted group (container) (typed FeaturePython)
  n = 4
  ref = O_element
FEATURE [App::DocumentObjectGroupPython] G4_DNA_ADENOSINE  # scripted group (container) (typed FeaturePython)
  Dunit = g/cm3
  Dvalue = 1
  Group = -> [H_element130,C_element140,N_element059,O_element120]
  conduct = 2
  density = 1
  expand = 3
  formula = G4_DNA_ADENOSINE
  name = G4_DNA_ADENOSINE
  specific = 4
FEATURE [App::DocumentObjectGroupPython] H_element131  label="H_element : 078"  # scripted group (container) (typed FeaturePython)
  n = 10
  ref = H_element
FEATURE [App::DocumentObjectGroupPython] C_element141  label="C_element : 086"  # scripted group (container) (typed FeaturePython)
  n = 10
  ref = C_element
FEATURE [App::DocumentObjectGroupPython] N_element060  label="N_element : 032"  # scripted group (container) (typed FeaturePython)
  n = 5
  ref = N_element
FEATURE [App::DocumentObjectGroupPython] O_element121  label="O_element : 074"  # scripted group (container) (typed FeaturePython)
  n = 5
  ref = O_element
FEATURE [App::DocumentObjectGroupPython] G4_DNA_GUANOSINE  # scripted group (container) (typed FeaturePython)
  Dunit = g/cm3
  Dvalue = 1
  Group = -> [H_element131,C_element141,N_element060,O_element121]
  conduct = 2
  density = 1
  expand = 3
  formula = G4_DNA_GUANOSINE
  name = G4_DNA_GUANOSINE
  specific = 4
FEATURE [App::DocumentObjectGroupPython] H_element132  label="H_element : 079"  # scripted group (container) (typed FeaturePython)
  n = 10
  ref = H_element
FEATURE [App::DocumentObjectGroupPython] C_element142  label="C_element : 087"  # scripted group (container) (typed FeaturePython)
  n = 9
  ref = C_element
FEATURE [App::DocumentObjectGroupPython] N_element061  label="N_element : 033"  # scripted group (container) (typed FeaturePython)
  n = 3
  ref = N_element
FEATURE [App::DocumentObjectGroupPython] O_element122  label="O_element : 075"  # scripted group (container) (typed FeaturePython)
  n = 5
  ref = O_element
FEATURE [App::DocumentObjectGroupPython] G4_DNA_CYTIDINE  # scripted group (container) (typed FeaturePython)
  Dunit = g/cm3
  Dvalue = 1
  Group = -> [H_element132,C_element142,N_element061,O_element122]
  conduct = 2
  density = 1
  expand = 3
  formula = G4_DNA_CYTIDINE
  name = G4_DNA_CYTIDINE
  specific = 4
FEATURE [App::DocumentObjectGroupPython] H_element133  label="H_element : 080"  # scripted group (container) (typed FeaturePython)
  n = 9
  ref = H_element
FEATURE [App::DocumentObjectGroupPython] C_element143  label="C_element : 088"  # scripted group (container) (typed FeaturePython)
  n = 9
  ref = C_element
FEATURE [App::DocumentObjectGroupPython] N_element062  label="N_element : 034"  # scripted group (container) (typed FeaturePython)
  n = 2
  ref = N_element
FEATURE [App::DocumentObjectGroupPython] O_element123  label="O_element : 076"  # scripted group (container) (typed FeaturePython)
  n = 6
  ref = O_element
FEATURE [App::DocumentObjectGroupPython] G4_DNA_URIDINE  # scripted group (container) (typed FeaturePython)
  Dunit = g/cm3
  Dvalue = 1
  Group = -> [H_element133,C_element143,N_element062,O_element123]
  conduct = 2
  density = 1
  expand = 3
  formula = G4_DNA_URIDINE
  name = G4_DNA_URIDINE
  specific = 4
FEATURE [App::DocumentObjectGroupPython] H_element134  label="H_element : 081"  # scripted group (container) (typed FeaturePython)
  n = 11
  ref = H_element
FEATURE [App::DocumentObjectGroupPython] C_element144  label="C_element : 089"  # scripted group (container) (typed FeaturePython)
  n = 10
  ref = C_element
FEATURE [App::DocumentObjectGroupPython] N_element063  label="N_element : 035"  # scripted group (container) (typed FeaturePython)
  n = 2
  ref = N_element
FEATURE [App::DocumentObjectGroupPython] O_element124  label="O_element : 077"  # scripted group (container) (typed FeaturePython)
  n = 6
  ref = O_element
FEATURE [App::DocumentObjectGroupPython] G4_DNA_METHYLURIDINE  # scripted group (container) (typed FeaturePython)
  Dunit = g/cm3
  Dvalue = 1
  Group = -> [H_element134,C_element144,N_element063,O_element124]
  conduct = 2
  density = 1
  expand = 3
  formula = G4_DNA_METHYLURIDINE
  name = G4_DNA_METHYLURIDINE
  specific = 4
FEATURE [App::DocumentObjectGroupPython] P_element014  label="P_element : 003"  # scripted group (container) (typed FeaturePython)
  n = 1
  ref = P_element
FEATURE [App::DocumentObjectGroupPython] O_element125  label="O_element : 078"  # scripted group (container) (typed FeaturePython)
  n = 3
  ref = O_element
FEATURE [App::DocumentObjectGroupPython] G4_DNA_MONOPHOSPHATE  # scripted group (container) (typed FeaturePython)
  Dunit = g/cm3
  Dvalue = 1
  Group = -> [P_element014,O_element125]
  conduct = 2
  density = 1
  expand = 3
  formula = G4_DNA_MONOPHOSPHATE
  name = G4_DNA_MONOPHOSPHATE
  specific = 4
FEATURE [App::DocumentObjectGroupPython] H_element135  label="H_element : 082"  # scripted group (container) (typed FeaturePython)
  n = 10
  ref = H_element
FEATURE [App::DocumentObjectGroupPython] C_element145  label="C_element : 090"  # scripted group (container) (typed FeaturePython)
  n = 10
  ref = C_element
FEATURE [App::DocumentObjectGroupPython] N_element064  label="N_element : 036"  # scripted group (container) (typed FeaturePython)
  n = 5
  ref = N_element
FEATURE [App::DocumentObjectGroupPython] O_element126  label="O_element : 079"  # scripted group (container) (typed FeaturePython)
  n = 7
  ref = O_element
FEATURE [App::DocumentObjectGroupPython] P_element015  label="P_element : 004"  # scripted group (container) (typed FeaturePython)
  n = 1
  ref = P_element
FEATURE [App::DocumentObjectGroupPython] G4_DNA_A  # scripted group (container) (typed FeaturePython)
  Dunit = g/cm3
  Dvalue = 1
  Group = -> [H_element135,C_element145,N_element064,O_element126,P_element015]
  conduct = 2
  density = 1
  expand = 3
  formula = G4_DNA_A
  name = G4_DNA_A
  specific = 4
FEATURE [App::DocumentObjectGroupPython] H_element136  label="H_element : 083"  # scripted group (container) (typed FeaturePython)
  n = 10
  ref = H_element
FEATURE [App::DocumentObjectGroupPython] C_element146  label="C_element : 091"  # scripted group (container) (typed FeaturePython)
  n = 10
  ref = C_element
FEATURE [App::DocumentObjectGroupPython] N_element065  label="N_element : 037"  # scripted group (container) (typed FeaturePython)
  n = 5
  ref = N_element
FEATURE [App::DocumentObjectGroupPython] O_element127  label="O_element : 8"  # scripted group (container) (typed FeaturePython)
  n = 8
  ref = O_element
FEATURE [App::DocumentObjectGroupPython] P_element016  label="P_element : 005"  # scripted group (container) (typed FeaturePython)
  n = 1
  ref = P_element
FEATURE [App::DocumentObjectGroupPython] G4_DNA_G  # scripted group (container) (typed FeaturePython)
  Dunit = g/cm3
  Dvalue = 1
  Group = -> [H_element136,C_element146,N_element065,O_element127,P_element016]
  conduct = 2
  density = 1
  expand = 3
  formula = G4_DNA_G
  name = G4_DNA_G
  specific = 4
FEATURE [App::DocumentObjectGroupPython] H_element137  label="H_element : 084"  # scripted group (container) (typed FeaturePython)
  n = 10
  ref = H_element
FEATURE [App::DocumentObjectGroupPython] C_element147  label="C_element : 092"  # scripted group (container) (typed FeaturePython)
  n = 9
  ref = C_element
FEATURE [App::DocumentObjectGroupPython] N_element066  label="N_element : 038"  # scripted group (container) (typed FeaturePython)
  n = 3
  ref = N_element
FEATURE [App::DocumentObjectGroupPython] O_element128  label="O_element : 080"  # scripted group (container) (typed FeaturePython)
  n = 8
  ref = O_element
FEATURE [App::DocumentObjectGroupPython] P_element017  label="P_element : 006"  # scripted group (container) (typed FeaturePython)
  n = 1
  ref = P_element
FEATURE [App::DocumentObjectGroupPython] G4_DNA_C  # scripted group (container) (typed FeaturePython)
  Dunit = g/cm3
  Dvalue = 1
  Group = -> [H_element137,C_element147,N_element066,O_element128,P_element017]
  conduct = 2
  density = 1
  expand = 3
  formula = G4_DNA_C
  name = G4_DNA_C
  specific = 4
FEATURE [App::DocumentObjectGroupPython] H_element138  label="H_element : 085"  # scripted group (container) (typed FeaturePython)
  n = 9
  ref = H_element
FEATURE [App::DocumentObjectGroupPython] C_element148  label="C_element : 093"  # scripted group (container) (typed FeaturePython)
  n = 9
  ref = C_element
FEATURE [App::DocumentObjectGroupPython] N_element067  label="N_element : 039"  # scripted group (container) (typed FeaturePython)
  n = 2
  ref = N_element
FEATURE [App::DocumentObjectGroupPython] O_element129  label="O_element : 9"  # scripted group (container) (typed FeaturePython)
  n = 9
  ref = O_element
FEATURE [App::DocumentObjectGroupPython] P_element018  label="P_element : 007"  # scripted group (container) (typed FeaturePython)
  n = 1
  ref = P_element
FEATURE [App::DocumentObjectGroupPython] G4_DNA_U  # scripted group (container) (typed FeaturePython)
  Dunit = g/cm3
  Dvalue = 1
  Group = -> [H_element138,C_element148,N_element067,O_element129,P_element018]
  conduct = 2
  density = 1
  expand = 3
  formula = G4_DNA_U
  name = G4_DNA_U
  specific = 4
FEATURE [App::DocumentObjectGroupPython] H_element139  label="H_element : 086"  # scripted group (container) (typed FeaturePython)
  n = 11
  ref = H_element
FEATURE [App::DocumentObjectGroupPython] C_element149  label="C_element : 094"  # scripted group (container) (typed FeaturePython)
  n = 10
  ref = C_element
FEATURE [App::DocumentObjectGroupPython] N_element068  label="N_element : 040"  # scripted group (container) (typed FeaturePython)
  n = 2
  ref = N_element
FEATURE [App::DocumentObjectGroupPython] O_element130  label="O_element : 081"  # scripted group (container) (typed FeaturePython)
  n = 9
  ref = O_element
FEATURE [App::DocumentObjectGroupPython] P_element019  label="P_element : 008"  # scripted group (container) (typed FeaturePython)
  n = 1
  ref = P_element
FEATURE [App::DocumentObjectGroupPython] G4_DNA_MU  # scripted group (container) (typed FeaturePython)
  Dunit = g/cm3
  Dvalue = 1
  Group = -> [H_element139,C_element149,N_element068,O_element130,P_element019]
  conduct = 2
  density = 1
  expand = 3
  formula = G4_DNA_MU
  name = G4_DNA_MU
  specific = 4
FEATURE [App::DocumentObjectGroupPython] BioChemical  # scripted group (container) (typed FeaturePython)
  Group = -> [G4_CYTOSINE,G4_THYMINE,G4_URACIL,G4_DNA_ADENINE,G4_DNA_GUANINE,G4_DNA_CYTOSINE,G4_DNA_THYMINE,G4_DNA_URACIL,G4_DNA_ADENOSINE,G4_DNA_GUANOSINE,G4_DNA_CYTIDINE,G4_DNA_URIDINE,G4_DNA_METHYLURIDINE,G4_DNA_MONOPHOSPHATE,G4_DNA_A,G4_DNA_G,G4_DNA_C,G4_DNA_U,G4_DNA_MU]
FEATURE [App::DocumentObjectGroupPython] G4Materials  # scripted group (container) (typed FeaturePython)
  Group = -> [NIST,Element,HEP,Space,BioChemical]
  version = 1
FEATURE [App::DocumentObjectGroupPython] Geant4  # scripted group (container) (typed FeaturePython)
  Group = -> [G4Isotopes,G4Elements,G4Materials]
FEATURE [App::DocumentObjectGroupPython] Materials  # scripted group (container) (typed FeaturePython)
  Group = -> [Geant4]
FEATURE [Part::FeaturePython] GDMLBox_WorldBox  # WARN: FeaturePython — macro-defined, semantics opaque (R4)
  lunit = 2
  material = 5
  x = 2350.01
  y = 2367.27
  z = 13016.7
FEATURE [Part::Cylinder] Cylinder
  Angle = 360
  AttacherType = Attacher::AttachEngine3D
  FirstAngle = 0
  Height = 200
  Placement = pos=(474,0,4850) rot=(0,0,1;0rad)
  Radius = 60
  SecondAngle = 0
FEATURE [Part::FeaturePython] Array  # Draft array (typed FeaturePython)
  Angle = 360
  ArrayType = 1
  Axis = (0,0,1)
  Base = -> Cylinder
  Center = (0,0,0)
  Count = 6
  Fuse = false
  IntervalAxis = (0,0,0)
  IntervalX = (50,0,0)
  IntervalY = (0,50,0)
  IntervalZ = (0,0,50)
  NumberCircles = 3
  NumberPolar = 6
  NumberX = 2
  NumberY = 2
  NumberZ = 1
  RadialDistance = 50
  Symmetry = 1
  TangentialDistance = 25
FEATURE [Sketcher::SketchObject] Sketch001
  ArcFitTolerance = 0
  AttachmentSupport = -> [YZ_Plane001]
  FullyConstrained = false
  MakeInternals = false
  MapMode = 5
  Placement = pos=(0,0,0) rot=(0.57735,0.57735,0.57735;2.0944rad)
  sketch-geometry (36):
    g0: LineSegment StartX=345.196 StartY=1207.39 StartZ=0 EndX=345.196 EndY=4779.1 EndZ=0
    g1: LineSegment StartX=910.487 StartY=4896.42 StartZ=0 EndX=910.487 EndY=5006.42 EndZ=0
    g2: LineSegment StartX=435.196 StartY=4869.1 StartZ=0 EndX=445.196 EndY=4869.1 EndZ=0
    g3: LineSegment StartX=445.196 StartY=4869.1 StartZ=0 EndX=445.196 EndY=4896.42 EndZ=0
    g4: LineSegment StartX=445.196 StartY=4896.42 StartZ=0 EndX=910.487 EndY=4896.42 EndZ=0
    g5: LineSegment StartX=318.538 StartY=5006.42 StartZ=0 EndX=910.487 EndY=5006.42 EndZ=0
    g6: LineSegment StartX=175.531 StartY=1234.96 StartZ=0 EndX=318.538 EndY=1234.96 EndZ=0
    g7: LineSegment StartX=318.538 StartY=5006.42 StartZ=0 EndX=318.538 EndY=1234.96 EndZ=0
    g8: LineSegment StartX=0 StartY=39.215 StartZ=0 EndX=0 EndY=0 EndZ=0
    g9-g16: Circle [constr] x8 (B-spline internal-alignment scaffolding for g17; pole/knot coordinates omitted)
    g17: BSplineCurve PolesCount=8 KnotsCount=6 Degree=3 IsPeriodic=0
    g18-g23: GeomPoint [constr] x6 (B-spline internal-alignment scaffolding for g17; pole/knot coordinates omitted)
    g24: LineSegment StartX=175.531 StartY=1234.96 StartZ=0 EndX=175.531 EndY=838.896 EndZ=0
    g25-g29: Circle [constr] x5 (B-spline internal-alignment scaffolding for g30; pole/knot coordinates omitted)
    g30: BSplineCurve PolesCount=5 KnotsCount=3 Degree=3 IsPeriodic=0
    g31: GeomPoint [constr] X=175.531 Y=838.896 Z=0
    g32: GeomPoint [constr] X=165.058 Y=242.363 Z=0
    g33: GeomPoint [constr] X=0 Y=39.215 Z=0
    g34: ArcOfCircle CenterX=435.196 CenterY=4779.1 CenterZ=0 NormalX=0 NormalY=0 NormalZ=1 AngleXU=0 Radius=90 StartAngle=1.5708 EndAngle=3.14159
    g35: GeomPoint [constr] X=345.196 Y=4869.1 Z=0
  constraints (38):
    c: Vertical(g1)
    c: Horizontal(g2)
    c: Coincident(g2,g3)
    c: Vertical(g3)
    c: Coincident(g3,g4)
    c: Coincident(g4,g1)
    c: Horizontal(g4)
    c: Coincident(g5,g1)
    c: Horizontal(g5)
    c: Horizontal(g6)
    c: Coincident(g7,g5)
    c: Coincident(g7,g6)
    c: Vertical(g7)
    c: DistanceX(g35,g2) = 100
    c: Vertical(g8)
    c: Vertical(g0)
    c: Coincident(g17,g0)
    c: Weight(g9) = 1
    c: Equal(g9, g10-g16) x7
    c: Coincident(g17,g8)
    c: InternalAlignment(g9-g16 -> g17) x8
    c: InternalAlignment(g18-g23 -> g17) x6
    c: Coincident(g24,g6)
    c: Vertical(g24)
    c: Coincident(g30,g24)
    c: Weight(g25) = 1
    c: Equal(g25, g26-g29) x4
    c: Coincident(g30,g8)
    c: InternalAlignment(g25-g29 -> g30) x5
    c: InternalAlignment(g31,g30)
    c: InternalAlignment(g32,g30)
    c: InternalAlignment(g33,g30)
    c: Coincident(g8,g-1)
    c: PointOnObject(g35,g2)
    c: PointOnObject(g35,g0)
    c: Tangent(g2,g34) = 1.5708
    c: Tangent(g0,g34) = 1.5708
    c: Radius(g34) = 90
FEATURE [Part::Revolution] Revolve
  Angle = 360
  Axis = (0,0,1)
  Base = (0,0,0)
  FaceMakerClass = Part::FaceMakerBullseye
  Solid = true
  Source = -> Sketch001
  Symmetric = false
  material = 176
FEATURE [Part::Cut] Cut
  Base = -> Revolve
  Tool = -> Array
FEATURE [App::Part] Bool_Cut
  Group = -> [Revolve,Cylinder,Sketch001,Array,Cut]
  Origin = -> Origin004
FEATURE [App::Part] worldVOL
  Group = -> [GDMLBox_WorldBox,Bool_Cut]
  Origin = -> Origin
